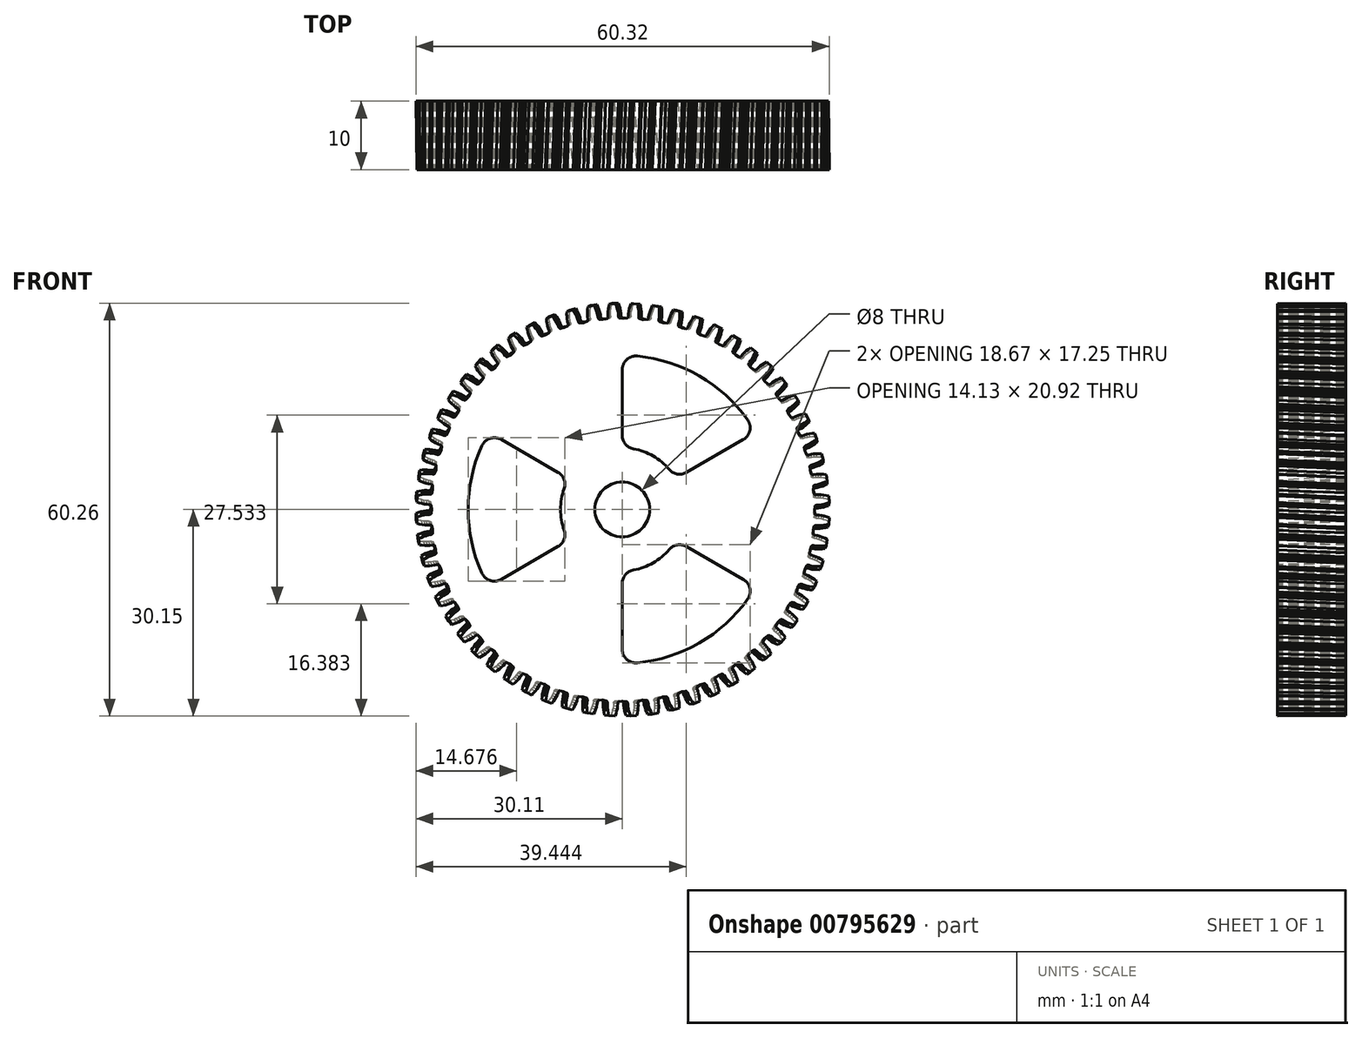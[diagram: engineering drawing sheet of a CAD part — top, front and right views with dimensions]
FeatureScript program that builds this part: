
annotation { "Feature Type Name" : "Feature", "Feature Type Description" : "" }
export const myFeature = defineFeature(function(context is Context, id is Id, definition is map)
    precondition{}
    {
        {
            var Q0;
            Q0=qCreatedBy(makeId("Front.planeOp"),FACE);
            var sketch = newSketch(context, id + "F0", { "sketchPlane" : qUnion([Q0])});
            skLineSegment(sketch, "E0", {"start": v(27.92, -0.53) * mm, "end": v(28, -1.15) * mm});
            skLineSegment(sketch, "E1", {"start": v(28, -1.15) * mm, "end": v(28.09, -1.2) * mm});
            skLineSegment(sketch, "E2", {"start": v(28.09, -1.2) * mm, "end": v(28.27, -1.26) * mm});
            skLineSegment(sketch, "E3", {"start": v(28.27, -1.26) * mm, "end": v(28.63, -1.3) * mm});
            skLineSegment(sketch, "E4", {"start": v(28.63, -1.3) * mm, "end": v(29, -1.35) * mm});
            skLineSegment(sketch, "E5", {"start": v(29, -1.35) * mm, "end": v(29.35, -1.44) * mm});
            skLineSegment(sketch, "E6", {"start": v(29.35, -1.44) * mm, "end": v(29.71, -1.55) * mm});
            skLineSegment(sketch, "E7", {"start": v(29.71, -1.55) * mm, "end": v(30.07, -1.68) * mm});
            skLineSegment(sketch, "E8", {"start": v(30.07, -1.68) * mm, "end": v(30, -2.6) * mm});
            skLineSegment(sketch, "E9", {"start": v(30, -2.6) * mm, "end": v(29.63, -2.69) * mm});
            skLineSegment(sketch, "E10", {"start": v(29.63, -2.69) * mm, "end": v(29.26, -2.74) * mm});
            skLineSegment(sketch, "E11", {"start": v(29.26, -2.74) * mm, "end": v(28.89, -2.78) * mm});
            skLineSegment(sketch, "E12", {"start": v(28.89, -2.78) * mm, "end": v(28.52, -2.79) * mm});
            skLineSegment(sketch, "E13", {"start": v(28.52, -2.79) * mm, "end": v(28.16, -2.77) * mm});
            skLineSegment(sketch, "E14", {"start": v(28.16, -2.77) * mm, "end": v(27.97, -2.8) * mm});
            skLineSegment(sketch, "E15", {"start": v(27.97, -2.8) * mm, "end": v(27.88, -2.84) * mm});
            skLineSegment(sketch, "E16", {"start": v(27.88, -2.84) * mm, "end": v(27.72, -3.44) * mm});
            skLineSegment(sketch, "E17", {"start": v(27.72, -3.44) * mm, "end": v(27.72, -4.07) * mm});
            skLineSegment(sketch, "E18", {"start": v(27.72, -4.07) * mm, "end": v(27.8, -4.13) * mm});
            skLineSegment(sketch, "E19", {"start": v(27.8, -4.13) * mm, "end": v(27.98, -4.2) * mm});
            skLineSegment(sketch, "E20", {"start": v(27.98, -4.2) * mm, "end": v(28.34, -4.28) * mm});
            skLineSegment(sketch, "E21", {"start": v(28.34, -4.28) * mm, "end": v(28.7, -4.37) * mm});
            skLineSegment(sketch, "E22", {"start": v(28.7, -4.37) * mm, "end": v(29.04, -4.5) * mm});
            skLineSegment(sketch, "E23", {"start": v(29.04, -4.5) * mm, "end": v(29.39, -4.65) * mm});
            skLineSegment(sketch, "E24", {"start": v(29.39, -4.65) * mm, "end": v(29.73, -4.81) * mm});
            skLineSegment(sketch, "E25", {"start": v(29.73, -4.81) * mm, "end": v(29.57, -5.73) * mm});
            skLineSegment(sketch, "E26", {"start": v(29.57, -5.73) * mm, "end": v(29.19, -5.77) * mm});
            skLineSegment(sketch, "E27", {"start": v(29.19, -5.77) * mm, "end": v(28.81, -5.79) * mm});
            skLineSegment(sketch, "E28", {"start": v(28.81, -5.79) * mm, "end": v(28.44, -5.79) * mm});
            skLineSegment(sketch, "E29", {"start": v(28.44, -5.79) * mm, "end": v(28.07, -5.75) * mm});
            skLineSegment(sketch, "E30", {"start": v(28.07, -5.75) * mm, "end": v(27.71, -5.7) * mm});
            skLineSegment(sketch, "E31", {"start": v(27.71, -5.7) * mm, "end": v(27.52, -5.7) * mm});
            skLineSegment(sketch, "E32", {"start": v(27.52, -5.7) * mm, "end": v(27.43, -5.74) * mm});
            skLineSegment(sketch, "E33", {"start": v(27.43, -5.74) * mm, "end": v(27.2, -6.32) * mm});
            skLineSegment(sketch, "E34", {"start": v(27.2, -6.32) * mm, "end": v(27.15, -6.94) * mm});
            skLineSegment(sketch, "E35", {"start": v(27.15, -6.94) * mm, "end": v(27.22, -7.01) * mm});
            skLineSegment(sketch, "E36", {"start": v(27.22, -7.01) * mm, "end": v(27.39, -7.1) * mm});
            skLineSegment(sketch, "E37", {"start": v(27.39, -7.1) * mm, "end": v(27.74, -7.21) * mm});
            skLineSegment(sketch, "E38", {"start": v(27.74, -7.21) * mm, "end": v(28.08, -7.35) * mm});
            skLineSegment(sketch, "E39", {"start": v(28.08, -7.35) * mm, "end": v(28.41, -7.5) * mm});
            skLineSegment(sketch, "E40", {"start": v(28.41, -7.5) * mm, "end": v(28.74, -7.7) * mm});
            skLineSegment(sketch, "E41", {"start": v(28.74, -7.7) * mm, "end": v(29.06, -7.9) * mm});
            skLineSegment(sketch, "E42", {"start": v(29.06, -7.9) * mm, "end": v(28.8, -8.79) * mm});
            skLineSegment(sketch, "E43", {"start": v(28.8, -8.79) * mm, "end": v(28.43, -8.79) * mm});
            skLineSegment(sketch, "E44", {"start": v(28.43, -8.79) * mm, "end": v(28.05, -8.77) * mm});
            skLineSegment(sketch, "E45", {"start": v(28.05, -8.77) * mm, "end": v(27.68, -8.73) * mm});
            skLineSegment(sketch, "E46", {"start": v(27.68, -8.73) * mm, "end": v(27.32, -8.66) * mm});
            skLineSegment(sketch, "E47", {"start": v(27.32, -8.66) * mm, "end": v(26.97, -8.56) * mm});
            skLineSegment(sketch, "E48", {"start": v(26.97, -8.56) * mm, "end": v(26.78, -8.55) * mm});
            skLineSegment(sketch, "E49", {"start": v(26.78, -8.55) * mm, "end": v(26.68, -8.57) * mm});
            skLineSegment(sketch, "E50", {"start": v(26.68, -8.57) * mm, "end": v(26.4, -9.13) * mm});
            skLineSegment(sketch, "E51", {"start": v(26.4, -9.13) * mm, "end": v(26.27, -9.74) * mm});
            skLineSegment(sketch, "E52", {"start": v(26.27, -9.74) * mm, "end": v(26.34, -9.82) * mm});
            skLineSegment(sketch, "E53", {"start": v(26.34, -9.82) * mm, "end": v(26.5, -9.93) * mm});
            skLineSegment(sketch, "E54", {"start": v(26.5, -9.93) * mm, "end": v(26.83, -10.07) * mm});
            skLineSegment(sketch, "E55", {"start": v(26.83, -10.07) * mm, "end": v(27.16, -10.24) * mm});
            skLineSegment(sketch, "E56", {"start": v(27.16, -10.24) * mm, "end": v(27.47, -10.44) * mm});
            skLineSegment(sketch, "E57", {"start": v(27.47, -10.44) * mm, "end": v(27.78, -10.65) * mm});
            skLineSegment(sketch, "E58", {"start": v(27.78, -10.65) * mm, "end": v(28.08, -10.89) * mm});
            skLineSegment(sketch, "E59", {"start": v(28.08, -10.89) * mm, "end": v(27.73, -11.75) * mm});
            skLineSegment(sketch, "E60", {"start": v(27.73, -11.75) * mm, "end": v(27.35, -11.71) * mm});
            skLineSegment(sketch, "E61", {"start": v(27.35, -11.71) * mm, "end": v(26.98, -11.65) * mm});
            skLineSegment(sketch, "E62", {"start": v(26.98, -11.65) * mm, "end": v(26.62, -11.57) * mm});
            skLineSegment(sketch, "E63", {"start": v(26.62, -11.57) * mm, "end": v(26.27, -11.46) * mm});
            skLineSegment(sketch, "E64", {"start": v(26.27, -11.46) * mm, "end": v(25.92, -11.33) * mm});
            skLineSegment(sketch, "E65", {"start": v(25.92, -11.33) * mm, "end": v(25.74, -11.3) * mm});
            skLineSegment(sketch, "E66", {"start": v(25.74, -11.3) * mm, "end": v(25.63, -11.31) * mm});
            skLineSegment(sketch, "E67", {"start": v(25.63, -11.31) * mm, "end": v(25.3, -11.84) * mm});
            skLineSegment(sketch, "E68", {"start": v(25.3, -11.84) * mm, "end": v(25.1, -12.43) * mm});
            skLineSegment(sketch, "E69", {"start": v(25.1, -12.43) * mm, "end": v(25.17, -12.52) * mm});
            skLineSegment(sketch, "E70", {"start": v(25.17, -12.52) * mm, "end": v(25.31, -12.64) * mm});
            skLineSegment(sketch, "E71", {"start": v(25.31, -12.64) * mm, "end": v(25.63, -12.82) * mm});
            skLineSegment(sketch, "E72", {"start": v(25.63, -12.82) * mm, "end": v(25.94, -13.02) * mm});
            skLineSegment(sketch, "E73", {"start": v(25.94, -13.02) * mm, "end": v(26.23, -13.25) * mm});
            skLineSegment(sketch, "E74", {"start": v(26.23, -13.25) * mm, "end": v(26.51, -13.5) * mm});
            skLineSegment(sketch, "E75", {"start": v(26.51, -13.5) * mm, "end": v(26.79, -13.76) * mm});
            skLineSegment(sketch, "E76", {"start": v(26.79, -13.76) * mm, "end": v(26.35, -14.59) * mm});
            skLineSegment(sketch, "E77", {"start": v(26.35, -14.59) * mm, "end": v(25.98, -14.5) * mm});
            skLineSegment(sketch, "E78", {"start": v(25.98, -14.5) * mm, "end": v(25.61, -14.4) * mm});
            skLineSegment(sketch, "E79", {"start": v(25.61, -14.4) * mm, "end": v(25.26, -14.3) * mm});
            skLineSegment(sketch, "E80", {"start": v(25.26, -14.3) * mm, "end": v(24.92, -14.15) * mm});
            skLineSegment(sketch, "E81", {"start": v(24.92, -14.15) * mm, "end": v(24.6, -13.98) * mm});
            skLineSegment(sketch, "E82", {"start": v(24.6, -13.98) * mm, "end": v(24.41, -13.93) * mm});
            skLineSegment(sketch, "E83", {"start": v(24.41, -13.93) * mm, "end": v(24.31, -13.93) * mm});
            skLineSegment(sketch, "E84", {"start": v(24.31, -13.93) * mm, "end": v(23.92, -14.42) * mm});
            skLineSegment(sketch, "E85", {"start": v(23.92, -14.42) * mm, "end": v(23.67, -15) * mm});
            skLineSegment(sketch, "E86", {"start": v(23.67, -15) * mm, "end": v(23.72, -15.08) * mm});
            skLineSegment(sketch, "E87", {"start": v(23.72, -15.08) * mm, "end": v(23.85, -15.22) * mm});
            skLineSegment(sketch, "E88", {"start": v(23.85, -15.22) * mm, "end": v(24.15, -15.43) * mm});
            skLineSegment(sketch, "E89", {"start": v(24.15, -15.43) * mm, "end": v(24.43, -15.66) * mm});
            skLineSegment(sketch, "E90", {"start": v(24.43, -15.66) * mm, "end": v(24.7, -15.92) * mm});
            skLineSegment(sketch, "E91", {"start": v(24.7, -15.92) * mm, "end": v(24.96, -16.2) * mm});
            skLineSegment(sketch, "E92", {"start": v(24.96, -16.2) * mm, "end": v(25.2, -16.49) * mm});
            skLineSegment(sketch, "E93", {"start": v(25.2, -16.49) * mm, "end": v(24.68, -17.26) * mm});
            skLineSegment(sketch, "E94", {"start": v(24.68, -17.26) * mm, "end": v(24.32, -17.14) * mm});
            skLineSegment(sketch, "E95", {"start": v(24.32, -17.14) * mm, "end": v(23.97, -17) * mm});
            skLineSegment(sketch, "E96", {"start": v(23.97, -17) * mm, "end": v(23.63, -16.85) * mm});
            skLineSegment(sketch, "E97", {"start": v(23.63, -16.85) * mm, "end": v(23.3, -16.67) * mm});
            skLineSegment(sketch, "E98", {"start": v(23.3, -16.67) * mm, "end": v(23, -16.48) * mm});
            skLineSegment(sketch, "E99", {"start": v(23, -16.48) * mm, "end": v(22.82, -16.41) * mm});
            skLineSegment(sketch, "E100", {"start": v(22.82, -16.41) * mm, "end": v(22.72, -16.4) * mm});
            skLineSegment(sketch, "E101", {"start": v(22.72, -16.4) * mm, "end": v(22.28, -16.84) * mm});
            skLineSegment(sketch, "E102", {"start": v(22.28, -16.84) * mm, "end": v(21.98, -17.38) * mm});
            skLineSegment(sketch, "E103", {"start": v(21.98, -17.38) * mm, "end": v(22.02, -17.48) * mm});
            skLineSegment(sketch, "E104", {"start": v(22.02, -17.48) * mm, "end": v(22.13, -17.63) * mm});
            skLineSegment(sketch, "E105", {"start": v(22.13, -17.63) * mm, "end": v(22.4, -17.87) * mm});
            skLineSegment(sketch, "E106", {"start": v(22.4, -17.87) * mm, "end": v(22.66, -18.13) * mm});
            skLineSegment(sketch, "E107", {"start": v(22.66, -18.13) * mm, "end": v(22.9, -18.42) * mm});
            skLineSegment(sketch, "E108", {"start": v(22.9, -18.42) * mm, "end": v(23.13, -18.72) * mm});
            skLineSegment(sketch, "E109", {"start": v(23.13, -18.72) * mm, "end": v(23.34, -19.03) * mm});
            skLineSegment(sketch, "E110", {"start": v(23.34, -19.03) * mm, "end": v(22.74, -19.75) * mm});
            skLineSegment(sketch, "E111", {"start": v(22.74, -19.75) * mm, "end": v(22.4, -19.59) * mm});
            skLineSegment(sketch, "E112", {"start": v(22.4, -19.59) * mm, "end": v(22.06, -19.42) * mm});
            skLineSegment(sketch, "E113", {"start": v(22.06, -19.42) * mm, "end": v(21.74, -19.23) * mm});
            skLineSegment(sketch, "E114", {"start": v(21.74, -19.23) * mm, "end": v(21.44, -19.02) * mm});
            skLineSegment(sketch, "E115", {"start": v(21.44, -19.02) * mm, "end": v(21.15, -18.8) * mm});
            skLineSegment(sketch, "E116", {"start": v(21.15, -18.8) * mm, "end": v(20.98, -18.7) * mm});
            skLineSegment(sketch, "E117", {"start": v(20.98, -18.7) * mm, "end": v(20.88, -18.68) * mm});
            skLineSegment(sketch, "E118", {"start": v(20.88, -18.68) * mm, "end": v(20.4, -19.08) * mm});
            skLineSegment(sketch, "E119", {"start": v(20.4, -19.08) * mm, "end": v(20.04, -19.59) * mm});
            skLineSegment(sketch, "E120", {"start": v(20.04, -19.59) * mm, "end": v(20.07, -19.68) * mm});
            skLineSegment(sketch, "E121", {"start": v(20.07, -19.68) * mm, "end": v(20.16, -19.85) * mm});
            skLineSegment(sketch, "E122", {"start": v(20.16, -19.85) * mm, "end": v(20.41, -20.12) * mm});
            skLineSegment(sketch, "E123", {"start": v(20.41, -20.12) * mm, "end": v(20.64, -20.4) * mm});
            skLineSegment(sketch, "E124", {"start": v(20.64, -20.4) * mm, "end": v(20.85, -20.7) * mm});
            skLineSegment(sketch, "E125", {"start": v(20.85, -20.7) * mm, "end": v(21.04, -21.03) * mm});
            skLineSegment(sketch, "E126", {"start": v(21.04, -21.03) * mm, "end": v(21.22, -21.37) * mm});
            skLineSegment(sketch, "E127", {"start": v(21.22, -21.37) * mm, "end": v(20.55, -22.01) * mm});
            skLineSegment(sketch, "E128", {"start": v(20.55, -22.01) * mm, "end": v(20.22, -21.82) * mm});
            skLineSegment(sketch, "E129", {"start": v(20.22, -21.82) * mm, "end": v(19.9, -21.62) * mm});
            skLineSegment(sketch, "E130", {"start": v(19.9, -21.62) * mm, "end": v(19.6, -21.4) * mm});
            skLineSegment(sketch, "E131", {"start": v(19.6, -21.4) * mm, "end": v(19.33, -21.16) * mm});
            skLineSegment(sketch, "E132", {"start": v(19.33, -21.16) * mm, "end": v(19.07, -20.9) * mm});
            skLineSegment(sketch, "E133", {"start": v(19.07, -20.9) * mm, "end": v(18.91, -20.8) * mm});
            skLineSegment(sketch, "E134", {"start": v(18.91, -20.8) * mm, "end": v(18.82, -20.76) * mm});
            skLineSegment(sketch, "E135", {"start": v(18.82, -20.76) * mm, "end": v(18.3, -21.1) * mm});
            skLineSegment(sketch, "E136", {"start": v(18.3, -21.1) * mm, "end": v(17.88, -21.57) * mm});
            skLineSegment(sketch, "E137", {"start": v(17.88, -21.57) * mm, "end": v(17.9, -21.67) * mm});
            skLineSegment(sketch, "E138", {"start": v(17.9, -21.67) * mm, "end": v(17.98, -21.85) * mm});
            skLineSegment(sketch, "E139", {"start": v(17.98, -21.85) * mm, "end": v(18.2, -22.14) * mm});
            skLineSegment(sketch, "E140", {"start": v(18.2, -22.14) * mm, "end": v(18.4, -22.45) * mm});
            skLineSegment(sketch, "E141", {"start": v(18.4, -22.45) * mm, "end": v(18.57, -22.77) * mm});
            skLineSegment(sketch, "E142", {"start": v(18.57, -22.77) * mm, "end": v(18.73, -23.12) * mm});
            skLineSegment(sketch, "E143", {"start": v(18.73, -23.12) * mm, "end": v(18.87, -23.47) * mm});
            skLineSegment(sketch, "E144", {"start": v(18.87, -23.47) * mm, "end": v(18.14, -24.04) * mm});
            skLineSegment(sketch, "E145", {"start": v(18.14, -24.04) * mm, "end": v(17.83, -23.82) * mm});
            skLineSegment(sketch, "E146", {"start": v(17.83, -23.82) * mm, "end": v(17.54, -23.58) * mm});
            skLineSegment(sketch, "E147", {"start": v(17.54, -23.58) * mm, "end": v(17.26, -23.33) * mm});
            skLineSegment(sketch, "E148", {"start": v(17.26, -23.33) * mm, "end": v(17.01, -23.06) * mm});
            skLineSegment(sketch, "E149", {"start": v(17.01, -23.06) * mm, "end": v(16.78, -22.78) * mm});
            skLineSegment(sketch, "E150", {"start": v(16.78, -22.78) * mm, "end": v(16.64, -22.66) * mm});
            skLineSegment(sketch, "E151", {"start": v(16.64, -22.66) * mm, "end": v(16.54, -22.61) * mm});
            skLineSegment(sketch, "E152", {"start": v(16.54, -22.61) * mm, "end": v(15.99, -22.9) * mm});
            skLineSegment(sketch, "E153", {"start": v(15.99, -22.9) * mm, "end": v(15.53, -23.32) * mm});
            skLineSegment(sketch, "E154", {"start": v(15.53, -23.32) * mm, "end": v(15.54, -23.43) * mm});
            skLineSegment(sketch, "E155", {"start": v(15.54, -23.43) * mm, "end": v(15.6, -23.6) * mm});
            skLineSegment(sketch, "E156", {"start": v(15.6, -23.6) * mm, "end": v(15.78, -23.92) * mm});
            skLineSegment(sketch, "E157", {"start": v(15.78, -23.92) * mm, "end": v(15.95, -24.25) * mm});
            skLineSegment(sketch, "E158", {"start": v(15.95, -24.25) * mm, "end": v(16.1, -24.6) * mm});
            skLineSegment(sketch, "E159", {"start": v(16.1, -24.6) * mm, "end": v(16.21, -24.95) * mm});
            skLineSegment(sketch, "E160", {"start": v(16.21, -24.95) * mm, "end": v(16.32, -25.31) * mm});
            skLineSegment(sketch, "E161", {"start": v(16.32, -25.31) * mm, "end": v(15.53, -25.8) * mm});
            skLineSegment(sketch, "E162", {"start": v(15.53, -25.8) * mm, "end": v(15.24, -25.55) * mm});
            skLineSegment(sketch, "E163", {"start": v(15.24, -25.55) * mm, "end": v(14.98, -25.28) * mm});
            skLineSegment(sketch, "E164", {"start": v(14.98, -25.28) * mm, "end": v(14.73, -25) * mm});
            skLineSegment(sketch, "E165", {"start": v(14.73, -25) * mm, "end": v(14.51, -24.71) * mm});
            skLineSegment(sketch, "E166", {"start": v(14.51, -24.71) * mm, "end": v(14.31, -24.4) * mm});
            skLineSegment(sketch, "E167", {"start": v(14.31, -24.4) * mm, "end": v(14.18, -24.27) * mm});
            skLineSegment(sketch, "E168", {"start": v(14.18, -24.27) * mm, "end": v(14.09, -24.22) * mm});
            skLineSegment(sketch, "E169", {"start": v(14.09, -24.22) * mm, "end": v(13.5, -24.45) * mm});
            skLineSegment(sketch, "E170", {"start": v(13.5, -24.45) * mm, "end": v(13, -24.82) * mm});
            skLineSegment(sketch, "E171", {"start": v(13, -24.82) * mm, "end": v(13, -24.92) * mm});
            skLineSegment(sketch, "E172", {"start": v(13, -24.92) * mm, "end": v(13.05, -25.1) * mm});
            skLineSegment(sketch, "E173", {"start": v(13.05, -25.1) * mm, "end": v(13.2, -25.44) * mm});
            skLineSegment(sketch, "E174", {"start": v(13.2, -25.44) * mm, "end": v(13.33, -25.78) * mm});
            skLineSegment(sketch, "E175", {"start": v(13.33, -25.78) * mm, "end": v(13.43, -26.14) * mm});
            skLineSegment(sketch, "E176", {"start": v(13.43, -26.14) * mm, "end": v(13.52, -26.5) * mm});
            skLineSegment(sketch, "E177", {"start": v(13.52, -26.5) * mm, "end": v(13.58, -26.88) * mm});
            skLineSegment(sketch, "E178", {"start": v(13.58, -26.88) * mm, "end": v(12.74, -27.29) * mm});
            skLineSegment(sketch, "E179", {"start": v(12.74, -27.29) * mm, "end": v(12.5, -27) * mm});
            skLineSegment(sketch, "E180", {"start": v(12.5, -27) * mm, "end": v(12.25, -26.71) * mm});
            skLineSegment(sketch, "E181", {"start": v(12.25, -26.71) * mm, "end": v(12.04, -26.4) * mm});
            skLineSegment(sketch, "E182", {"start": v(12.04, -26.4) * mm, "end": v(11.85, -26.1) * mm});
            skLineSegment(sketch, "E183", {"start": v(11.85, -26.1) * mm, "end": v(11.68, -25.77) * mm});
            skLineSegment(sketch, "E184", {"start": v(11.68, -25.77) * mm, "end": v(11.56, -25.62) * mm});
            skLineSegment(sketch, "E185", {"start": v(11.56, -25.62) * mm, "end": v(11.48, -25.56) * mm});
            skLineSegment(sketch, "E186", {"start": v(11.48, -25.56) * mm, "end": v(10.88, -25.72) * mm});
            skLineSegment(sketch, "E187", {"start": v(10.88, -25.72) * mm, "end": v(10.34, -26.04) * mm});
            skLineSegment(sketch, "E188", {"start": v(10.34, -26.04) * mm, "end": v(10.33, -26.14) * mm});
            skLineSegment(sketch, "E189", {"start": v(10.33, -26.14) * mm, "end": v(10.35, -26.33) * mm});
            skLineSegment(sketch, "E190", {"start": v(10.35, -26.33) * mm, "end": v(10.47, -26.68) * mm});
            skLineSegment(sketch, "E191", {"start": v(10.47, -26.68) * mm, "end": v(10.56, -27.03) * mm});
            skLineSegment(sketch, "E192", {"start": v(10.56, -27.03) * mm, "end": v(10.63, -27.4) * mm});
            skLineSegment(sketch, "E193", {"start": v(10.63, -27.4) * mm, "end": v(10.67, -27.77) * mm});
            skLineSegment(sketch, "E194", {"start": v(10.67, -27.77) * mm, "end": v(10.7, -28.15) * mm});
            skLineSegment(sketch, "E195", {"start": v(10.7, -28.15) * mm, "end": v(9.82, -28.47) * mm});
            skLineSegment(sketch, "E196", {"start": v(9.82, -28.47) * mm, "end": v(9.6, -28.16) * mm});
            skLineSegment(sketch, "E197", {"start": v(9.6, -28.16) * mm, "end": v(9.4, -27.85) * mm});
            skLineSegment(sketch, "E198", {"start": v(9.4, -27.85) * mm, "end": v(9.2, -27.52) * mm});
            skLineSegment(sketch, "E199", {"start": v(9.2, -27.52) * mm, "end": v(9.06, -27.19) * mm});
            skLineSegment(sketch, "E200", {"start": v(9.06, -27.19) * mm, "end": v(8.92, -26.85) * mm});
            skLineSegment(sketch, "E201", {"start": v(8.92, -26.85) * mm, "end": v(8.82, -26.7) * mm});
            skLineSegment(sketch, "E202", {"start": v(8.82, -26.7) * mm, "end": v(8.74, -26.62) * mm});
            skLineSegment(sketch, "E203", {"start": v(8.74, -26.62) * mm, "end": v(8.13, -26.72) * mm});
            skLineSegment(sketch, "E204", {"start": v(8.13, -26.72) * mm, "end": v(7.56, -26.98) * mm});
            skLineSegment(sketch, "E205", {"start": v(7.56, -26.98) * mm, "end": v(7.54, -27.08) * mm});
            skLineSegment(sketch, "E206", {"start": v(7.54, -27.08) * mm, "end": v(7.54, -27.27) * mm});
            skLineSegment(sketch, "E207", {"start": v(7.54, -27.27) * mm, "end": v(7.62, -27.63) * mm});
            skLineSegment(sketch, "E208", {"start": v(7.62, -27.63) * mm, "end": v(7.68, -27.99) * mm});
            skLineSegment(sketch, "E209", {"start": v(7.68, -27.99) * mm, "end": v(7.7, -28.36) * mm});
            skLineSegment(sketch, "E210", {"start": v(7.7, -28.36) * mm, "end": v(7.7, -28.74) * mm});
            skLineSegment(sketch, "E211", {"start": v(7.7, -28.74) * mm, "end": v(7.7, -29.12) * mm});
            skLineSegment(sketch, "E212", {"start": v(7.7, -29.12) * mm, "end": v(6.8, -29.34) * mm});
            skLineSegment(sketch, "E213", {"start": v(6.8, -29.34) * mm, "end": v(6.6, -29.01) * mm});
            skLineSegment(sketch, "E214", {"start": v(6.6, -29.01) * mm, "end": v(6.43, -28.68) * mm});
            skLineSegment(sketch, "E215", {"start": v(6.43, -28.68) * mm, "end": v(6.28, -28.33) * mm});
            skLineSegment(sketch, "E216", {"start": v(6.28, -28.33) * mm, "end": v(6.16, -27.99) * mm});
            skLineSegment(sketch, "E217", {"start": v(6.16, -27.99) * mm, "end": v(6.07, -27.63) * mm});
            skLineSegment(sketch, "E218", {"start": v(6.07, -27.63) * mm, "end": v(5.98, -27.47) * mm});
            skLineSegment(sketch, "E219", {"start": v(5.98, -27.47) * mm, "end": v(5.91, -27.39) * mm});
            skLineSegment(sketch, "E220", {"start": v(5.91, -27.39) * mm, "end": v(5.3, -27.42) * mm});
            skLineSegment(sketch, "E221", {"start": v(5.3, -27.42) * mm, "end": v(4.7, -27.62) * mm});
            skLineSegment(sketch, "E222", {"start": v(4.7, -27.62) * mm, "end": v(4.67, -27.72) * mm});
            skLineSegment(sketch, "E223", {"start": v(4.67, -27.72) * mm, "end": v(4.65, -27.9) * mm});
            skLineSegment(sketch, "E224", {"start": v(4.65, -27.9) * mm, "end": v(4.7, -28.27) * mm});
            skLineSegment(sketch, "E225", {"start": v(4.7, -28.27) * mm, "end": v(4.7, -28.64) * mm});
            skLineSegment(sketch, "E226", {"start": v(4.7, -28.64) * mm, "end": v(4.7, -29) * mm});
            skLineSegment(sketch, "E227", {"start": v(4.7, -29) * mm, "end": v(4.66, -29.38) * mm});
            skLineSegment(sketch, "E228", {"start": v(4.66, -29.38) * mm, "end": v(4.61, -29.76) * mm});
            skLineSegment(sketch, "E229", {"start": v(4.61, -29.76) * mm, "end": v(3.69, -29.9) * mm});
            skLineSegment(sketch, "E230", {"start": v(3.69, -29.9) * mm, "end": v(3.53, -29.54) * mm});
            skLineSegment(sketch, "E231", {"start": v(3.53, -29.54) * mm, "end": v(3.4, -29.2) * mm});
            skLineSegment(sketch, "E232", {"start": v(3.4, -29.2) * mm, "end": v(3.29, -28.84) * mm});
            skLineSegment(sketch, "E233", {"start": v(3.29, -28.84) * mm, "end": v(3.2, -28.48) * mm});
            skLineSegment(sketch, "E234", {"start": v(3.2, -28.48) * mm, "end": v(3.15, -28.12) * mm});
            skLineSegment(sketch, "E235", {"start": v(3.15, -28.12) * mm, "end": v(3.08, -27.94) * mm});
            skLineSegment(sketch, "E236", {"start": v(3.08, -27.94) * mm, "end": v(3.02, -27.86) * mm});
            skLineSegment(sketch, "E237", {"start": v(3.02, -27.86) * mm, "end": v(2.4, -27.83) * mm});
            skLineSegment(sketch, "E238", {"start": v(2.4, -27.83) * mm, "end": v(1.79, -27.96) * mm});
            skLineSegment(sketch, "E239", {"start": v(1.79, -27.96) * mm, "end": v(1.74, -28.06) * mm});
            skLineSegment(sketch, "E240", {"start": v(1.74, -28.06) * mm, "end": v(1.7, -28.24) * mm});
            skLineSegment(sketch, "E241", {"start": v(1.7, -28.24) * mm, "end": v(1.7, -28.6) * mm});
            skLineSegment(sketch, "E242", {"start": v(1.7, -28.6) * mm, "end": v(1.7, -28.97) * mm});
            skLineSegment(sketch, "E243", {"start": v(1.7, -28.97) * mm, "end": v(1.64, -29.34) * mm});
            skLineSegment(sketch, "E244", {"start": v(1.64, -29.34) * mm, "end": v(1.57, -29.71) * mm});
            skLineSegment(sketch, "E245", {"start": v(1.57, -29.71) * mm, "end": v(1.47, -30.08) * mm});
            skLineSegment(sketch, "E246", {"start": v(1.47, -30.08) * mm, "end": v(0.54, -30.11) * mm});
            skLineSegment(sketch, "E247", {"start": v(0.54, -30.11) * mm, "end": v(0.43, -29.75) * mm});
            skLineSegment(sketch, "E248", {"start": v(0.43, -29.75) * mm, "end": v(0.33, -29.39) * mm});
            skLineSegment(sketch, "E249", {"start": v(0.33, -29.39) * mm, "end": v(0.25, -29.02) * mm});
            skLineSegment(sketch, "E250", {"start": v(0.25, -29.02) * mm, "end": v(0.21, -28.66) * mm});
            skLineSegment(sketch, "E251", {"start": v(0.21, -28.66) * mm, "end": v(0.19, -28.3) * mm});
            skLineSegment(sketch, "E252", {"start": v(0.19, -28.3) * mm, "end": v(0.14, -28.11) * mm});
            skLineSegment(sketch, "E253", {"start": v(0.14, -28.11) * mm, "end": v(0.1, -28.02) * mm});
            skLineSegment(sketch, "E254", {"start": v(0.1, -28.02) * mm, "end": v(-0.53, -27.92) * mm});
            skLineSegment(sketch, "E255", {"start": v(-0.53, -27.92) * mm, "end": v(-1.15, -28) * mm});
            skLineSegment(sketch, "E256", {"start": v(-1.15, -28) * mm, "end": v(-1.2, -28.09) * mm});
            skLineSegment(sketch, "E257", {"start": v(-1.2, -28.09) * mm, "end": v(-1.26, -28.27) * mm});
            skLineSegment(sketch, "E258", {"start": v(-1.26, -28.27) * mm, "end": v(-1.3, -28.63) * mm});
            skLineSegment(sketch, "E259", {"start": v(-1.3, -28.63) * mm, "end": v(-1.35, -29) * mm});
            skLineSegment(sketch, "E260", {"start": v(-1.35, -29) * mm, "end": v(-1.44, -29.35) * mm});
            skLineSegment(sketch, "E261", {"start": v(-1.44, -29.35) * mm, "end": v(-1.55, -29.71) * mm});
            skLineSegment(sketch, "E262", {"start": v(-1.55, -29.71) * mm, "end": v(-1.68, -30.07) * mm});
            skLineSegment(sketch, "E263", {"start": v(-1.68, -30.07) * mm, "end": v(-2.6, -30) * mm});
            skLineSegment(sketch, "E264", {"start": v(-2.6, -30) * mm, "end": v(-2.69, -29.63) * mm});
            skLineSegment(sketch, "E265", {"start": v(-2.69, -29.63) * mm, "end": v(-2.74, -29.26) * mm});
            skLineSegment(sketch, "E266", {"start": v(-2.74, -29.26) * mm, "end": v(-2.78, -28.89) * mm});
            skLineSegment(sketch, "E267", {"start": v(-2.78, -28.89) * mm, "end": v(-2.79, -28.52) * mm});
            skLineSegment(sketch, "E268", {"start": v(-2.79, -28.52) * mm, "end": v(-2.77, -28.16) * mm});
            skLineSegment(sketch, "E269", {"start": v(-2.77, -28.16) * mm, "end": v(-2.8, -27.97) * mm});
            skLineSegment(sketch, "E270", {"start": v(-2.8, -27.97) * mm, "end": v(-2.84, -27.88) * mm});
            skLineSegment(sketch, "E271", {"start": v(-2.84, -27.88) * mm, "end": v(-3.44, -27.72) * mm});
            skLineSegment(sketch, "E272", {"start": v(-3.44, -27.72) * mm, "end": v(-4.07, -27.72) * mm});
            skLineSegment(sketch, "E273", {"start": v(-4.07, -27.72) * mm, "end": v(-4.13, -27.8) * mm});
            skLineSegment(sketch, "E274", {"start": v(-4.13, -27.8) * mm, "end": v(-4.2, -27.98) * mm});
            skLineSegment(sketch, "E275", {"start": v(-4.2, -27.98) * mm, "end": v(-4.28, -28.34) * mm});
            skLineSegment(sketch, "E276", {"start": v(-4.28, -28.34) * mm, "end": v(-4.37, -28.7) * mm});
            skLineSegment(sketch, "E277", {"start": v(-4.37, -28.7) * mm, "end": v(-4.5, -29.04) * mm});
            skLineSegment(sketch, "E278", {"start": v(-4.5, -29.04) * mm, "end": v(-4.65, -29.39) * mm});
            skLineSegment(sketch, "E279", {"start": v(-4.65, -29.39) * mm, "end": v(-4.81, -29.73) * mm});
            skLineSegment(sketch, "E280", {"start": v(-4.81, -29.73) * mm, "end": v(-5.73, -29.57) * mm});
            skLineSegment(sketch, "E281", {"start": v(-5.73, -29.57) * mm, "end": v(-5.77, -29.19) * mm});
            skLineSegment(sketch, "E282", {"start": v(-5.77, -29.19) * mm, "end": v(-5.79, -28.81) * mm});
            skLineSegment(sketch, "E283", {"start": v(-5.79, -28.81) * mm, "end": v(-5.79, -28.44) * mm});
            skLineSegment(sketch, "E284", {"start": v(-5.79, -28.44) * mm, "end": v(-5.75, -28.07) * mm});
            skLineSegment(sketch, "E285", {"start": v(-5.75, -28.07) * mm, "end": v(-5.7, -27.71) * mm});
            skLineSegment(sketch, "E286", {"start": v(-5.7, -27.71) * mm, "end": v(-5.7, -27.52) * mm});
            skLineSegment(sketch, "E287", {"start": v(-5.7, -27.52) * mm, "end": v(-5.74, -27.43) * mm});
            skLineSegment(sketch, "E288", {"start": v(-5.74, -27.43) * mm, "end": v(-6.32, -27.2) * mm});
            skLineSegment(sketch, "E289", {"start": v(-6.32, -27.2) * mm, "end": v(-6.94, -27.15) * mm});
            skLineSegment(sketch, "E290", {"start": v(-6.94, -27.15) * mm, "end": v(-7.01, -27.22) * mm});
            skLineSegment(sketch, "E291", {"start": v(-7.01, -27.22) * mm, "end": v(-7.1, -27.39) * mm});
            skLineSegment(sketch, "E292", {"start": v(-7.1, -27.39) * mm, "end": v(-7.21, -27.74) * mm});
            skLineSegment(sketch, "E293", {"start": v(-7.21, -27.74) * mm, "end": v(-7.35, -28.08) * mm});
            skLineSegment(sketch, "E294", {"start": v(-7.35, -28.08) * mm, "end": v(-7.5, -28.41) * mm});
            skLineSegment(sketch, "E295", {"start": v(-7.5, -28.41) * mm, "end": v(-7.7, -28.74) * mm});
            skLineSegment(sketch, "E296", {"start": v(-7.7, -28.74) * mm, "end": v(-7.9, -29.06) * mm});
            skLineSegment(sketch, "E297", {"start": v(-7.9, -29.06) * mm, "end": v(-8.79, -28.8) * mm});
            skLineSegment(sketch, "E298", {"start": v(-8.79, -28.8) * mm, "end": v(-8.79, -28.43) * mm});
            skLineSegment(sketch, "E299", {"start": v(-8.79, -28.43) * mm, "end": v(-8.77, -28.05) * mm});
            skLineSegment(sketch, "E300", {"start": v(-8.77, -28.05) * mm, "end": v(-8.73, -27.68) * mm});
            skLineSegment(sketch, "E301", {"start": v(-8.73, -27.68) * mm, "end": v(-8.66, -27.32) * mm});
            skLineSegment(sketch, "E302", {"start": v(-8.66, -27.32) * mm, "end": v(-8.56, -26.97) * mm});
            skLineSegment(sketch, "E303", {"start": v(-8.56, -26.97) * mm, "end": v(-8.55, -26.78) * mm});
            skLineSegment(sketch, "E304", {"start": v(-8.55, -26.78) * mm, "end": v(-8.57, -26.68) * mm});
            skLineSegment(sketch, "E305", {"start": v(-8.57, -26.68) * mm, "end": v(-9.13, -26.4) * mm});
            skLineSegment(sketch, "E306", {"start": v(-9.13, -26.4) * mm, "end": v(-9.74, -26.27) * mm});
            skLineSegment(sketch, "E307", {"start": v(-9.74, -26.27) * mm, "end": v(-9.82, -26.34) * mm});
            skLineSegment(sketch, "E308", {"start": v(-9.82, -26.34) * mm, "end": v(-9.93, -26.5) * mm});
            skLineSegment(sketch, "E309", {"start": v(-9.93, -26.5) * mm, "end": v(-10.07, -26.83) * mm});
            skLineSegment(sketch, "E310", {"start": v(-10.07, -26.83) * mm, "end": v(-10.24, -27.16) * mm});
            skLineSegment(sketch, "E311", {"start": v(-10.24, -27.16) * mm, "end": v(-10.44, -27.47) * mm});
            skLineSegment(sketch, "E312", {"start": v(-10.44, -27.47) * mm, "end": v(-10.65, -27.78) * mm});
            skLineSegment(sketch, "E313", {"start": v(-10.65, -27.78) * mm, "end": v(-10.89, -28.08) * mm});
            skLineSegment(sketch, "E314", {"start": v(-10.89, -28.08) * mm, "end": v(-11.75, -27.73) * mm});
            skLineSegment(sketch, "E315", {"start": v(-11.75, -27.73) * mm, "end": v(-11.71, -27.35) * mm});
            skLineSegment(sketch, "E316", {"start": v(-11.71, -27.35) * mm, "end": v(-11.65, -26.98) * mm});
            skLineSegment(sketch, "E317", {"start": v(-11.65, -26.98) * mm, "end": v(-11.57, -26.62) * mm});
            skLineSegment(sketch, "E318", {"start": v(-11.57, -26.62) * mm, "end": v(-11.46, -26.27) * mm});
            skLineSegment(sketch, "E319", {"start": v(-11.46, -26.27) * mm, "end": v(-11.33, -25.92) * mm});
            skLineSegment(sketch, "E320", {"start": v(-11.33, -25.92) * mm, "end": v(-11.3, -25.74) * mm});
            skLineSegment(sketch, "E321", {"start": v(-11.3, -25.74) * mm, "end": v(-11.31, -25.63) * mm});
            skLineSegment(sketch, "E322", {"start": v(-11.31, -25.63) * mm, "end": v(-11.84, -25.3) * mm});
            skLineSegment(sketch, "E323", {"start": v(-11.84, -25.3) * mm, "end": v(-12.43, -25.1) * mm});
            skLineSegment(sketch, "E324", {"start": v(-12.43, -25.1) * mm, "end": v(-12.52, -25.17) * mm});
            skLineSegment(sketch, "E325", {"start": v(-12.52, -25.17) * mm, "end": v(-12.64, -25.31) * mm});
            skLineSegment(sketch, "E326", {"start": v(-12.64, -25.31) * mm, "end": v(-12.82, -25.63) * mm});
            skLineSegment(sketch, "E327", {"start": v(-12.82, -25.63) * mm, "end": v(-13.02, -25.94) * mm});
            skLineSegment(sketch, "E328", {"start": v(-13.02, -25.94) * mm, "end": v(-13.25, -26.23) * mm});
            skLineSegment(sketch, "E329", {"start": v(-13.25, -26.23) * mm, "end": v(-13.5, -26.51) * mm});
            skLineSegment(sketch, "E330", {"start": v(-13.5, -26.51) * mm, "end": v(-13.76, -26.79) * mm});
            skLineSegment(sketch, "E331", {"start": v(-13.76, -26.79) * mm, "end": v(-14.59, -26.35) * mm});
            skLineSegment(sketch, "E332", {"start": v(-14.59, -26.35) * mm, "end": v(-14.5, -25.98) * mm});
            skLineSegment(sketch, "E333", {"start": v(-14.5, -25.98) * mm, "end": v(-14.4, -25.61) * mm});
            skLineSegment(sketch, "E334", {"start": v(-14.4, -25.61) * mm, "end": v(-14.3, -25.26) * mm});
            skLineSegment(sketch, "E335", {"start": v(-14.3, -25.26) * mm, "end": v(-14.15, -24.92) * mm});
            skLineSegment(sketch, "E336", {"start": v(-14.15, -24.92) * mm, "end": v(-13.98, -24.6) * mm});
            skLineSegment(sketch, "E337", {"start": v(-13.98, -24.6) * mm, "end": v(-13.93, -24.41) * mm});
            skLineSegment(sketch, "E338", {"start": v(-13.93, -24.41) * mm, "end": v(-13.93, -24.31) * mm});
            skLineSegment(sketch, "E339", {"start": v(-13.93, -24.31) * mm, "end": v(-14.42, -23.92) * mm});
            skLineSegment(sketch, "E340", {"start": v(-14.42, -23.92) * mm, "end": v(-15, -23.67) * mm});
            skLineSegment(sketch, "E341", {"start": v(-15, -23.67) * mm, "end": v(-15.08, -23.72) * mm});
            skLineSegment(sketch, "E342", {"start": v(-15.08, -23.72) * mm, "end": v(-15.22, -23.85) * mm});
            skLineSegment(sketch, "E343", {"start": v(-15.22, -23.85) * mm, "end": v(-15.43, -24.15) * mm});
            skLineSegment(sketch, "E344", {"start": v(-15.43, -24.15) * mm, "end": v(-15.66, -24.43) * mm});
            skLineSegment(sketch, "E345", {"start": v(-15.66, -24.43) * mm, "end": v(-15.92, -24.7) * mm});
            skLineSegment(sketch, "E346", {"start": v(-15.92, -24.7) * mm, "end": v(-16.2, -24.96) * mm});
            skLineSegment(sketch, "E347", {"start": v(-16.2, -24.96) * mm, "end": v(-16.49, -25.2) * mm});
            skLineSegment(sketch, "E348", {"start": v(-16.49, -25.2) * mm, "end": v(-17.26, -24.68) * mm});
            skLineSegment(sketch, "E349", {"start": v(-17.26, -24.68) * mm, "end": v(-17.14, -24.32) * mm});
            skLineSegment(sketch, "E350", {"start": v(-17.14, -24.32) * mm, "end": v(-17, -23.97) * mm});
            skLineSegment(sketch, "E351", {"start": v(-17, -23.97) * mm, "end": v(-16.85, -23.63) * mm});
            skLineSegment(sketch, "E352", {"start": v(-16.85, -23.63) * mm, "end": v(-16.67, -23.3) * mm});
            skLineSegment(sketch, "E353", {"start": v(-16.67, -23.3) * mm, "end": v(-16.48, -23) * mm});
            skLineSegment(sketch, "E354", {"start": v(-16.48, -23) * mm, "end": v(-16.41, -22.82) * mm});
            skLineSegment(sketch, "E355", {"start": v(-16.41, -22.82) * mm, "end": v(-16.4, -22.72) * mm});
            skLineSegment(sketch, "E356", {"start": v(-16.4, -22.72) * mm, "end": v(-16.84, -22.28) * mm});
            skLineSegment(sketch, "E357", {"start": v(-16.84, -22.28) * mm, "end": v(-17.38, -21.98) * mm});
            skLineSegment(sketch, "E358", {"start": v(-17.38, -21.98) * mm, "end": v(-17.48, -22.02) * mm});
            skLineSegment(sketch, "E359", {"start": v(-17.48, -22.02) * mm, "end": v(-17.63, -22.13) * mm});
            skLineSegment(sketch, "E360", {"start": v(-17.63, -22.13) * mm, "end": v(-17.87, -22.4) * mm});
            skLineSegment(sketch, "E361", {"start": v(-17.87, -22.4) * mm, "end": v(-18.13, -22.66) * mm});
            skLineSegment(sketch, "E362", {"start": v(-18.13, -22.66) * mm, "end": v(-18.42, -22.9) * mm});
            skLineSegment(sketch, "E363", {"start": v(-18.42, -22.9) * mm, "end": v(-18.72, -23.13) * mm});
            skLineSegment(sketch, "E364", {"start": v(-18.72, -23.13) * mm, "end": v(-19.03, -23.34) * mm});
            skLineSegment(sketch, "E365", {"start": v(-19.03, -23.34) * mm, "end": v(-19.75, -22.74) * mm});
            skLineSegment(sketch, "E366", {"start": v(-19.75, -22.74) * mm, "end": v(-19.59, -22.4) * mm});
            skLineSegment(sketch, "E367", {"start": v(-19.59, -22.4) * mm, "end": v(-19.42, -22.06) * mm});
            skLineSegment(sketch, "E368", {"start": v(-19.42, -22.06) * mm, "end": v(-19.23, -21.74) * mm});
            skLineSegment(sketch, "E369", {"start": v(-19.23, -21.74) * mm, "end": v(-19.02, -21.44) * mm});
            skLineSegment(sketch, "E370", {"start": v(-19.02, -21.44) * mm, "end": v(-18.8, -21.15) * mm});
            skLineSegment(sketch, "E371", {"start": v(-18.8, -21.15) * mm, "end": v(-18.7, -20.98) * mm});
            skLineSegment(sketch, "E372", {"start": v(-18.7, -20.98) * mm, "end": v(-18.68, -20.88) * mm});
            skLineSegment(sketch, "E373", {"start": v(-18.68, -20.88) * mm, "end": v(-19.08, -20.4) * mm});
            skLineSegment(sketch, "E374", {"start": v(-19.08, -20.4) * mm, "end": v(-19.59, -20.04) * mm});
            skLineSegment(sketch, "E375", {"start": v(-19.59, -20.04) * mm, "end": v(-19.68, -20.07) * mm});
            skLineSegment(sketch, "E376", {"start": v(-19.68, -20.07) * mm, "end": v(-19.85, -20.16) * mm});
            skLineSegment(sketch, "E377", {"start": v(-19.85, -20.16) * mm, "end": v(-20.12, -20.41) * mm});
            skLineSegment(sketch, "E378", {"start": v(-20.12, -20.41) * mm, "end": v(-20.4, -20.64) * mm});
            skLineSegment(sketch, "E379", {"start": v(-20.4, -20.64) * mm, "end": v(-20.7, -20.85) * mm});
            skLineSegment(sketch, "E380", {"start": v(-20.7, -20.85) * mm, "end": v(-21.03, -21.04) * mm});
            skLineSegment(sketch, "E381", {"start": v(-21.03, -21.04) * mm, "end": v(-21.37, -21.22) * mm});
            skLineSegment(sketch, "E382", {"start": v(-21.37, -21.22) * mm, "end": v(-22.01, -20.55) * mm});
            skLineSegment(sketch, "E383", {"start": v(-22.01, -20.55) * mm, "end": v(-21.82, -20.22) * mm});
            skLineSegment(sketch, "E384", {"start": v(-21.82, -20.22) * mm, "end": v(-21.62, -19.9) * mm});
            skLineSegment(sketch, "E385", {"start": v(-21.62, -19.9) * mm, "end": v(-21.4, -19.6) * mm});
            skLineSegment(sketch, "E386", {"start": v(-21.4, -19.6) * mm, "end": v(-21.16, -19.33) * mm});
            skLineSegment(sketch, "E387", {"start": v(-21.16, -19.33) * mm, "end": v(-20.9, -19.07) * mm});
            skLineSegment(sketch, "E388", {"start": v(-20.9, -19.07) * mm, "end": v(-20.8, -18.91) * mm});
            skLineSegment(sketch, "E389", {"start": v(-20.8, -18.91) * mm, "end": v(-20.76, -18.82) * mm});
            skLineSegment(sketch, "E390", {"start": v(-20.76, -18.82) * mm, "end": v(-21.1, -18.3) * mm});
            skLineSegment(sketch, "E391", {"start": v(-21.1, -18.3) * mm, "end": v(-21.57, -17.88) * mm});
            skLineSegment(sketch, "E392", {"start": v(-21.57, -17.88) * mm, "end": v(-21.67, -17.9) * mm});
            skLineSegment(sketch, "E393", {"start": v(-21.67, -17.9) * mm, "end": v(-21.85, -17.98) * mm});
            skLineSegment(sketch, "E394", {"start": v(-21.85, -17.98) * mm, "end": v(-22.14, -18.2) * mm});
            skLineSegment(sketch, "E395", {"start": v(-22.14, -18.2) * mm, "end": v(-22.45, -18.4) * mm});
            skLineSegment(sketch, "E396", {"start": v(-22.45, -18.4) * mm, "end": v(-22.77, -18.57) * mm});
            skLineSegment(sketch, "E397", {"start": v(-22.77, -18.57) * mm, "end": v(-23.12, -18.73) * mm});
            skLineSegment(sketch, "E398", {"start": v(-23.12, -18.73) * mm, "end": v(-23.47, -18.87) * mm});
            skLineSegment(sketch, "E399", {"start": v(-23.47, -18.87) * mm, "end": v(-24.04, -18.14) * mm});
            skLineSegment(sketch, "E400", {"start": v(-24.04, -18.14) * mm, "end": v(-23.82, -17.83) * mm});
            skLineSegment(sketch, "E401", {"start": v(-23.82, -17.83) * mm, "end": v(-23.58, -17.54) * mm});
            skLineSegment(sketch, "E402", {"start": v(-23.58, -17.54) * mm, "end": v(-23.33, -17.26) * mm});
            skLineSegment(sketch, "E403", {"start": v(-23.33, -17.26) * mm, "end": v(-23.06, -17.01) * mm});
            skLineSegment(sketch, "E404", {"start": v(-23.06, -17.01) * mm, "end": v(-22.78, -16.78) * mm});
            skLineSegment(sketch, "E405", {"start": v(-22.78, -16.78) * mm, "end": v(-22.66, -16.64) * mm});
            skLineSegment(sketch, "E406", {"start": v(-22.66, -16.64) * mm, "end": v(-22.61, -16.54) * mm});
            skLineSegment(sketch, "E407", {"start": v(-22.61, -16.54) * mm, "end": v(-22.9, -15.99) * mm});
            skLineSegment(sketch, "E408", {"start": v(-22.9, -15.99) * mm, "end": v(-23.32, -15.53) * mm});
            skLineSegment(sketch, "E409", {"start": v(-23.32, -15.53) * mm, "end": v(-23.43, -15.54) * mm});
            skLineSegment(sketch, "E410", {"start": v(-23.43, -15.54) * mm, "end": v(-23.6, -15.6) * mm});
            skLineSegment(sketch, "E411", {"start": v(-23.6, -15.6) * mm, "end": v(-23.92, -15.78) * mm});
            skLineSegment(sketch, "E412", {"start": v(-23.92, -15.78) * mm, "end": v(-24.25, -15.95) * mm});
            skLineSegment(sketch, "E413", {"start": v(-24.25, -15.95) * mm, "end": v(-24.6, -16.1) * mm});
            skLineSegment(sketch, "E414", {"start": v(-24.6, -16.1) * mm, "end": v(-24.95, -16.21) * mm});
            skLineSegment(sketch, "E415", {"start": v(-24.95, -16.21) * mm, "end": v(-25.31, -16.32) * mm});
            skLineSegment(sketch, "E416", {"start": v(-25.31, -16.32) * mm, "end": v(-25.8, -15.53) * mm});
            skLineSegment(sketch, "E417", {"start": v(-25.8, -15.53) * mm, "end": v(-25.55, -15.24) * mm});
            skLineSegment(sketch, "E418", {"start": v(-25.55, -15.24) * mm, "end": v(-25.28, -14.98) * mm});
            skLineSegment(sketch, "E419", {"start": v(-25.28, -14.98) * mm, "end": v(-25, -14.73) * mm});
            skLineSegment(sketch, "E420", {"start": v(-25, -14.73) * mm, "end": v(-24.71, -14.51) * mm});
            skLineSegment(sketch, "E421", {"start": v(-24.71, -14.51) * mm, "end": v(-24.4, -14.31) * mm});
            skLineSegment(sketch, "E422", {"start": v(-24.4, -14.31) * mm, "end": v(-24.27, -14.18) * mm});
            skLineSegment(sketch, "E423", {"start": v(-24.27, -14.18) * mm, "end": v(-24.22, -14.09) * mm});
            skLineSegment(sketch, "E424", {"start": v(-24.22, -14.09) * mm, "end": v(-24.45, -13.5) * mm});
            skLineSegment(sketch, "E425", {"start": v(-24.45, -13.5) * mm, "end": v(-24.82, -13) * mm});
            skLineSegment(sketch, "E426", {"start": v(-24.82, -13) * mm, "end": v(-24.92, -13) * mm});
            skLineSegment(sketch, "E427", {"start": v(-24.92, -13) * mm, "end": v(-25.1, -13.04) * mm});
            skLineSegment(sketch, "E428", {"start": v(-25.1, -13.04) * mm, "end": v(-25.44, -13.2) * mm});
            skLineSegment(sketch, "E429", {"start": v(-25.44, -13.2) * mm, "end": v(-25.78, -13.33) * mm});
            skLineSegment(sketch, "E430", {"start": v(-25.78, -13.33) * mm, "end": v(-26.14, -13.43) * mm});
            skLineSegment(sketch, "E431", {"start": v(-26.14, -13.43) * mm, "end": v(-26.5, -13.52) * mm});
            skLineSegment(sketch, "E432", {"start": v(-26.5, -13.52) * mm, "end": v(-26.88, -13.58) * mm});
            skLineSegment(sketch, "E433", {"start": v(-26.88, -13.58) * mm, "end": v(-27.29, -12.74) * mm});
            skLineSegment(sketch, "E434", {"start": v(-27.29, -12.74) * mm, "end": v(-27, -12.5) * mm});
            skLineSegment(sketch, "E435", {"start": v(-27, -12.5) * mm, "end": v(-26.71, -12.25) * mm});
            skLineSegment(sketch, "E436", {"start": v(-26.71, -12.25) * mm, "end": v(-26.4, -12.04) * mm});
            skLineSegment(sketch, "E437", {"start": v(-26.4, -12.04) * mm, "end": v(-26.1, -11.85) * mm});
            skLineSegment(sketch, "E438", {"start": v(-26.1, -11.85) * mm, "end": v(-25.77, -11.68) * mm});
            skLineSegment(sketch, "E439", {"start": v(-25.77, -11.68) * mm, "end": v(-25.62, -11.56) * mm});
            skLineSegment(sketch, "E440", {"start": v(-25.62, -11.56) * mm, "end": v(-25.56, -11.48) * mm});
            skLineSegment(sketch, "E441", {"start": v(-25.56, -11.48) * mm, "end": v(-25.72, -10.88) * mm});
            skLineSegment(sketch, "E442", {"start": v(-25.72, -10.88) * mm, "end": v(-26.04, -10.34) * mm});
            skLineSegment(sketch, "E443", {"start": v(-26.04, -10.34) * mm, "end": v(-26.14, -10.33) * mm});
            skLineSegment(sketch, "E444", {"start": v(-26.14, -10.33) * mm, "end": v(-26.33, -10.35) * mm});
            skLineSegment(sketch, "E445", {"start": v(-26.33, -10.35) * mm, "end": v(-26.68, -10.47) * mm});
            skLineSegment(sketch, "E446", {"start": v(-26.68, -10.47) * mm, "end": v(-27.03, -10.56) * mm});
            skLineSegment(sketch, "E447", {"start": v(-27.03, -10.56) * mm, "end": v(-27.4, -10.63) * mm});
            skLineSegment(sketch, "E448", {"start": v(-27.4, -10.63) * mm, "end": v(-27.77, -10.67) * mm});
            skLineSegment(sketch, "E449", {"start": v(-27.77, -10.67) * mm, "end": v(-28.15, -10.7) * mm});
            skLineSegment(sketch, "E450", {"start": v(-28.15, -10.7) * mm, "end": v(-28.47, -9.82) * mm});
            skLineSegment(sketch, "E451", {"start": v(-28.47, -9.82) * mm, "end": v(-28.16, -9.6) * mm});
            skLineSegment(sketch, "E452", {"start": v(-28.16, -9.6) * mm, "end": v(-27.85, -9.4) * mm});
            skLineSegment(sketch, "E453", {"start": v(-27.85, -9.4) * mm, "end": v(-27.52, -9.2) * mm});
            skLineSegment(sketch, "E454", {"start": v(-27.52, -9.2) * mm, "end": v(-27.19, -9.06) * mm});
            skLineSegment(sketch, "E455", {"start": v(-27.19, -9.06) * mm, "end": v(-26.85, -8.92) * mm});
            skLineSegment(sketch, "E456", {"start": v(-26.85, -8.92) * mm, "end": v(-26.7, -8.82) * mm});
            skLineSegment(sketch, "E457", {"start": v(-26.7, -8.82) * mm, "end": v(-26.62, -8.74) * mm});
            skLineSegment(sketch, "E458", {"start": v(-26.62, -8.74) * mm, "end": v(-26.72, -8.13) * mm});
            skLineSegment(sketch, "E459", {"start": v(-26.72, -8.13) * mm, "end": v(-26.98, -7.56) * mm});
            skLineSegment(sketch, "E460", {"start": v(-26.98, -7.56) * mm, "end": v(-27.08, -7.54) * mm});
            skLineSegment(sketch, "E461", {"start": v(-27.08, -7.54) * mm, "end": v(-27.27, -7.54) * mm});
            skLineSegment(sketch, "E462", {"start": v(-27.27, -7.54) * mm, "end": v(-27.63, -7.62) * mm});
            skLineSegment(sketch, "E463", {"start": v(-27.63, -7.62) * mm, "end": v(-27.99, -7.68) * mm});
            skLineSegment(sketch, "E464", {"start": v(-27.99, -7.68) * mm, "end": v(-28.36, -7.7) * mm});
            skLineSegment(sketch, "E465", {"start": v(-28.36, -7.7) * mm, "end": v(-28.74, -7.7) * mm});
            skLineSegment(sketch, "E466", {"start": v(-28.74, -7.7) * mm, "end": v(-29.12, -7.7) * mm});
            skLineSegment(sketch, "E467", {"start": v(-29.12, -7.7) * mm, "end": v(-29.34, -6.8) * mm});
            skLineSegment(sketch, "E468", {"start": v(-29.34, -6.8) * mm, "end": v(-29.01, -6.6) * mm});
            skLineSegment(sketch, "E469", {"start": v(-29.01, -6.6) * mm, "end": v(-28.68, -6.43) * mm});
            skLineSegment(sketch, "E470", {"start": v(-28.68, -6.43) * mm, "end": v(-28.33, -6.28) * mm});
            skLineSegment(sketch, "E471", {"start": v(-28.33, -6.28) * mm, "end": v(-27.99, -6.16) * mm});
            skLineSegment(sketch, "E472", {"start": v(-27.99, -6.16) * mm, "end": v(-27.63, -6.07) * mm});
            skLineSegment(sketch, "E473", {"start": v(-27.63, -6.07) * mm, "end": v(-27.47, -5.98) * mm});
            skLineSegment(sketch, "E474", {"start": v(-27.47, -5.98) * mm, "end": v(-27.39, -5.91) * mm});
            skLineSegment(sketch, "E475", {"start": v(-27.39, -5.91) * mm, "end": v(-27.42, -5.3) * mm});
            skLineSegment(sketch, "E476", {"start": v(-27.42, -5.3) * mm, "end": v(-27.62, -4.7) * mm});
            skLineSegment(sketch, "E477", {"start": v(-27.62, -4.7) * mm, "end": v(-27.72, -4.67) * mm});
            skLineSegment(sketch, "E478", {"start": v(-27.72, -4.67) * mm, "end": v(-27.9, -4.65) * mm});
            skLineSegment(sketch, "E479", {"start": v(-27.9, -4.65) * mm, "end": v(-28.27, -4.7) * mm});
            skLineSegment(sketch, "E480", {"start": v(-28.27, -4.7) * mm, "end": v(-28.64, -4.7) * mm});
            skLineSegment(sketch, "E481", {"start": v(-28.64, -4.7) * mm, "end": v(-29, -4.7) * mm});
            skLineSegment(sketch, "E482", {"start": v(-29, -4.7) * mm, "end": v(-29.38, -4.66) * mm});
            skLineSegment(sketch, "E483", {"start": v(-29.38, -4.66) * mm, "end": v(-29.76, -4.61) * mm});
            skLineSegment(sketch, "E484", {"start": v(-29.76, -4.61) * mm, "end": v(-29.9, -3.69) * mm});
            skLineSegment(sketch, "E485", {"start": v(-29.9, -3.69) * mm, "end": v(-29.54, -3.53) * mm});
            skLineSegment(sketch, "E486", {"start": v(-29.54, -3.53) * mm, "end": v(-29.2, -3.4) * mm});
            skLineSegment(sketch, "E487", {"start": v(-29.2, -3.4) * mm, "end": v(-28.84, -3.29) * mm});
            skLineSegment(sketch, "E488", {"start": v(-28.84, -3.29) * mm, "end": v(-28.48, -3.2) * mm});
            skLineSegment(sketch, "E489", {"start": v(-28.48, -3.2) * mm, "end": v(-28.12, -3.15) * mm});
            skLineSegment(sketch, "E490", {"start": v(-28.12, -3.15) * mm, "end": v(-27.94, -3.08) * mm});
            skLineSegment(sketch, "E491", {"start": v(-27.94, -3.08) * mm, "end": v(-27.86, -3.02) * mm});
            skLineSegment(sketch, "E492", {"start": v(-27.86, -3.02) * mm, "end": v(-27.83, -2.4) * mm});
            skLineSegment(sketch, "E493", {"start": v(-27.83, -2.4) * mm, "end": v(-27.96, -1.79) * mm});
            skLineSegment(sketch, "E494", {"start": v(-27.96, -1.79) * mm, "end": v(-28.06, -1.74) * mm});
            skLineSegment(sketch, "E495", {"start": v(-28.06, -1.74) * mm, "end": v(-28.24, -1.7) * mm});
            skLineSegment(sketch, "E496", {"start": v(-28.24, -1.7) * mm, "end": v(-28.6, -1.7) * mm});
            skLineSegment(sketch, "E497", {"start": v(-28.6, -1.7) * mm, "end": v(-28.97, -1.7) * mm});
            skLineSegment(sketch, "E498", {"start": v(-28.97, -1.7) * mm, "end": v(-29.34, -1.64) * mm});
            skLineSegment(sketch, "E499", {"start": v(-29.34, -1.64) * mm, "end": v(-29.71, -1.57) * mm});
            skLineSegment(sketch, "E500", {"start": v(-29.71, -1.57) * mm, "end": v(-30.08, -1.47) * mm});
            skLineSegment(sketch, "E501", {"start": v(-30.08, -1.47) * mm, "end": v(-30.11, -0.54) * mm});
            skLineSegment(sketch, "E502", {"start": v(-30.11, -0.54) * mm, "end": v(-29.75, -0.43) * mm});
            skLineSegment(sketch, "E503", {"start": v(-29.75, -0.43) * mm, "end": v(-29.39, -0.33) * mm});
            skLineSegment(sketch, "E504", {"start": v(-29.39, -0.33) * mm, "end": v(-29.02, -0.25) * mm});
            skLineSegment(sketch, "E505", {"start": v(-29.02, -0.25) * mm, "end": v(-28.66, -0.21) * mm});
            skLineSegment(sketch, "E506", {"start": v(-28.66, -0.21) * mm, "end": v(-28.3, -0.19) * mm});
            skLineSegment(sketch, "E507", {"start": v(-28.3, -0.19) * mm, "end": v(-28.11, -0.14) * mm});
            skLineSegment(sketch, "E508", {"start": v(-28.11, -0.14) * mm, "end": v(-28.02, -0.1) * mm});
            skLineSegment(sketch, "E509", {"start": v(-28.02, -0.1) * mm, "end": v(-27.92, 0.53) * mm});
            skLineSegment(sketch, "E510", {"start": v(-27.92, 0.53) * mm, "end": v(-28, 1.15) * mm});
            skLineSegment(sketch, "E511", {"start": v(-28, 1.15) * mm, "end": v(-28.09, 1.2) * mm});
            skLineSegment(sketch, "E512", {"start": v(-28.09, 1.2) * mm, "end": v(-28.27, 1.26) * mm});
            skLineSegment(sketch, "E513", {"start": v(-28.27, 1.26) * mm, "end": v(-28.63, 1.3) * mm});
            skLineSegment(sketch, "E514", {"start": v(-28.63, 1.3) * mm, "end": v(-29, 1.35) * mm});
            skLineSegment(sketch, "E515", {"start": v(-29, 1.35) * mm, "end": v(-29.35, 1.44) * mm});
            skLineSegment(sketch, "E516", {"start": v(-29.35, 1.44) * mm, "end": v(-29.71, 1.55) * mm});
            skLineSegment(sketch, "E517", {"start": v(-29.71, 1.55) * mm, "end": v(-30.07, 1.68) * mm});
            skLineSegment(sketch, "E518", {"start": v(-30.07, 1.68) * mm, "end": v(-30, 2.6) * mm});
            skLineSegment(sketch, "E519", {"start": v(-30, 2.6) * mm, "end": v(-29.63, 2.69) * mm});
            skLineSegment(sketch, "E520", {"start": v(-29.63, 2.69) * mm, "end": v(-29.26, 2.74) * mm});
            skLineSegment(sketch, "E521", {"start": v(-29.26, 2.74) * mm, "end": v(-28.89, 2.78) * mm});
            skLineSegment(sketch, "E522", {"start": v(-28.89, 2.78) * mm, "end": v(-28.52, 2.79) * mm});
            skLineSegment(sketch, "E523", {"start": v(-28.52, 2.79) * mm, "end": v(-28.16, 2.77) * mm});
            skLineSegment(sketch, "E524", {"start": v(-28.16, 2.77) * mm, "end": v(-27.97, 2.8) * mm});
            skLineSegment(sketch, "E525", {"start": v(-27.97, 2.8) * mm, "end": v(-27.88, 2.84) * mm});
            skLineSegment(sketch, "E526", {"start": v(-27.88, 2.84) * mm, "end": v(-27.72, 3.44) * mm});
            skLineSegment(sketch, "E527", {"start": v(-27.72, 3.44) * mm, "end": v(-27.72, 4.07) * mm});
            skLineSegment(sketch, "E528", {"start": v(-27.72, 4.07) * mm, "end": v(-27.8, 4.13) * mm});
            skLineSegment(sketch, "E529", {"start": v(-27.8, 4.13) * mm, "end": v(-27.98, 4.2) * mm});
            skLineSegment(sketch, "E530", {"start": v(-27.98, 4.2) * mm, "end": v(-28.34, 4.28) * mm});
            skLineSegment(sketch, "E531", {"start": v(-28.34, 4.28) * mm, "end": v(-28.7, 4.37) * mm});
            skLineSegment(sketch, "E532", {"start": v(-28.7, 4.37) * mm, "end": v(-29.04, 4.5) * mm});
            skLineSegment(sketch, "E533", {"start": v(-29.04, 4.5) * mm, "end": v(-29.39, 4.65) * mm});
            skLineSegment(sketch, "E534", {"start": v(-29.39, 4.65) * mm, "end": v(-29.73, 4.81) * mm});
            skLineSegment(sketch, "E535", {"start": v(-29.73, 4.81) * mm, "end": v(-29.57, 5.73) * mm});
            skLineSegment(sketch, "E536", {"start": v(-29.57, 5.73) * mm, "end": v(-29.19, 5.77) * mm});
            skLineSegment(sketch, "E537", {"start": v(-29.19, 5.77) * mm, "end": v(-28.81, 5.79) * mm});
            skLineSegment(sketch, "E538", {"start": v(-28.81, 5.79) * mm, "end": v(-28.44, 5.79) * mm});
            skLineSegment(sketch, "E539", {"start": v(-28.44, 5.79) * mm, "end": v(-28.07, 5.75) * mm});
            skLineSegment(sketch, "E540", {"start": v(-28.07, 5.75) * mm, "end": v(-27.71, 5.7) * mm});
            skLineSegment(sketch, "E541", {"start": v(-27.71, 5.7) * mm, "end": v(-27.52, 5.7) * mm});
            skLineSegment(sketch, "E542", {"start": v(-27.52, 5.7) * mm, "end": v(-27.43, 5.74) * mm});
            skLineSegment(sketch, "E543", {"start": v(-27.43, 5.74) * mm, "end": v(-27.2, 6.32) * mm});
            skLineSegment(sketch, "E544", {"start": v(-27.2, 6.32) * mm, "end": v(-27.15, 6.94) * mm});
            skLineSegment(sketch, "E545", {"start": v(-27.15, 6.94) * mm, "end": v(-27.22, 7.01) * mm});
            skLineSegment(sketch, "E546", {"start": v(-27.22, 7.01) * mm, "end": v(-27.39, 7.1) * mm});
            skLineSegment(sketch, "E547", {"start": v(-27.39, 7.1) * mm, "end": v(-27.74, 7.21) * mm});
            skLineSegment(sketch, "E548", {"start": v(-27.74, 7.21) * mm, "end": v(-28.08, 7.35) * mm});
            skLineSegment(sketch, "E549", {"start": v(-28.08, 7.35) * mm, "end": v(-28.41, 7.5) * mm});
            skLineSegment(sketch, "E550", {"start": v(-28.41, 7.5) * mm, "end": v(-28.74, 7.7) * mm});
            skLineSegment(sketch, "E551", {"start": v(-28.74, 7.7) * mm, "end": v(-29.06, 7.9) * mm});
            skLineSegment(sketch, "E552", {"start": v(-29.06, 7.9) * mm, "end": v(-28.8, 8.79) * mm});
            skLineSegment(sketch, "E553", {"start": v(-28.8, 8.79) * mm, "end": v(-28.43, 8.79) * mm});
            skLineSegment(sketch, "E554", {"start": v(-28.43, 8.79) * mm, "end": v(-28.05, 8.77) * mm});
            skLineSegment(sketch, "E555", {"start": v(-28.05, 8.77) * mm, "end": v(-27.68, 8.73) * mm});
            skLineSegment(sketch, "E556", {"start": v(-27.68, 8.73) * mm, "end": v(-27.32, 8.66) * mm});
            skLineSegment(sketch, "E557", {"start": v(-27.32, 8.66) * mm, "end": v(-26.97, 8.56) * mm});
            skLineSegment(sketch, "E558", {"start": v(-26.97, 8.56) * mm, "end": v(-26.78, 8.55) * mm});
            skLineSegment(sketch, "E559", {"start": v(-26.78, 8.55) * mm, "end": v(-26.68, 8.57) * mm});
            skLineSegment(sketch, "E560", {"start": v(-26.68, 8.57) * mm, "end": v(-26.4, 9.13) * mm});
            skLineSegment(sketch, "E561", {"start": v(-26.4, 9.13) * mm, "end": v(-26.27, 9.74) * mm});
            skLineSegment(sketch, "E562", {"start": v(-26.27, 9.74) * mm, "end": v(-26.34, 9.82) * mm});
            skLineSegment(sketch, "E563", {"start": v(-26.34, 9.82) * mm, "end": v(-26.5, 9.93) * mm});
            skLineSegment(sketch, "E564", {"start": v(-26.5, 9.93) * mm, "end": v(-26.83, 10.07) * mm});
            skLineSegment(sketch, "E565", {"start": v(-26.83, 10.07) * mm, "end": v(-27.16, 10.24) * mm});
            skLineSegment(sketch, "E566", {"start": v(-27.16, 10.24) * mm, "end": v(-27.47, 10.44) * mm});
            skLineSegment(sketch, "E567", {"start": v(-27.47, 10.44) * mm, "end": v(-27.78, 10.65) * mm});
            skLineSegment(sketch, "E568", {"start": v(-27.78, 10.65) * mm, "end": v(-28.08, 10.89) * mm});
            skLineSegment(sketch, "E569", {"start": v(-28.08, 10.89) * mm, "end": v(-27.73, 11.75) * mm});
            skLineSegment(sketch, "E570", {"start": v(-27.73, 11.75) * mm, "end": v(-27.35, 11.71) * mm});
            skLineSegment(sketch, "E571", {"start": v(-27.35, 11.71) * mm, "end": v(-26.98, 11.65) * mm});
            skLineSegment(sketch, "E572", {"start": v(-26.98, 11.65) * mm, "end": v(-26.62, 11.57) * mm});
            skLineSegment(sketch, "E573", {"start": v(-26.62, 11.57) * mm, "end": v(-26.27, 11.46) * mm});
            skLineSegment(sketch, "E574", {"start": v(-26.27, 11.46) * mm, "end": v(-25.92, 11.33) * mm});
            skLineSegment(sketch, "E575", {"start": v(-25.92, 11.33) * mm, "end": v(-25.74, 11.3) * mm});
            skLineSegment(sketch, "E576", {"start": v(-25.74, 11.3) * mm, "end": v(-25.63, 11.31) * mm});
            skLineSegment(sketch, "E577", {"start": v(-25.63, 11.31) * mm, "end": v(-25.3, 11.84) * mm});
            skLineSegment(sketch, "E578", {"start": v(-25.3, 11.84) * mm, "end": v(-25.1, 12.43) * mm});
            skLineSegment(sketch, "E579", {"start": v(-25.1, 12.43) * mm, "end": v(-25.17, 12.52) * mm});
            skLineSegment(sketch, "E580", {"start": v(-25.17, 12.52) * mm, "end": v(-25.31, 12.64) * mm});
            skLineSegment(sketch, "E581", {"start": v(-25.31, 12.64) * mm, "end": v(-25.63, 12.82) * mm});
            skLineSegment(sketch, "E582", {"start": v(-25.63, 12.82) * mm, "end": v(-25.94, 13.02) * mm});
            skLineSegment(sketch, "E583", {"start": v(-25.94, 13.02) * mm, "end": v(-26.23, 13.25) * mm});
            skLineSegment(sketch, "E584", {"start": v(-26.23, 13.25) * mm, "end": v(-26.51, 13.5) * mm});
            skLineSegment(sketch, "E585", {"start": v(-26.51, 13.5) * mm, "end": v(-26.79, 13.76) * mm});
            skLineSegment(sketch, "E586", {"start": v(-26.79, 13.76) * mm, "end": v(-26.35, 14.59) * mm});
            skLineSegment(sketch, "E587", {"start": v(-26.35, 14.59) * mm, "end": v(-25.98, 14.5) * mm});
            skLineSegment(sketch, "E588", {"start": v(-25.98, 14.5) * mm, "end": v(-25.61, 14.4) * mm});
            skLineSegment(sketch, "E589", {"start": v(-25.61, 14.4) * mm, "end": v(-25.26, 14.3) * mm});
            skLineSegment(sketch, "E590", {"start": v(-25.26, 14.3) * mm, "end": v(-24.92, 14.15) * mm});
            skLineSegment(sketch, "E591", {"start": v(-24.92, 14.15) * mm, "end": v(-24.6, 13.98) * mm});
            skLineSegment(sketch, "E592", {"start": v(-24.6, 13.98) * mm, "end": v(-24.41, 13.93) * mm});
            skLineSegment(sketch, "E593", {"start": v(-24.41, 13.93) * mm, "end": v(-24.31, 13.93) * mm});
            skLineSegment(sketch, "E594", {"start": v(-24.31, 13.93) * mm, "end": v(-23.92, 14.42) * mm});
            skLineSegment(sketch, "E595", {"start": v(-23.92, 14.42) * mm, "end": v(-23.67, 15) * mm});
            skLineSegment(sketch, "E596", {"start": v(-23.67, 15) * mm, "end": v(-23.72, 15.08) * mm});
            skLineSegment(sketch, "E597", {"start": v(-23.72, 15.08) * mm, "end": v(-23.85, 15.22) * mm});
            skLineSegment(sketch, "E598", {"start": v(-23.85, 15.22) * mm, "end": v(-24.15, 15.43) * mm});
            skLineSegment(sketch, "E599", {"start": v(-24.15, 15.43) * mm, "end": v(-24.43, 15.66) * mm});
            skLineSegment(sketch, "E600", {"start": v(-24.43, 15.66) * mm, "end": v(-24.7, 15.92) * mm});
            skLineSegment(sketch, "E601", {"start": v(-24.7, 15.92) * mm, "end": v(-24.96, 16.2) * mm});
            skLineSegment(sketch, "E602", {"start": v(-24.96, 16.2) * mm, "end": v(-25.2, 16.49) * mm});
            skLineSegment(sketch, "E603", {"start": v(-25.2, 16.49) * mm, "end": v(-24.68, 17.26) * mm});
            skLineSegment(sketch, "E604", {"start": v(-24.68, 17.26) * mm, "end": v(-24.32, 17.14) * mm});
            skLineSegment(sketch, "E605", {"start": v(-24.32, 17.14) * mm, "end": v(-23.97, 17) * mm});
            skLineSegment(sketch, "E606", {"start": v(-23.97, 17) * mm, "end": v(-23.63, 16.85) * mm});
            skLineSegment(sketch, "E607", {"start": v(-23.63, 16.85) * mm, "end": v(-23.3, 16.67) * mm});
            skLineSegment(sketch, "E608", {"start": v(-23.3, 16.67) * mm, "end": v(-23, 16.48) * mm});
            skLineSegment(sketch, "E609", {"start": v(-23, 16.48) * mm, "end": v(-22.82, 16.41) * mm});
            skLineSegment(sketch, "E610", {"start": v(-22.82, 16.41) * mm, "end": v(-22.72, 16.4) * mm});
            skLineSegment(sketch, "E611", {"start": v(-22.72, 16.4) * mm, "end": v(-22.28, 16.84) * mm});
            skLineSegment(sketch, "E612", {"start": v(-22.28, 16.84) * mm, "end": v(-21.98, 17.38) * mm});
            skLineSegment(sketch, "E613", {"start": v(-21.98, 17.38) * mm, "end": v(-22.02, 17.48) * mm});
            skLineSegment(sketch, "E614", {"start": v(-22.02, 17.48) * mm, "end": v(-22.13, 17.63) * mm});
            skLineSegment(sketch, "E615", {"start": v(-22.13, 17.63) * mm, "end": v(-22.4, 17.87) * mm});
            skLineSegment(sketch, "E616", {"start": v(-22.4, 17.87) * mm, "end": v(-22.66, 18.13) * mm});
            skLineSegment(sketch, "E617", {"start": v(-22.66, 18.13) * mm, "end": v(-22.9, 18.42) * mm});
            skLineSegment(sketch, "E618", {"start": v(-22.9, 18.42) * mm, "end": v(-23.13, 18.72) * mm});
            skLineSegment(sketch, "E619", {"start": v(-23.13, 18.72) * mm, "end": v(-23.34, 19.03) * mm});
            skLineSegment(sketch, "E620", {"start": v(-23.34, 19.03) * mm, "end": v(-22.74, 19.75) * mm});
            skLineSegment(sketch, "E621", {"start": v(-22.74, 19.75) * mm, "end": v(-22.4, 19.59) * mm});
            skLineSegment(sketch, "E622", {"start": v(-22.4, 19.59) * mm, "end": v(-22.06, 19.42) * mm});
            skLineSegment(sketch, "E623", {"start": v(-22.06, 19.42) * mm, "end": v(-21.74, 19.23) * mm});
            skLineSegment(sketch, "E624", {"start": v(-21.74, 19.23) * mm, "end": v(-21.44, 19.02) * mm});
            skLineSegment(sketch, "E625", {"start": v(-21.44, 19.02) * mm, "end": v(-21.15, 18.8) * mm});
            skLineSegment(sketch, "E626", {"start": v(-21.15, 18.8) * mm, "end": v(-20.98, 18.7) * mm});
            skLineSegment(sketch, "E627", {"start": v(-20.98, 18.7) * mm, "end": v(-20.88, 18.68) * mm});
            skLineSegment(sketch, "E628", {"start": v(-20.88, 18.68) * mm, "end": v(-20.4, 19.08) * mm});
            skLineSegment(sketch, "E629", {"start": v(-20.4, 19.08) * mm, "end": v(-20.04, 19.59) * mm});
            skLineSegment(sketch, "E630", {"start": v(-20.04, 19.59) * mm, "end": v(-20.07, 19.68) * mm});
            skLineSegment(sketch, "E631", {"start": v(-20.07, 19.68) * mm, "end": v(-20.16, 19.85) * mm});
            skLineSegment(sketch, "E632", {"start": v(-20.16, 19.85) * mm, "end": v(-20.41, 20.12) * mm});
            skLineSegment(sketch, "E633", {"start": v(-20.41, 20.12) * mm, "end": v(-20.64, 20.4) * mm});
            skLineSegment(sketch, "E634", {"start": v(-20.64, 20.4) * mm, "end": v(-20.85, 20.7) * mm});
            skLineSegment(sketch, "E635", {"start": v(-20.85, 20.7) * mm, "end": v(-21.04, 21.03) * mm});
            skLineSegment(sketch, "E636", {"start": v(-21.04, 21.03) * mm, "end": v(-21.22, 21.37) * mm});
            skLineSegment(sketch, "E637", {"start": v(-21.22, 21.37) * mm, "end": v(-20.55, 22.01) * mm});
            skLineSegment(sketch, "E638", {"start": v(-20.55, 22.01) * mm, "end": v(-20.22, 21.82) * mm});
            skLineSegment(sketch, "E639", {"start": v(-20.22, 21.82) * mm, "end": v(-19.9, 21.62) * mm});
            skLineSegment(sketch, "E640", {"start": v(-19.9, 21.62) * mm, "end": v(-19.6, 21.4) * mm});
            skLineSegment(sketch, "E641", {"start": v(-19.6, 21.4) * mm, "end": v(-19.33, 21.16) * mm});
            skLineSegment(sketch, "E642", {"start": v(-19.33, 21.16) * mm, "end": v(-19.07, 20.9) * mm});
            skLineSegment(sketch, "E643", {"start": v(-19.07, 20.9) * mm, "end": v(-18.91, 20.8) * mm});
            skLineSegment(sketch, "E644", {"start": v(-18.91, 20.8) * mm, "end": v(-18.82, 20.76) * mm});
            skLineSegment(sketch, "E645", {"start": v(-18.82, 20.76) * mm, "end": v(-18.3, 21.1) * mm});
            skLineSegment(sketch, "E646", {"start": v(-18.3, 21.1) * mm, "end": v(-17.88, 21.57) * mm});
            skLineSegment(sketch, "E647", {"start": v(-17.88, 21.57) * mm, "end": v(-17.9, 21.67) * mm});
            skLineSegment(sketch, "E648", {"start": v(-17.9, 21.67) * mm, "end": v(-17.98, 21.85) * mm});
            skLineSegment(sketch, "E649", {"start": v(-17.98, 21.85) * mm, "end": v(-18.2, 22.14) * mm});
            skLineSegment(sketch, "E650", {"start": v(-18.2, 22.14) * mm, "end": v(-18.4, 22.45) * mm});
            skLineSegment(sketch, "E651", {"start": v(-18.4, 22.45) * mm, "end": v(-18.57, 22.77) * mm});
            skLineSegment(sketch, "E652", {"start": v(-18.57, 22.77) * mm, "end": v(-18.73, 23.12) * mm});
            skLineSegment(sketch, "E653", {"start": v(-18.73, 23.12) * mm, "end": v(-18.87, 23.47) * mm});
            skLineSegment(sketch, "E654", {"start": v(-18.87, 23.47) * mm, "end": v(-18.14, 24.04) * mm});
            skLineSegment(sketch, "E655", {"start": v(-18.14, 24.04) * mm, "end": v(-17.83, 23.82) * mm});
            skLineSegment(sketch, "E656", {"start": v(-17.83, 23.82) * mm, "end": v(-17.54, 23.58) * mm});
            skLineSegment(sketch, "E657", {"start": v(-17.54, 23.58) * mm, "end": v(-17.26, 23.33) * mm});
            skLineSegment(sketch, "E658", {"start": v(-17.26, 23.33) * mm, "end": v(-17.01, 23.06) * mm});
            skLineSegment(sketch, "E659", {"start": v(-17.01, 23.06) * mm, "end": v(-16.78, 22.78) * mm});
            skLineSegment(sketch, "E660", {"start": v(-16.78, 22.78) * mm, "end": v(-16.64, 22.66) * mm});
            skLineSegment(sketch, "E661", {"start": v(-16.64, 22.66) * mm, "end": v(-16.54, 22.61) * mm});
            skLineSegment(sketch, "E662", {"start": v(-16.54, 22.61) * mm, "end": v(-15.99, 22.9) * mm});
            skLineSegment(sketch, "E663", {"start": v(-15.99, 22.9) * mm, "end": v(-15.53, 23.32) * mm});
            skLineSegment(sketch, "E664", {"start": v(-15.53, 23.32) * mm, "end": v(-15.54, 23.43) * mm});
            skLineSegment(sketch, "E665", {"start": v(-15.54, 23.43) * mm, "end": v(-15.6, 23.6) * mm});
            skLineSegment(sketch, "E666", {"start": v(-15.6, 23.6) * mm, "end": v(-15.78, 23.92) * mm});
            skLineSegment(sketch, "E667", {"start": v(-15.78, 23.92) * mm, "end": v(-15.95, 24.25) * mm});
            skLineSegment(sketch, "E668", {"start": v(-15.95, 24.25) * mm, "end": v(-16.1, 24.6) * mm});
            skLineSegment(sketch, "E669", {"start": v(-16.1, 24.6) * mm, "end": v(-16.21, 24.95) * mm});
            skLineSegment(sketch, "E670", {"start": v(-16.21, 24.95) * mm, "end": v(-16.32, 25.31) * mm});
            skLineSegment(sketch, "E671", {"start": v(-16.32, 25.31) * mm, "end": v(-15.53, 25.8) * mm});
            skLineSegment(sketch, "E672", {"start": v(-15.53, 25.8) * mm, "end": v(-15.24, 25.55) * mm});
            skLineSegment(sketch, "E673", {"start": v(-15.24, 25.55) * mm, "end": v(-14.98, 25.28) * mm});
            skLineSegment(sketch, "E674", {"start": v(-14.98, 25.28) * mm, "end": v(-14.73, 25) * mm});
            skLineSegment(sketch, "E675", {"start": v(-14.73, 25) * mm, "end": v(-14.51, 24.71) * mm});
            skLineSegment(sketch, "E676", {"start": v(-14.51, 24.71) * mm, "end": v(-14.31, 24.4) * mm});
            skLineSegment(sketch, "E677", {"start": v(-14.31, 24.4) * mm, "end": v(-14.18, 24.27) * mm});
            skLineSegment(sketch, "E678", {"start": v(-14.18, 24.27) * mm, "end": v(-14.09, 24.22) * mm});
            skLineSegment(sketch, "E679", {"start": v(-14.09, 24.22) * mm, "end": v(-13.5, 24.45) * mm});
            skLineSegment(sketch, "E680", {"start": v(-13.5, 24.45) * mm, "end": v(-13, 24.82) * mm});
            skLineSegment(sketch, "E681", {"start": v(-13, 24.82) * mm, "end": v(-13, 24.92) * mm});
            skLineSegment(sketch, "E682", {"start": v(-13, 24.92) * mm, "end": v(-13.04, 25.1) * mm});
            skLineSegment(sketch, "E683", {"start": v(-13.04, 25.1) * mm, "end": v(-13.2, 25.44) * mm});
            skLineSegment(sketch, "E684", {"start": v(-13.2, 25.44) * mm, "end": v(-13.33, 25.78) * mm});
            skLineSegment(sketch, "E685", {"start": v(-13.33, 25.78) * mm, "end": v(-13.43, 26.14) * mm});
            skLineSegment(sketch, "E686", {"start": v(-13.43, 26.14) * mm, "end": v(-13.52, 26.5) * mm});
            skLineSegment(sketch, "E687", {"start": v(-13.52, 26.5) * mm, "end": v(-13.58, 26.88) * mm});
            skLineSegment(sketch, "E688", {"start": v(-13.58, 26.88) * mm, "end": v(-12.74, 27.29) * mm});
            skLineSegment(sketch, "E689", {"start": v(-12.74, 27.29) * mm, "end": v(-12.5, 27) * mm});
            skLineSegment(sketch, "E690", {"start": v(-12.5, 27) * mm, "end": v(-12.25, 26.71) * mm});
            skLineSegment(sketch, "E691", {"start": v(-12.25, 26.71) * mm, "end": v(-12.04, 26.4) * mm});
            skLineSegment(sketch, "E692", {"start": v(-12.04, 26.4) * mm, "end": v(-11.85, 26.1) * mm});
            skLineSegment(sketch, "E693", {"start": v(-11.85, 26.1) * mm, "end": v(-11.68, 25.77) * mm});
            skLineSegment(sketch, "E694", {"start": v(-11.68, 25.77) * mm, "end": v(-11.56, 25.62) * mm});
            skLineSegment(sketch, "E695", {"start": v(-11.56, 25.62) * mm, "end": v(-11.48, 25.56) * mm});
            skLineSegment(sketch, "E696", {"start": v(-11.48, 25.56) * mm, "end": v(-10.88, 25.72) * mm});
            skLineSegment(sketch, "E697", {"start": v(-10.88, 25.72) * mm, "end": v(-10.34, 26.04) * mm});
            skLineSegment(sketch, "E698", {"start": v(-10.34, 26.04) * mm, "end": v(-10.33, 26.14) * mm});
            skLineSegment(sketch, "E699", {"start": v(-10.33, 26.14) * mm, "end": v(-10.35, 26.33) * mm});
            skLineSegment(sketch, "E700", {"start": v(-10.35, 26.33) * mm, "end": v(-10.47, 26.68) * mm});
            skLineSegment(sketch, "E701", {"start": v(-10.47, 26.68) * mm, "end": v(-10.56, 27.03) * mm});
            skLineSegment(sketch, "E702", {"start": v(-10.56, 27.03) * mm, "end": v(-10.63, 27.4) * mm});
            skLineSegment(sketch, "E703", {"start": v(-10.63, 27.4) * mm, "end": v(-10.67, 27.77) * mm});
            skLineSegment(sketch, "E704", {"start": v(-10.67, 27.77) * mm, "end": v(-10.7, 28.15) * mm});
            skLineSegment(sketch, "E705", {"start": v(-10.7, 28.15) * mm, "end": v(-9.82, 28.47) * mm});
            skLineSegment(sketch, "E706", {"start": v(-9.82, 28.47) * mm, "end": v(-9.6, 28.16) * mm});
            skLineSegment(sketch, "E707", {"start": v(-9.6, 28.16) * mm, "end": v(-9.4, 27.85) * mm});
            skLineSegment(sketch, "E708", {"start": v(-9.4, 27.85) * mm, "end": v(-9.2, 27.52) * mm});
            skLineSegment(sketch, "E709", {"start": v(-9.2, 27.52) * mm, "end": v(-9.06, 27.19) * mm});
            skLineSegment(sketch, "E710", {"start": v(-9.06, 27.19) * mm, "end": v(-8.92, 26.85) * mm});
            skLineSegment(sketch, "E711", {"start": v(-8.92, 26.85) * mm, "end": v(-8.82, 26.7) * mm});
            skLineSegment(sketch, "E712", {"start": v(-8.82, 26.7) * mm, "end": v(-8.74, 26.62) * mm});
            skLineSegment(sketch, "E713", {"start": v(-8.74, 26.62) * mm, "end": v(-8.13, 26.72) * mm});
            skLineSegment(sketch, "E714", {"start": v(-8.13, 26.72) * mm, "end": v(-7.56, 26.98) * mm});
            skLineSegment(sketch, "E715", {"start": v(-7.56, 26.98) * mm, "end": v(-7.54, 27.08) * mm});
            skLineSegment(sketch, "E716", {"start": v(-7.54, 27.08) * mm, "end": v(-7.54, 27.27) * mm});
            skLineSegment(sketch, "E717", {"start": v(-7.54, 27.27) * mm, "end": v(-7.62, 27.63) * mm});
            skLineSegment(sketch, "E718", {"start": v(-7.62, 27.63) * mm, "end": v(-7.68, 27.99) * mm});
            skLineSegment(sketch, "E719", {"start": v(-7.68, 27.99) * mm, "end": v(-7.7, 28.36) * mm});
            skLineSegment(sketch, "E720", {"start": v(-7.7, 28.36) * mm, "end": v(-7.7, 28.74) * mm});
            skLineSegment(sketch, "E721", {"start": v(-7.7, 28.74) * mm, "end": v(-7.7, 29.12) * mm});
            skLineSegment(sketch, "E722", {"start": v(-7.7, 29.12) * mm, "end": v(-6.8, 29.34) * mm});
            skLineSegment(sketch, "E723", {"start": v(-6.8, 29.34) * mm, "end": v(-6.6, 29.01) * mm});
            skLineSegment(sketch, "E724", {"start": v(-6.6, 29.01) * mm, "end": v(-6.43, 28.68) * mm});
            skLineSegment(sketch, "E725", {"start": v(-6.43, 28.68) * mm, "end": v(-6.28, 28.33) * mm});
            skLineSegment(sketch, "E726", {"start": v(-6.28, 28.33) * mm, "end": v(-6.16, 27.99) * mm});
            skLineSegment(sketch, "E727", {"start": v(-6.16, 27.99) * mm, "end": v(-6.07, 27.63) * mm});
            skLineSegment(sketch, "E728", {"start": v(-6.07, 27.63) * mm, "end": v(-5.98, 27.47) * mm});
            skLineSegment(sketch, "E729", {"start": v(-5.98, 27.47) * mm, "end": v(-5.91, 27.39) * mm});
            skLineSegment(sketch, "E730", {"start": v(-5.91, 27.39) * mm, "end": v(-5.3, 27.42) * mm});
            skLineSegment(sketch, "E731", {"start": v(-5.3, 27.42) * mm, "end": v(-4.7, 27.62) * mm});
            skLineSegment(sketch, "E732", {"start": v(-4.7, 27.62) * mm, "end": v(-4.67, 27.72) * mm});
            skLineSegment(sketch, "E733", {"start": v(-4.67, 27.72) * mm, "end": v(-4.65, 27.9) * mm});
            skLineSegment(sketch, "E734", {"start": v(-4.65, 27.9) * mm, "end": v(-4.7, 28.27) * mm});
            skLineSegment(sketch, "E735", {"start": v(-4.7, 28.27) * mm, "end": v(-4.7, 28.64) * mm});
            skLineSegment(sketch, "E736", {"start": v(-4.7, 28.64) * mm, "end": v(-4.7, 29) * mm});
            skLineSegment(sketch, "E737", {"start": v(-4.7, 29) * mm, "end": v(-4.66, 29.38) * mm});
            skLineSegment(sketch, "E738", {"start": v(-4.66, 29.38) * mm, "end": v(-4.61, 29.76) * mm});
            skLineSegment(sketch, "E739", {"start": v(-4.61, 29.76) * mm, "end": v(-3.69, 29.9) * mm});
            skLineSegment(sketch, "E740", {"start": v(-3.69, 29.9) * mm, "end": v(-3.53, 29.54) * mm});
            skLineSegment(sketch, "E741", {"start": v(-3.53, 29.54) * mm, "end": v(-3.4, 29.2) * mm});
            skLineSegment(sketch, "E742", {"start": v(-3.4, 29.2) * mm, "end": v(-3.29, 28.84) * mm});
            skLineSegment(sketch, "E743", {"start": v(-3.29, 28.84) * mm, "end": v(-3.2, 28.48) * mm});
            skLineSegment(sketch, "E744", {"start": v(-3.2, 28.48) * mm, "end": v(-3.15, 28.12) * mm});
            skLineSegment(sketch, "E745", {"start": v(-3.15, 28.12) * mm, "end": v(-3.08, 27.94) * mm});
            skLineSegment(sketch, "E746", {"start": v(-3.08, 27.94) * mm, "end": v(-3.02, 27.86) * mm});
            skLineSegment(sketch, "E747", {"start": v(-3.02, 27.86) * mm, "end": v(-2.4, 27.83) * mm});
            skLineSegment(sketch, "E748", {"start": v(-2.4, 27.83) * mm, "end": v(-1.79, 27.96) * mm});
            skLineSegment(sketch, "E749", {"start": v(-1.79, 27.96) * mm, "end": v(-1.74, 28.06) * mm});
            skLineSegment(sketch, "E750", {"start": v(-1.74, 28.06) * mm, "end": v(-1.7, 28.24) * mm});
            skLineSegment(sketch, "E751", {"start": v(-1.7, 28.24) * mm, "end": v(-1.7, 28.6) * mm});
            skLineSegment(sketch, "E752", {"start": v(-1.7, 28.6) * mm, "end": v(-1.7, 28.97) * mm});
            skLineSegment(sketch, "E753", {"start": v(-1.7, 28.97) * mm, "end": v(-1.64, 29.34) * mm});
            skLineSegment(sketch, "E754", {"start": v(-1.64, 29.34) * mm, "end": v(-1.57, 29.71) * mm});
            skLineSegment(sketch, "E755", {"start": v(-1.57, 29.71) * mm, "end": v(-1.47, 30.08) * mm});
            skLineSegment(sketch, "E756", {"start": v(-1.47, 30.08) * mm, "end": v(-0.54, 30.11) * mm});
            skLineSegment(sketch, "E757", {"start": v(-0.54, 30.11) * mm, "end": v(-0.43, 29.75) * mm});
            skLineSegment(sketch, "E758", {"start": v(-0.43, 29.75) * mm, "end": v(-0.33, 29.39) * mm});
            skLineSegment(sketch, "E759", {"start": v(-0.33, 29.39) * mm, "end": v(-0.25, 29.02) * mm});
            skLineSegment(sketch, "E760", {"start": v(-0.25, 29.02) * mm, "end": v(-0.21, 28.66) * mm});
            skLineSegment(sketch, "E761", {"start": v(-0.21, 28.66) * mm, "end": v(-0.19, 28.3) * mm});
            skLineSegment(sketch, "E762", {"start": v(-0.19, 28.3) * mm, "end": v(-0.14, 28.11) * mm});
            skLineSegment(sketch, "E763", {"start": v(-0.14, 28.11) * mm, "end": v(-0.1, 28.02) * mm});
            skLineSegment(sketch, "E764", {"start": v(-0.1, 28.02) * mm, "end": v(0.53, 27.92) * mm});
            skLineSegment(sketch, "E765", {"start": v(0.53, 27.92) * mm, "end": v(1.15, 28) * mm});
            skLineSegment(sketch, "E766", {"start": v(1.15, 28) * mm, "end": v(1.2, 28.09) * mm});
            skLineSegment(sketch, "E767", {"start": v(1.2, 28.09) * mm, "end": v(1.26, 28.27) * mm});
            skLineSegment(sketch, "E768", {"start": v(1.26, 28.27) * mm, "end": v(1.3, 28.63) * mm});
            skLineSegment(sketch, "E769", {"start": v(1.3, 28.63) * mm, "end": v(1.35, 29) * mm});
            skLineSegment(sketch, "E770", {"start": v(1.35, 29) * mm, "end": v(1.44, 29.35) * mm});
            skLineSegment(sketch, "E771", {"start": v(1.44, 29.35) * mm, "end": v(1.55, 29.71) * mm});
            skLineSegment(sketch, "E772", {"start": v(1.55, 29.71) * mm, "end": v(1.68, 30.07) * mm});
            skLineSegment(sketch, "E773", {"start": v(1.68, 30.07) * mm, "end": v(2.6, 30) * mm});
            skLineSegment(sketch, "E774", {"start": v(2.6, 30) * mm, "end": v(2.69, 29.63) * mm});
            skLineSegment(sketch, "E775", {"start": v(2.69, 29.63) * mm, "end": v(2.74, 29.26) * mm});
            skLineSegment(sketch, "E776", {"start": v(2.74, 29.26) * mm, "end": v(2.78, 28.89) * mm});
            skLineSegment(sketch, "E777", {"start": v(2.78, 28.89) * mm, "end": v(2.79, 28.52) * mm});
            skLineSegment(sketch, "E778", {"start": v(2.79, 28.52) * mm, "end": v(2.77, 28.16) * mm});
            skLineSegment(sketch, "E779", {"start": v(2.77, 28.16) * mm, "end": v(2.8, 27.97) * mm});
            skLineSegment(sketch, "E780", {"start": v(2.8, 27.97) * mm, "end": v(2.84, 27.88) * mm});
            skLineSegment(sketch, "E781", {"start": v(2.84, 27.88) * mm, "end": v(3.44, 27.72) * mm});
            skLineSegment(sketch, "E782", {"start": v(3.44, 27.72) * mm, "end": v(4.07, 27.72) * mm});
            skLineSegment(sketch, "E783", {"start": v(4.07, 27.72) * mm, "end": v(4.13, 27.8) * mm});
            skLineSegment(sketch, "E784", {"start": v(4.13, 27.8) * mm, "end": v(4.2, 27.98) * mm});
            skLineSegment(sketch, "E785", {"start": v(4.2, 27.98) * mm, "end": v(4.28, 28.34) * mm});
            skLineSegment(sketch, "E786", {"start": v(4.28, 28.34) * mm, "end": v(4.37, 28.7) * mm});
            skLineSegment(sketch, "E787", {"start": v(4.37, 28.7) * mm, "end": v(4.5, 29.04) * mm});
            skLineSegment(sketch, "E788", {"start": v(4.5, 29.04) * mm, "end": v(4.65, 29.39) * mm});
            skLineSegment(sketch, "E789", {"start": v(4.65, 29.39) * mm, "end": v(4.81, 29.73) * mm});
            skLineSegment(sketch, "E790", {"start": v(4.81, 29.73) * mm, "end": v(5.73, 29.57) * mm});
            skLineSegment(sketch, "E791", {"start": v(5.73, 29.57) * mm, "end": v(5.77, 29.19) * mm});
            skLineSegment(sketch, "E792", {"start": v(5.77, 29.19) * mm, "end": v(5.79, 28.81) * mm});
            skLineSegment(sketch, "E793", {"start": v(5.79, 28.81) * mm, "end": v(5.79, 28.44) * mm});
            skLineSegment(sketch, "E794", {"start": v(5.79, 28.44) * mm, "end": v(5.75, 28.07) * mm});
            skLineSegment(sketch, "E795", {"start": v(5.75, 28.07) * mm, "end": v(5.7, 27.71) * mm});
            skLineSegment(sketch, "E796", {"start": v(5.7, 27.71) * mm, "end": v(5.7, 27.52) * mm});
            skLineSegment(sketch, "E797", {"start": v(5.7, 27.52) * mm, "end": v(5.74, 27.43) * mm});
            skLineSegment(sketch, "E798", {"start": v(5.74, 27.43) * mm, "end": v(6.32, 27.2) * mm});
            skLineSegment(sketch, "E799", {"start": v(6.32, 27.2) * mm, "end": v(6.94, 27.15) * mm});
            skLineSegment(sketch, "E800", {"start": v(6.94, 27.15) * mm, "end": v(7.01, 27.22) * mm});
            skLineSegment(sketch, "E801", {"start": v(7.01, 27.22) * mm, "end": v(7.1, 27.39) * mm});
            skLineSegment(sketch, "E802", {"start": v(7.1, 27.39) * mm, "end": v(7.21, 27.74) * mm});
            skLineSegment(sketch, "E803", {"start": v(7.21, 27.74) * mm, "end": v(7.35, 28.08) * mm});
            skLineSegment(sketch, "E804", {"start": v(7.35, 28.08) * mm, "end": v(7.5, 28.41) * mm});
            skLineSegment(sketch, "E805", {"start": v(7.5, 28.41) * mm, "end": v(7.7, 28.74) * mm});
            skLineSegment(sketch, "E806", {"start": v(7.7, 28.74) * mm, "end": v(7.9, 29.06) * mm});
            skLineSegment(sketch, "E807", {"start": v(7.9, 29.06) * mm, "end": v(8.79, 28.8) * mm});
            skLineSegment(sketch, "E808", {"start": v(8.79, 28.8) * mm, "end": v(8.79, 28.43) * mm});
            skLineSegment(sketch, "E809", {"start": v(8.79, 28.43) * mm, "end": v(8.77, 28.05) * mm});
            skLineSegment(sketch, "E810", {"start": v(8.77, 28.05) * mm, "end": v(8.73, 27.68) * mm});
            skLineSegment(sketch, "E811", {"start": v(8.73, 27.68) * mm, "end": v(8.66, 27.32) * mm});
            skLineSegment(sketch, "E812", {"start": v(8.66, 27.32) * mm, "end": v(8.56, 26.97) * mm});
            skLineSegment(sketch, "E813", {"start": v(8.56, 26.97) * mm, "end": v(8.55, 26.78) * mm});
            skLineSegment(sketch, "E814", {"start": v(8.55, 26.78) * mm, "end": v(8.57, 26.68) * mm});
            skLineSegment(sketch, "E815", {"start": v(8.57, 26.68) * mm, "end": v(9.13, 26.4) * mm});
            skLineSegment(sketch, "E816", {"start": v(9.13, 26.4) * mm, "end": v(9.74, 26.27) * mm});
            skLineSegment(sketch, "E817", {"start": v(9.74, 26.27) * mm, "end": v(9.82, 26.34) * mm});
            skLineSegment(sketch, "E818", {"start": v(9.82, 26.34) * mm, "end": v(9.93, 26.5) * mm});
            skLineSegment(sketch, "E819", {"start": v(9.93, 26.5) * mm, "end": v(10.07, 26.83) * mm});
            skLineSegment(sketch, "E820", {"start": v(10.07, 26.83) * mm, "end": v(10.24, 27.16) * mm});
            skLineSegment(sketch, "E821", {"start": v(10.24, 27.16) * mm, "end": v(10.44, 27.47) * mm});
            skLineSegment(sketch, "E822", {"start": v(10.44, 27.47) * mm, "end": v(10.65, 27.78) * mm});
            skLineSegment(sketch, "E823", {"start": v(10.65, 27.78) * mm, "end": v(10.89, 28.08) * mm});
            skLineSegment(sketch, "E824", {"start": v(10.89, 28.08) * mm, "end": v(11.75, 27.73) * mm});
            skLineSegment(sketch, "E825", {"start": v(11.75, 27.73) * mm, "end": v(11.71, 27.35) * mm});
            skLineSegment(sketch, "E826", {"start": v(11.71, 27.35) * mm, "end": v(11.65, 26.98) * mm});
            skLineSegment(sketch, "E827", {"start": v(11.65, 26.98) * mm, "end": v(11.57, 26.62) * mm});
            skLineSegment(sketch, "E828", {"start": v(11.57, 26.62) * mm, "end": v(11.46, 26.27) * mm});
            skLineSegment(sketch, "E829", {"start": v(11.46, 26.27) * mm, "end": v(11.33, 25.92) * mm});
            skLineSegment(sketch, "E830", {"start": v(11.33, 25.92) * mm, "end": v(11.3, 25.74) * mm});
            skLineSegment(sketch, "E831", {"start": v(11.3, 25.74) * mm, "end": v(11.31, 25.63) * mm});
            skLineSegment(sketch, "E832", {"start": v(11.31, 25.63) * mm, "end": v(11.84, 25.3) * mm});
            skLineSegment(sketch, "E833", {"start": v(11.84, 25.3) * mm, "end": v(12.43, 25.1) * mm});
            skLineSegment(sketch, "E834", {"start": v(12.43, 25.1) * mm, "end": v(12.52, 25.17) * mm});
            skLineSegment(sketch, "E835", {"start": v(12.52, 25.17) * mm, "end": v(12.64, 25.31) * mm});
            skLineSegment(sketch, "E836", {"start": v(12.64, 25.31) * mm, "end": v(12.82, 25.63) * mm});
            skLineSegment(sketch, "E837", {"start": v(12.82, 25.63) * mm, "end": v(13.02, 25.94) * mm});
            skLineSegment(sketch, "E838", {"start": v(13.02, 25.94) * mm, "end": v(13.25, 26.23) * mm});
            skLineSegment(sketch, "E839", {"start": v(13.25, 26.23) * mm, "end": v(13.5, 26.51) * mm});
            skLineSegment(sketch, "E840", {"start": v(13.5, 26.51) * mm, "end": v(13.76, 26.79) * mm});
            skLineSegment(sketch, "E841", {"start": v(13.76, 26.79) * mm, "end": v(14.59, 26.35) * mm});
            skLineSegment(sketch, "E842", {"start": v(14.59, 26.35) * mm, "end": v(14.5, 25.98) * mm});
            skLineSegment(sketch, "E843", {"start": v(14.5, 25.98) * mm, "end": v(14.4, 25.61) * mm});
            skLineSegment(sketch, "E844", {"start": v(14.4, 25.61) * mm, "end": v(14.3, 25.26) * mm});
            skLineSegment(sketch, "E845", {"start": v(14.3, 25.26) * mm, "end": v(14.15, 24.92) * mm});
            skLineSegment(sketch, "E846", {"start": v(14.15, 24.92) * mm, "end": v(13.98, 24.6) * mm});
            skLineSegment(sketch, "E847", {"start": v(13.98, 24.6) * mm, "end": v(13.93, 24.41) * mm});
            skLineSegment(sketch, "E848", {"start": v(13.93, 24.41) * mm, "end": v(13.93, 24.31) * mm});
            skLineSegment(sketch, "E849", {"start": v(13.93, 24.31) * mm, "end": v(14.42, 23.92) * mm});
            skLineSegment(sketch, "E850", {"start": v(14.42, 23.92) * mm, "end": v(15, 23.67) * mm});
            skLineSegment(sketch, "E851", {"start": v(15, 23.67) * mm, "end": v(15.08, 23.72) * mm});
            skLineSegment(sketch, "E852", {"start": v(15.08, 23.72) * mm, "end": v(15.22, 23.85) * mm});
            skLineSegment(sketch, "E853", {"start": v(15.22, 23.85) * mm, "end": v(15.43, 24.15) * mm});
            skLineSegment(sketch, "E854", {"start": v(15.43, 24.15) * mm, "end": v(15.66, 24.43) * mm});
            skLineSegment(sketch, "E855", {"start": v(15.66, 24.43) * mm, "end": v(15.92, 24.7) * mm});
            skLineSegment(sketch, "E856", {"start": v(15.92, 24.7) * mm, "end": v(16.2, 24.96) * mm});
            skLineSegment(sketch, "E857", {"start": v(16.2, 24.96) * mm, "end": v(16.49, 25.2) * mm});
            skLineSegment(sketch, "E858", {"start": v(16.49, 25.2) * mm, "end": v(17.26, 24.68) * mm});
            skLineSegment(sketch, "E859", {"start": v(17.26, 24.68) * mm, "end": v(17.14, 24.32) * mm});
            skLineSegment(sketch, "E860", {"start": v(17.14, 24.32) * mm, "end": v(17, 23.97) * mm});
            skLineSegment(sketch, "E861", {"start": v(17, 23.97) * mm, "end": v(16.85, 23.63) * mm});
            skLineSegment(sketch, "E862", {"start": v(16.85, 23.63) * mm, "end": v(16.67, 23.3) * mm});
            skLineSegment(sketch, "E863", {"start": v(16.67, 23.3) * mm, "end": v(16.48, 23) * mm});
            skLineSegment(sketch, "E864", {"start": v(16.48, 23) * mm, "end": v(16.41, 22.82) * mm});
            skLineSegment(sketch, "E865", {"start": v(16.41, 22.82) * mm, "end": v(16.4, 22.72) * mm});
            skLineSegment(sketch, "E866", {"start": v(16.4, 22.72) * mm, "end": v(16.84, 22.28) * mm});
            skLineSegment(sketch, "E867", {"start": v(16.84, 22.28) * mm, "end": v(17.38, 21.98) * mm});
            skLineSegment(sketch, "E868", {"start": v(17.38, 21.98) * mm, "end": v(17.48, 22.02) * mm});
            skLineSegment(sketch, "E869", {"start": v(17.48, 22.02) * mm, "end": v(17.63, 22.13) * mm});
            skLineSegment(sketch, "E870", {"start": v(17.63, 22.13) * mm, "end": v(17.87, 22.4) * mm});
            skLineSegment(sketch, "E871", {"start": v(17.87, 22.4) * mm, "end": v(18.13, 22.66) * mm});
            skLineSegment(sketch, "E872", {"start": v(18.13, 22.66) * mm, "end": v(18.42, 22.9) * mm});
            skLineSegment(sketch, "E873", {"start": v(18.42, 22.9) * mm, "end": v(18.72, 23.13) * mm});
            skLineSegment(sketch, "E874", {"start": v(18.72, 23.13) * mm, "end": v(19.03, 23.34) * mm});
            skLineSegment(sketch, "E875", {"start": v(19.03, 23.34) * mm, "end": v(19.75, 22.74) * mm});
            skLineSegment(sketch, "E876", {"start": v(19.75, 22.74) * mm, "end": v(19.59, 22.4) * mm});
            skLineSegment(sketch, "E877", {"start": v(19.59, 22.4) * mm, "end": v(19.42, 22.06) * mm});
            skLineSegment(sketch, "E878", {"start": v(19.42, 22.06) * mm, "end": v(19.23, 21.74) * mm});
            skLineSegment(sketch, "E879", {"start": v(19.23, 21.74) * mm, "end": v(19.02, 21.44) * mm});
            skLineSegment(sketch, "E880", {"start": v(19.02, 21.44) * mm, "end": v(18.8, 21.15) * mm});
            skLineSegment(sketch, "E881", {"start": v(18.8, 21.15) * mm, "end": v(18.7, 20.98) * mm});
            skLineSegment(sketch, "E882", {"start": v(18.7, 20.98) * mm, "end": v(18.68, 20.88) * mm});
            skLineSegment(sketch, "E883", {"start": v(18.68, 20.88) * mm, "end": v(19.08, 20.4) * mm});
            skLineSegment(sketch, "E884", {"start": v(19.08, 20.4) * mm, "end": v(19.59, 20.04) * mm});
            skLineSegment(sketch, "E885", {"start": v(19.59, 20.04) * mm, "end": v(19.68, 20.07) * mm});
            skLineSegment(sketch, "E886", {"start": v(19.68, 20.07) * mm, "end": v(19.85, 20.16) * mm});
            skLineSegment(sketch, "E887", {"start": v(19.85, 20.16) * mm, "end": v(20.12, 20.41) * mm});
            skLineSegment(sketch, "E888", {"start": v(20.12, 20.41) * mm, "end": v(20.4, 20.64) * mm});
            skLineSegment(sketch, "E889", {"start": v(20.4, 20.64) * mm, "end": v(20.7, 20.85) * mm});
            skLineSegment(sketch, "E890", {"start": v(20.7, 20.85) * mm, "end": v(21.03, 21.04) * mm});
            skLineSegment(sketch, "E891", {"start": v(21.03, 21.04) * mm, "end": v(21.37, 21.22) * mm});
            skLineSegment(sketch, "E892", {"start": v(21.37, 21.22) * mm, "end": v(22.01, 20.55) * mm});
            skLineSegment(sketch, "E893", {"start": v(22.01, 20.55) * mm, "end": v(21.82, 20.22) * mm});
            skLineSegment(sketch, "E894", {"start": v(21.82, 20.22) * mm, "end": v(21.62, 19.9) * mm});
            skLineSegment(sketch, "E895", {"start": v(21.62, 19.9) * mm, "end": v(21.4, 19.6) * mm});
            skLineSegment(sketch, "E896", {"start": v(21.4, 19.6) * mm, "end": v(21.16, 19.33) * mm});
            skLineSegment(sketch, "E897", {"start": v(21.16, 19.33) * mm, "end": v(20.9, 19.07) * mm});
            skLineSegment(sketch, "E898", {"start": v(20.9, 19.07) * mm, "end": v(20.8, 18.91) * mm});
            skLineSegment(sketch, "E899", {"start": v(20.8, 18.91) * mm, "end": v(20.76, 18.82) * mm});
            skLineSegment(sketch, "E900", {"start": v(20.76, 18.82) * mm, "end": v(21.1, 18.3) * mm});
            skLineSegment(sketch, "E901", {"start": v(21.1, 18.3) * mm, "end": v(21.57, 17.88) * mm});
            skLineSegment(sketch, "E902", {"start": v(21.57, 17.88) * mm, "end": v(21.67, 17.9) * mm});
            skLineSegment(sketch, "E903", {"start": v(21.67, 17.9) * mm, "end": v(21.85, 17.98) * mm});
            skLineSegment(sketch, "E904", {"start": v(21.85, 17.98) * mm, "end": v(22.14, 18.2) * mm});
            skLineSegment(sketch, "E905", {"start": v(22.14, 18.2) * mm, "end": v(22.45, 18.4) * mm});
            skLineSegment(sketch, "E906", {"start": v(22.45, 18.4) * mm, "end": v(22.77, 18.57) * mm});
            skLineSegment(sketch, "E907", {"start": v(22.77, 18.57) * mm, "end": v(23.12, 18.73) * mm});
            skLineSegment(sketch, "E908", {"start": v(23.12, 18.73) * mm, "end": v(23.47, 18.87) * mm});
            skLineSegment(sketch, "E909", {"start": v(23.47, 18.87) * mm, "end": v(24.04, 18.14) * mm});
            skLineSegment(sketch, "E910", {"start": v(24.04, 18.14) * mm, "end": v(23.82, 17.83) * mm});
            skLineSegment(sketch, "E911", {"start": v(23.82, 17.83) * mm, "end": v(23.58, 17.54) * mm});
            skLineSegment(sketch, "E912", {"start": v(23.58, 17.54) * mm, "end": v(23.33, 17.26) * mm});
            skLineSegment(sketch, "E913", {"start": v(23.33, 17.26) * mm, "end": v(23.06, 17.01) * mm});
            skLineSegment(sketch, "E914", {"start": v(23.06, 17.01) * mm, "end": v(22.78, 16.78) * mm});
            skLineSegment(sketch, "E915", {"start": v(22.78, 16.78) * mm, "end": v(22.66, 16.64) * mm});
            skLineSegment(sketch, "E916", {"start": v(22.66, 16.64) * mm, "end": v(22.61, 16.54) * mm});
            skLineSegment(sketch, "E917", {"start": v(22.61, 16.54) * mm, "end": v(22.9, 15.99) * mm});
            skLineSegment(sketch, "E918", {"start": v(22.9, 15.99) * mm, "end": v(23.32, 15.53) * mm});
            skLineSegment(sketch, "E919", {"start": v(23.32, 15.53) * mm, "end": v(23.43, 15.54) * mm});
            skLineSegment(sketch, "E920", {"start": v(23.43, 15.54) * mm, "end": v(23.6, 15.6) * mm});
            skLineSegment(sketch, "E921", {"start": v(23.6, 15.6) * mm, "end": v(23.92, 15.78) * mm});
            skLineSegment(sketch, "E922", {"start": v(23.92, 15.78) * mm, "end": v(24.25, 15.95) * mm});
            skLineSegment(sketch, "E923", {"start": v(24.25, 15.95) * mm, "end": v(24.6, 16.1) * mm});
            skLineSegment(sketch, "E924", {"start": v(24.6, 16.1) * mm, "end": v(24.95, 16.21) * mm});
            skLineSegment(sketch, "E925", {"start": v(24.95, 16.21) * mm, "end": v(25.31, 16.32) * mm});
            skLineSegment(sketch, "E926", {"start": v(25.31, 16.32) * mm, "end": v(25.8, 15.53) * mm});
            skLineSegment(sketch, "E927", {"start": v(25.8, 15.53) * mm, "end": v(25.55, 15.24) * mm});
            skLineSegment(sketch, "E928", {"start": v(25.55, 15.24) * mm, "end": v(25.28, 14.98) * mm});
            skLineSegment(sketch, "E929", {"start": v(25.28, 14.98) * mm, "end": v(25, 14.73) * mm});
            skLineSegment(sketch, "E930", {"start": v(25, 14.73) * mm, "end": v(24.71, 14.51) * mm});
            skLineSegment(sketch, "E931", {"start": v(24.71, 14.51) * mm, "end": v(24.4, 14.31) * mm});
            skLineSegment(sketch, "E932", {"start": v(24.4, 14.31) * mm, "end": v(24.27, 14.18) * mm});
            skLineSegment(sketch, "E933", {"start": v(24.27, 14.18) * mm, "end": v(24.22, 14.09) * mm});
            skLineSegment(sketch, "E934", {"start": v(24.22, 14.09) * mm, "end": v(24.45, 13.5) * mm});
            skLineSegment(sketch, "E935", {"start": v(24.45, 13.5) * mm, "end": v(24.82, 13) * mm});
            skLineSegment(sketch, "E936", {"start": v(24.82, 13) * mm, "end": v(24.92, 13) * mm});
            skLineSegment(sketch, "E937", {"start": v(24.92, 13) * mm, "end": v(25.1, 13.05) * mm});
            skLineSegment(sketch, "E938", {"start": v(25.1, 13.05) * mm, "end": v(25.44, 13.2) * mm});
            skLineSegment(sketch, "E939", {"start": v(25.44, 13.2) * mm, "end": v(25.78, 13.33) * mm});
            skLineSegment(sketch, "E940", {"start": v(25.78, 13.33) * mm, "end": v(26.14, 13.43) * mm});
            skLineSegment(sketch, "E941", {"start": v(26.14, 13.43) * mm, "end": v(26.5, 13.52) * mm});
            skLineSegment(sketch, "E942", {"start": v(26.5, 13.52) * mm, "end": v(26.88, 13.58) * mm});
            skLineSegment(sketch, "E943", {"start": v(26.88, 13.58) * mm, "end": v(27.29, 12.74) * mm});
            skLineSegment(sketch, "E944", {"start": v(27.29, 12.74) * mm, "end": v(27, 12.5) * mm});
            skLineSegment(sketch, "E945", {"start": v(27, 12.5) * mm, "end": v(26.71, 12.25) * mm});
            skLineSegment(sketch, "E946", {"start": v(26.71, 12.25) * mm, "end": v(26.4, 12.04) * mm});
            skLineSegment(sketch, "E947", {"start": v(26.4, 12.04) * mm, "end": v(26.1, 11.85) * mm});
            skLineSegment(sketch, "E948", {"start": v(26.1, 11.85) * mm, "end": v(25.77, 11.68) * mm});
            skLineSegment(sketch, "E949", {"start": v(25.77, 11.68) * mm, "end": v(25.62, 11.56) * mm});
            skLineSegment(sketch, "E950", {"start": v(25.62, 11.56) * mm, "end": v(25.56, 11.48) * mm});
            skLineSegment(sketch, "E951", {"start": v(25.56, 11.48) * mm, "end": v(25.72, 10.88) * mm});
            skLineSegment(sketch, "E952", {"start": v(25.72, 10.88) * mm, "end": v(26.04, 10.34) * mm});
            skLineSegment(sketch, "E953", {"start": v(26.04, 10.34) * mm, "end": v(26.14, 10.33) * mm});
            skLineSegment(sketch, "E954", {"start": v(26.14, 10.33) * mm, "end": v(26.33, 10.35) * mm});
            skLineSegment(sketch, "E955", {"start": v(26.33, 10.35) * mm, "end": v(26.68, 10.47) * mm});
            skLineSegment(sketch, "E956", {"start": v(26.68, 10.47) * mm, "end": v(27.03, 10.56) * mm});
            skLineSegment(sketch, "E957", {"start": v(27.03, 10.56) * mm, "end": v(27.4, 10.63) * mm});
            skLineSegment(sketch, "E958", {"start": v(27.4, 10.63) * mm, "end": v(27.77, 10.67) * mm});
            skLineSegment(sketch, "E959", {"start": v(27.77, 10.67) * mm, "end": v(28.15, 10.7) * mm});
            skLineSegment(sketch, "E960", {"start": v(28.15, 10.7) * mm, "end": v(28.47, 9.82) * mm});
            skLineSegment(sketch, "E961", {"start": v(28.47, 9.82) * mm, "end": v(28.16, 9.6) * mm});
            skLineSegment(sketch, "E962", {"start": v(28.16, 9.6) * mm, "end": v(27.85, 9.4) * mm});
            skLineSegment(sketch, "E963", {"start": v(27.85, 9.4) * mm, "end": v(27.52, 9.2) * mm});
            skLineSegment(sketch, "E964", {"start": v(27.52, 9.2) * mm, "end": v(27.19, 9.06) * mm});
            skLineSegment(sketch, "E965", {"start": v(27.19, 9.06) * mm, "end": v(26.85, 8.92) * mm});
            skLineSegment(sketch, "E966", {"start": v(26.85, 8.92) * mm, "end": v(26.7, 8.82) * mm});
            skLineSegment(sketch, "E967", {"start": v(26.7, 8.82) * mm, "end": v(26.62, 8.74) * mm});
            skLineSegment(sketch, "E968", {"start": v(26.62, 8.74) * mm, "end": v(26.72, 8.13) * mm});
            skLineSegment(sketch, "E969", {"start": v(26.72, 8.13) * mm, "end": v(26.98, 7.56) * mm});
            skLineSegment(sketch, "E970", {"start": v(26.98, 7.56) * mm, "end": v(27.08, 7.54) * mm});
            skLineSegment(sketch, "E971", {"start": v(27.08, 7.54) * mm, "end": v(27.27, 7.54) * mm});
            skLineSegment(sketch, "E972", {"start": v(27.27, 7.54) * mm, "end": v(27.63, 7.62) * mm});
            skLineSegment(sketch, "E973", {"start": v(27.63, 7.62) * mm, "end": v(27.99, 7.68) * mm});
            skLineSegment(sketch, "E974", {"start": v(27.99, 7.68) * mm, "end": v(28.36, 7.7) * mm});
            skLineSegment(sketch, "E975", {"start": v(28.36, 7.7) * mm, "end": v(28.74, 7.7) * mm});
            skLineSegment(sketch, "E976", {"start": v(28.74, 7.7) * mm, "end": v(29.12, 7.7) * mm});
            skLineSegment(sketch, "E977", {"start": v(29.12, 7.7) * mm, "end": v(29.34, 6.8) * mm});
            skLineSegment(sketch, "E978", {"start": v(29.34, 6.8) * mm, "end": v(29.01, 6.6) * mm});
            skLineSegment(sketch, "E979", {"start": v(29.01, 6.6) * mm, "end": v(28.68, 6.43) * mm});
            skLineSegment(sketch, "E980", {"start": v(28.68, 6.43) * mm, "end": v(28.33, 6.28) * mm});
            skLineSegment(sketch, "E981", {"start": v(28.33, 6.28) * mm, "end": v(27.99, 6.16) * mm});
            skLineSegment(sketch, "E982", {"start": v(27.99, 6.16) * mm, "end": v(27.63, 6.07) * mm});
            skLineSegment(sketch, "E983", {"start": v(27.63, 6.07) * mm, "end": v(27.47, 5.98) * mm});
            skLineSegment(sketch, "E984", {"start": v(27.47, 5.98) * mm, "end": v(27.39, 5.91) * mm});
            skLineSegment(sketch, "E985", {"start": v(27.39, 5.91) * mm, "end": v(27.42, 5.3) * mm});
            skLineSegment(sketch, "E986", {"start": v(27.42, 5.3) * mm, "end": v(27.62, 4.7) * mm});
            skLineSegment(sketch, "E987", {"start": v(27.62, 4.7) * mm, "end": v(27.72, 4.67) * mm});
            skLineSegment(sketch, "E988", {"start": v(27.72, 4.67) * mm, "end": v(27.9, 4.65) * mm});
            skLineSegment(sketch, "E989", {"start": v(27.9, 4.65) * mm, "end": v(28.27, 4.7) * mm});
            skLineSegment(sketch, "E990", {"start": v(28.27, 4.7) * mm, "end": v(28.64, 4.7) * mm});
            skLineSegment(sketch, "E991", {"start": v(28.64, 4.7) * mm, "end": v(29, 4.7) * mm});
            skLineSegment(sketch, "E992", {"start": v(29, 4.7) * mm, "end": v(29.38, 4.66) * mm});
            skLineSegment(sketch, "E993", {"start": v(29.38, 4.66) * mm, "end": v(29.76, 4.61) * mm});
            skLineSegment(sketch, "E994", {"start": v(29.76, 4.61) * mm, "end": v(29.9, 3.69) * mm});
            skLineSegment(sketch, "E995", {"start": v(29.9, 3.69) * mm, "end": v(29.54, 3.53) * mm});
            skLineSegment(sketch, "E996", {"start": v(29.54, 3.53) * mm, "end": v(29.2, 3.4) * mm});
            skLineSegment(sketch, "E997", {"start": v(29.2, 3.4) * mm, "end": v(28.84, 3.29) * mm});
            skLineSegment(sketch, "E998", {"start": v(28.84, 3.29) * mm, "end": v(28.48, 3.2) * mm});
            skLineSegment(sketch, "E999", {"start": v(28.48, 3.2) * mm, "end": v(28.12, 3.15) * mm});
            skLineSegment(sketch, "E1000", {"start": v(28.12, 3.15) * mm, "end": v(27.94, 3.08) * mm});
            skLineSegment(sketch, "E1001", {"start": v(27.94, 3.08) * mm, "end": v(27.86, 3.02) * mm});
            skLineSegment(sketch, "E1002", {"start": v(27.86, 3.02) * mm, "end": v(27.83, 2.4) * mm});
            skLineSegment(sketch, "E1003", {"start": v(27.83, 2.4) * mm, "end": v(27.96, 1.79) * mm});
            skLineSegment(sketch, "E1004", {"start": v(27.96, 1.79) * mm, "end": v(28.06, 1.74) * mm});
            skLineSegment(sketch, "E1005", {"start": v(28.06, 1.74) * mm, "end": v(28.24, 1.7) * mm});
            skLineSegment(sketch, "E1006", {"start": v(28.24, 1.7) * mm, "end": v(28.6, 1.7) * mm});
            skLineSegment(sketch, "E1007", {"start": v(28.6, 1.7) * mm, "end": v(28.97, 1.7) * mm});
            skLineSegment(sketch, "E1008", {"start": v(28.97, 1.7) * mm, "end": v(29.34, 1.64) * mm});
            skLineSegment(sketch, "E1009", {"start": v(29.34, 1.64) * mm, "end": v(29.71, 1.57) * mm});
            skLineSegment(sketch, "E1010", {"start": v(29.71, 1.57) * mm, "end": v(30.08, 1.47) * mm});
            skLineSegment(sketch, "E1011", {"start": v(30.08, 1.47) * mm, "end": v(30.11, 0.54) * mm});
            skLineSegment(sketch, "E1012", {"start": v(30.11, 0.54) * mm, "end": v(29.75, 0.43) * mm});
            skLineSegment(sketch, "E1013", {"start": v(29.75, 0.43) * mm, "end": v(29.39, 0.33) * mm});
            skLineSegment(sketch, "E1014", {"start": v(29.39, 0.33) * mm, "end": v(29.02, 0.25) * mm});
            skLineSegment(sketch, "E1015", {"start": v(29.02, 0.25) * mm, "end": v(28.66, 0.21) * mm});
            skLineSegment(sketch, "E1016", {"start": v(28.66, 0.21) * mm, "end": v(28.3, 0.19) * mm});
            skLineSegment(sketch, "E1017", {"start": v(28.3, 0.19) * mm, "end": v(28.11, 0.14) * mm});
            skLineSegment(sketch, "E1018", {"start": v(28.11, 0.14) * mm, "end": v(28.02, 0.1) * mm});
            skLineSegment(sketch, "E1019", {"start": v(28.02, 0.1) * mm, "end": v(27.92, -0.53) * mm});
            skSolve(sketch);
        }
        {
            var Q0;
            Q0=qCreatedBy(makeId("Front.planeOp"),FACE);
            cPlane(context, id + "F1", {"entities" : qUnion([Q0]), "cplaneType" : CPlaneType.OFFSET, "offset" : 10 * mm, "width" : 150 * mm, "height" : 150 * mm});
        }
        {
            var Q0;
            Q0=qCreatedBy(id+"F1.planeOp",FACE);
            var sketch = newSketch(context, id + "F2", { "sketchPlane" : qUnion([Q0])});
            skLineSegment(sketch, "E1020", {"start": v(27.88, -3) * mm, "end": v(27.9, -3.63) * mm});
            skLineSegment(sketch, "E1021", {"start": v(27.9, -3.63) * mm, "end": v(27.99, -3.7) * mm});
            skLineSegment(sketch, "E1022", {"start": v(27.99, -3.7) * mm, "end": v(28.16, -3.77) * mm});
            skLineSegment(sketch, "E1023", {"start": v(28.16, -3.77) * mm, "end": v(28.52, -3.83) * mm});
            skLineSegment(sketch, "E1024", {"start": v(28.52, -3.83) * mm, "end": v(28.88, -3.92) * mm});
            skLineSegment(sketch, "E1025", {"start": v(28.88, -3.92) * mm, "end": v(29.23, -4.04) * mm});
            skLineSegment(sketch, "E1026", {"start": v(29.23, -4.04) * mm, "end": v(29.58, -4.18) * mm});
            skLineSegment(sketch, "E1027", {"start": v(29.58, -4.18) * mm, "end": v(29.92, -4.34) * mm});
            skLineSegment(sketch, "E1028", {"start": v(29.92, -4.34) * mm, "end": v(29.78, -5.26) * mm});
            skLineSegment(sketch, "E1029", {"start": v(29.78, -5.26) * mm, "end": v(29.4, -5.3) * mm});
            skLineSegment(sketch, "E1030", {"start": v(29.4, -5.3) * mm, "end": v(29.02, -5.34) * mm});
            skLineSegment(sketch, "E1031", {"start": v(29.02, -5.34) * mm, "end": v(28.65, -5.34) * mm});
            skLineSegment(sketch, "E1032", {"start": v(28.65, -5.34) * mm, "end": v(28.28, -5.31) * mm});
            skLineSegment(sketch, "E1033", {"start": v(28.28, -5.31) * mm, "end": v(27.92, -5.26) * mm});
            skLineSegment(sketch, "E1034", {"start": v(27.92, -5.26) * mm, "end": v(27.73, -5.28) * mm});
            skLineSegment(sketch, "E1035", {"start": v(27.73, -5.28) * mm, "end": v(27.63, -5.3) * mm});
            skLineSegment(sketch, "E1036", {"start": v(27.63, -5.3) * mm, "end": v(27.42, -5.9) * mm});
            skLineSegment(sketch, "E1037", {"start": v(27.42, -5.9) * mm, "end": v(27.38, -6.52) * mm});
            skLineSegment(sketch, "E1038", {"start": v(27.38, -6.52) * mm, "end": v(27.45, -6.59) * mm});
            skLineSegment(sketch, "E1039", {"start": v(27.45, -6.59) * mm, "end": v(27.62, -6.68) * mm});
            skLineSegment(sketch, "E1040", {"start": v(27.62, -6.68) * mm, "end": v(27.97, -6.78) * mm});
            skLineSegment(sketch, "E1041", {"start": v(27.97, -6.78) * mm, "end": v(28.31, -6.9) * mm});
            skLineSegment(sketch, "E1042", {"start": v(28.31, -6.9) * mm, "end": v(28.65, -7.06) * mm});
            skLineSegment(sketch, "E1043", {"start": v(28.65, -7.06) * mm, "end": v(28.98, -7.24) * mm});
            skLineSegment(sketch, "E1044", {"start": v(28.98, -7.24) * mm, "end": v(29.31, -7.44) * mm});
            skLineSegment(sketch, "E1045", {"start": v(29.31, -7.44) * mm, "end": v(29.07, -8.34) * mm});
            skLineSegment(sketch, "E1046", {"start": v(29.07, -8.34) * mm, "end": v(28.69, -8.34) * mm});
            skLineSegment(sketch, "E1047", {"start": v(28.69, -8.34) * mm, "end": v(28.31, -8.33) * mm});
            skLineSegment(sketch, "E1048", {"start": v(28.31, -8.33) * mm, "end": v(27.94, -8.3) * mm});
            skLineSegment(sketch, "E1049", {"start": v(27.94, -8.3) * mm, "end": v(27.58, -8.23) * mm});
            skLineSegment(sketch, "E1050", {"start": v(27.58, -8.23) * mm, "end": v(27.22, -8.14) * mm});
            skLineSegment(sketch, "E1051", {"start": v(27.22, -8.14) * mm, "end": v(27.04, -8.14) * mm});
            skLineSegment(sketch, "E1052", {"start": v(27.04, -8.14) * mm, "end": v(26.93, -8.16) * mm});
            skLineSegment(sketch, "E1053", {"start": v(26.93, -8.16) * mm, "end": v(26.66, -8.72) * mm});
            skLineSegment(sketch, "E1054", {"start": v(26.66, -8.72) * mm, "end": v(26.55, -9.33) * mm});
            skLineSegment(sketch, "E1055", {"start": v(26.55, -9.33) * mm, "end": v(26.62, -9.4) * mm});
            skLineSegment(sketch, "E1056", {"start": v(26.62, -9.4) * mm, "end": v(26.78, -9.52) * mm});
            skLineSegment(sketch, "E1057", {"start": v(26.78, -9.52) * mm, "end": v(27.11, -9.66) * mm});
            skLineSegment(sketch, "E1058", {"start": v(27.11, -9.66) * mm, "end": v(27.44, -9.82) * mm});
            skLineSegment(sketch, "E1059", {"start": v(27.44, -9.82) * mm, "end": v(27.76, -10) * mm});
            skLineSegment(sketch, "E1060", {"start": v(27.76, -10) * mm, "end": v(28.07, -10.22) * mm});
            skLineSegment(sketch, "E1061", {"start": v(28.07, -10.22) * mm, "end": v(28.38, -10.45) * mm});
            skLineSegment(sketch, "E1062", {"start": v(28.38, -10.45) * mm, "end": v(28.04, -11.32) * mm});
            skLineSegment(sketch, "E1063", {"start": v(28.04, -11.32) * mm, "end": v(27.66, -11.28) * mm});
            skLineSegment(sketch, "E1064", {"start": v(27.66, -11.28) * mm, "end": v(27.3, -11.23) * mm});
            skLineSegment(sketch, "E1065", {"start": v(27.3, -11.23) * mm, "end": v(26.93, -11.16) * mm});
            skLineSegment(sketch, "E1066", {"start": v(26.93, -11.16) * mm, "end": v(26.57, -11.05) * mm});
            skLineSegment(sketch, "E1067", {"start": v(26.57, -11.05) * mm, "end": v(26.23, -10.93) * mm});
            skLineSegment(sketch, "E1068", {"start": v(26.23, -10.93) * mm, "end": v(26.04, -10.9) * mm});
            skLineSegment(sketch, "E1069", {"start": v(26.04, -10.9) * mm, "end": v(25.94, -10.92) * mm});
            skLineSegment(sketch, "E1070", {"start": v(25.94, -10.92) * mm, "end": v(25.61, -11.45) * mm});
            skLineSegment(sketch, "E1071", {"start": v(25.61, -11.45) * mm, "end": v(25.44, -12.05) * mm});
            skLineSegment(sketch, "E1072", {"start": v(25.44, -12.05) * mm, "end": v(25.5, -12.13) * mm});
            skLineSegment(sketch, "E1073", {"start": v(25.5, -12.13) * mm, "end": v(25.64, -12.25) * mm});
            skLineSegment(sketch, "E1074", {"start": v(25.64, -12.25) * mm, "end": v(25.96, -12.43) * mm});
            skLineSegment(sketch, "E1075", {"start": v(25.96, -12.43) * mm, "end": v(26.27, -12.62) * mm});
            skLineSegment(sketch, "E1076", {"start": v(26.27, -12.62) * mm, "end": v(26.57, -12.84) * mm});
            skLineSegment(sketch, "E1077", {"start": v(26.57, -12.84) * mm, "end": v(26.86, -13.09) * mm});
            skLineSegment(sketch, "E1078", {"start": v(26.86, -13.09) * mm, "end": v(27.14, -13.35) * mm});
            skLineSegment(sketch, "E1079", {"start": v(27.14, -13.35) * mm, "end": v(26.71, -14.17) * mm});
            skLineSegment(sketch, "E1080", {"start": v(26.71, -14.17) * mm, "end": v(26.34, -14.1) * mm});
            skLineSegment(sketch, "E1081", {"start": v(26.34, -14.1) * mm, "end": v(25.97, -14) * mm});
            skLineSegment(sketch, "E1082", {"start": v(25.97, -14) * mm, "end": v(25.62, -13.9) * mm});
            skLineSegment(sketch, "E1083", {"start": v(25.62, -13.9) * mm, "end": v(25.28, -13.76) * mm});
            skLineSegment(sketch, "E1084", {"start": v(25.28, -13.76) * mm, "end": v(24.95, -13.6) * mm});
            skLineSegment(sketch, "E1085", {"start": v(24.95, -13.6) * mm, "end": v(24.77, -13.56) * mm});
            skLineSegment(sketch, "E1086", {"start": v(24.77, -13.56) * mm, "end": v(24.66, -13.56) * mm});
            skLineSegment(sketch, "E1087", {"start": v(24.66, -13.56) * mm, "end": v(24.28, -14.05) * mm});
            skLineSegment(sketch, "E1088", {"start": v(24.28, -14.05) * mm, "end": v(24.04, -14.63) * mm});
            skLineSegment(sketch, "E1089", {"start": v(24.04, -14.63) * mm, "end": v(24.1, -14.72) * mm});
            skLineSegment(sketch, "E1090", {"start": v(24.1, -14.72) * mm, "end": v(24.23, -14.85) * mm});
            skLineSegment(sketch, "E1091", {"start": v(24.23, -14.85) * mm, "end": v(24.53, -15.06) * mm});
            skLineSegment(sketch, "E1092", {"start": v(24.53, -15.06) * mm, "end": v(24.82, -15.28) * mm});
            skLineSegment(sketch, "E1093", {"start": v(24.82, -15.28) * mm, "end": v(25.09, -15.54) * mm});
            skLineSegment(sketch, "E1094", {"start": v(25.09, -15.54) * mm, "end": v(25.35, -15.8) * mm});
            skLineSegment(sketch, "E1095", {"start": v(25.35, -15.8) * mm, "end": v(25.6, -16.1) * mm});
            skLineSegment(sketch, "E1096", {"start": v(25.6, -16.1) * mm, "end": v(25.1, -16.88) * mm});
            skLineSegment(sketch, "E1097", {"start": v(25.1, -16.88) * mm, "end": v(24.73, -16.77) * mm});
            skLineSegment(sketch, "E1098", {"start": v(24.73, -16.77) * mm, "end": v(24.37, -16.64) * mm});
            skLineSegment(sketch, "E1099", {"start": v(24.37, -16.64) * mm, "end": v(24.03, -16.49) * mm});
            skLineSegment(sketch, "E1100", {"start": v(24.03, -16.49) * mm, "end": v(23.7, -16.32) * mm});
            skLineSegment(sketch, "E1101", {"start": v(23.7, -16.32) * mm, "end": v(23.4, -16.12) * mm});
            skLineSegment(sketch, "E1102", {"start": v(23.4, -16.12) * mm, "end": v(23.22, -16.06) * mm});
            skLineSegment(sketch, "E1103", {"start": v(23.22, -16.06) * mm, "end": v(23.12, -16.05) * mm});
            skLineSegment(sketch, "E1104", {"start": v(23.12, -16.05) * mm, "end": v(22.68, -16.5) * mm});
            skLineSegment(sketch, "E1105", {"start": v(22.68, -16.5) * mm, "end": v(22.39, -17.05) * mm});
            skLineSegment(sketch, "E1106", {"start": v(22.39, -17.05) * mm, "end": v(22.43, -17.14) * mm});
            skLineSegment(sketch, "E1107", {"start": v(22.43, -17.14) * mm, "end": v(22.55, -17.3) * mm});
            skLineSegment(sketch, "E1108", {"start": v(22.55, -17.3) * mm, "end": v(22.82, -17.53) * mm});
            skLineSegment(sketch, "E1109", {"start": v(22.82, -17.53) * mm, "end": v(23.09, -17.78) * mm});
            skLineSegment(sketch, "E1110", {"start": v(23.09, -17.78) * mm, "end": v(23.33, -18.06) * mm});
            skLineSegment(sketch, "E1111", {"start": v(23.33, -18.06) * mm, "end": v(23.56, -18.36) * mm});
            skLineSegment(sketch, "E1112", {"start": v(23.56, -18.36) * mm, "end": v(23.78, -18.67) * mm});
            skLineSegment(sketch, "E1113", {"start": v(23.78, -18.67) * mm, "end": v(23.2, -19.4) * mm});
            skLineSegment(sketch, "E1114", {"start": v(23.2, -19.4) * mm, "end": v(22.85, -19.25) * mm});
            skLineSegment(sketch, "E1115", {"start": v(22.85, -19.25) * mm, "end": v(22.5, -19.08) * mm});
            skLineSegment(sketch, "E1116", {"start": v(22.5, -19.08) * mm, "end": v(22.18, -18.9) * mm});
            skLineSegment(sketch, "E1117", {"start": v(22.18, -18.9) * mm, "end": v(21.88, -18.7) * mm});
            skLineSegment(sketch, "E1118", {"start": v(21.88, -18.7) * mm, "end": v(21.6, -18.47) * mm});
            skLineSegment(sketch, "E1119", {"start": v(21.6, -18.47) * mm, "end": v(21.42, -18.39) * mm});
            skLineSegment(sketch, "E1120", {"start": v(21.42, -18.39) * mm, "end": v(21.32, -18.36) * mm});
            skLineSegment(sketch, "E1121", {"start": v(21.32, -18.36) * mm, "end": v(20.84, -18.77) * mm});
            skLineSegment(sketch, "E1122", {"start": v(20.84, -18.77) * mm, "end": v(20.49, -19.28) * mm});
            skLineSegment(sketch, "E1123", {"start": v(20.49, -19.28) * mm, "end": v(20.52, -19.38) * mm});
            skLineSegment(sketch, "E1124", {"start": v(20.52, -19.38) * mm, "end": v(20.62, -19.54) * mm});
            skLineSegment(sketch, "E1125", {"start": v(20.62, -19.54) * mm, "end": v(20.87, -19.8) * mm});
            skLineSegment(sketch, "E1126", {"start": v(20.87, -19.8) * mm, "end": v(21.1, -20.09) * mm});
            skLineSegment(sketch, "E1127", {"start": v(21.1, -20.09) * mm, "end": v(21.32, -20.4) * mm});
            skLineSegment(sketch, "E1128", {"start": v(21.32, -20.4) * mm, "end": v(21.52, -20.71) * mm});
            skLineSegment(sketch, "E1129", {"start": v(21.52, -20.71) * mm, "end": v(21.7, -21.05) * mm});
            skLineSegment(sketch, "E1130", {"start": v(21.7, -21.05) * mm, "end": v(21.05, -21.7) * mm});
            skLineSegment(sketch, "E1131", {"start": v(21.05, -21.7) * mm, "end": v(20.71, -21.52) * mm});
            skLineSegment(sketch, "E1132", {"start": v(20.71, -21.52) * mm, "end": v(20.4, -21.32) * mm});
            skLineSegment(sketch, "E1133", {"start": v(20.4, -21.32) * mm, "end": v(20.1, -21.1) * mm});
            skLineSegment(sketch, "E1134", {"start": v(20.1, -21.1) * mm, "end": v(19.81, -20.87) * mm});
            skLineSegment(sketch, "E1135", {"start": v(19.81, -20.87) * mm, "end": v(19.55, -20.61) * mm});
            skLineSegment(sketch, "E1136", {"start": v(19.55, -20.61) * mm, "end": v(19.39, -20.51) * mm});
            skLineSegment(sketch, "E1137", {"start": v(19.39, -20.51) * mm, "end": v(19.29, -20.48) * mm});
            skLineSegment(sketch, "E1138", {"start": v(19.29, -20.48) * mm, "end": v(18.77, -20.83) * mm});
            skLineSegment(sketch, "E1139", {"start": v(18.77, -20.83) * mm, "end": v(18.37, -21.3) * mm});
            skLineSegment(sketch, "E1140", {"start": v(18.37, -21.3) * mm, "end": v(18.4, -21.4) * mm});
            skLineSegment(sketch, "E1141", {"start": v(18.4, -21.4) * mm, "end": v(18.47, -21.58) * mm});
            skLineSegment(sketch, "E1142", {"start": v(18.47, -21.58) * mm, "end": v(18.7, -21.87) * mm});
            skLineSegment(sketch, "E1143", {"start": v(18.7, -21.87) * mm, "end": v(18.9, -22.17) * mm});
            skLineSegment(sketch, "E1144", {"start": v(18.9, -22.17) * mm, "end": v(19.08, -22.5) * mm});
            skLineSegment(sketch, "E1145", {"start": v(19.08, -22.5) * mm, "end": v(19.24, -22.84) * mm});
            skLineSegment(sketch, "E1146", {"start": v(19.24, -22.84) * mm, "end": v(19.4, -23.19) * mm});
            skLineSegment(sketch, "E1147", {"start": v(19.4, -23.19) * mm, "end": v(18.67, -23.77) * mm});
            skLineSegment(sketch, "E1148", {"start": v(18.67, -23.77) * mm, "end": v(18.36, -23.55) * mm});
            skLineSegment(sketch, "E1149", {"start": v(18.36, -23.55) * mm, "end": v(18.06, -23.32) * mm});
            skLineSegment(sketch, "E1150", {"start": v(18.06, -23.32) * mm, "end": v(17.78, -23.08) * mm});
            skLineSegment(sketch, "E1151", {"start": v(17.78, -23.08) * mm, "end": v(17.53, -22.81) * mm});
            skLineSegment(sketch, "E1152", {"start": v(17.53, -22.81) * mm, "end": v(17.3, -22.53) * mm});
            skLineSegment(sketch, "E1153", {"start": v(17.3, -22.53) * mm, "end": v(17.14, -22.42) * mm});
            skLineSegment(sketch, "E1154", {"start": v(17.14, -22.42) * mm, "end": v(17.05, -22.37) * mm});
            skLineSegment(sketch, "E1155", {"start": v(17.05, -22.37) * mm, "end": v(16.5, -22.67) * mm});
            skLineSegment(sketch, "E1156", {"start": v(16.5, -22.67) * mm, "end": v(16.05, -23.1) * mm});
            skLineSegment(sketch, "E1157", {"start": v(16.05, -23.1) * mm, "end": v(16.06, -23.2) * mm});
            skLineSegment(sketch, "E1158", {"start": v(16.06, -23.2) * mm, "end": v(16.12, -23.38) * mm});
            skLineSegment(sketch, "E1159", {"start": v(16.12, -23.38) * mm, "end": v(16.31, -23.7) * mm});
            skLineSegment(sketch, "E1160", {"start": v(16.31, -23.7) * mm, "end": v(16.48, -24.02) * mm});
            skLineSegment(sketch, "E1161", {"start": v(16.48, -24.02) * mm, "end": v(16.63, -24.36) * mm});
            skLineSegment(sketch, "E1162", {"start": v(16.63, -24.36) * mm, "end": v(16.76, -24.71) * mm});
            skLineSegment(sketch, "E1163", {"start": v(16.76, -24.71) * mm, "end": v(16.87, -25.08) * mm});
            skLineSegment(sketch, "E1164", {"start": v(16.87, -25.08) * mm, "end": v(16.09, -25.58) * mm});
            skLineSegment(sketch, "E1165", {"start": v(16.09, -25.58) * mm, "end": v(15.8, -25.33) * mm});
            skLineSegment(sketch, "E1166", {"start": v(15.8, -25.33) * mm, "end": v(15.53, -25.07) * mm});
            skLineSegment(sketch, "E1167", {"start": v(15.53, -25.07) * mm, "end": v(15.28, -24.8) * mm});
            skLineSegment(sketch, "E1168", {"start": v(15.28, -24.8) * mm, "end": v(15.05, -24.5) * mm});
            skLineSegment(sketch, "E1169", {"start": v(15.05, -24.5) * mm, "end": v(14.85, -24.2) * mm});
            skLineSegment(sketch, "E1170", {"start": v(14.85, -24.2) * mm, "end": v(14.71, -24.07) * mm});
            skLineSegment(sketch, "E1171", {"start": v(14.71, -24.07) * mm, "end": v(14.62, -24.02) * mm});
            skLineSegment(sketch, "E1172", {"start": v(14.62, -24.02) * mm, "end": v(14.04, -24.26) * mm});
            skLineSegment(sketch, "E1173", {"start": v(14.04, -24.26) * mm, "end": v(13.55, -24.64) * mm});
            skLineSegment(sketch, "E1174", {"start": v(13.55, -24.64) * mm, "end": v(13.55, -24.74) * mm});
            skLineSegment(sketch, "E1175", {"start": v(13.55, -24.74) * mm, "end": v(13.6, -24.93) * mm});
            skLineSegment(sketch, "E1176", {"start": v(13.6, -24.93) * mm, "end": v(13.75, -25.26) * mm});
            skLineSegment(sketch, "E1177", {"start": v(13.75, -25.26) * mm, "end": v(13.9, -25.6) * mm});
            skLineSegment(sketch, "E1178", {"start": v(13.9, -25.6) * mm, "end": v(14, -25.95) * mm});
            skLineSegment(sketch, "E1179", {"start": v(14, -25.95) * mm, "end": v(14.09, -26.32) * mm});
            skLineSegment(sketch, "E1180", {"start": v(14.09, -26.32) * mm, "end": v(14.16, -26.7) * mm});
            skLineSegment(sketch, "E1181", {"start": v(14.16, -26.7) * mm, "end": v(13.33, -27.11) * mm});
            skLineSegment(sketch, "E1182", {"start": v(13.33, -27.11) * mm, "end": v(13.07, -26.83) * mm});
            skLineSegment(sketch, "E1183", {"start": v(13.07, -26.83) * mm, "end": v(12.83, -26.54) * mm});
            skLineSegment(sketch, "E1184", {"start": v(12.83, -26.54) * mm, "end": v(12.6, -26.25) * mm});
            skLineSegment(sketch, "E1185", {"start": v(12.6, -26.25) * mm, "end": v(12.41, -25.93) * mm});
            skLineSegment(sketch, "E1186", {"start": v(12.41, -25.93) * mm, "end": v(12.24, -25.61) * mm});
            skLineSegment(sketch, "E1187", {"start": v(12.24, -25.61) * mm, "end": v(12.12, -25.47) * mm});
            skLineSegment(sketch, "E1188", {"start": v(12.12, -25.47) * mm, "end": v(12.04, -25.4) * mm});
            skLineSegment(sketch, "E1189", {"start": v(12.04, -25.4) * mm, "end": v(11.44, -25.58) * mm});
            skLineSegment(sketch, "E1190", {"start": v(11.44, -25.58) * mm, "end": v(10.9, -25.9) * mm});
            skLineSegment(sketch, "E1191", {"start": v(10.9, -25.9) * mm, "end": v(10.9, -26.01) * mm});
            skLineSegment(sketch, "E1192", {"start": v(10.9, -26.01) * mm, "end": v(10.92, -26.2) * mm});
            skLineSegment(sketch, "E1193", {"start": v(10.92, -26.2) * mm, "end": v(11.04, -26.54) * mm});
            skLineSegment(sketch, "E1194", {"start": v(11.04, -26.54) * mm, "end": v(11.14, -26.9) * mm});
            skLineSegment(sketch, "E1195", {"start": v(11.14, -26.9) * mm, "end": v(11.22, -27.26) * mm});
            skLineSegment(sketch, "E1196", {"start": v(11.22, -27.26) * mm, "end": v(11.27, -27.63) * mm});
            skLineSegment(sketch, "E1197", {"start": v(11.27, -27.63) * mm, "end": v(11.3, -28.01) * mm});
            skLineSegment(sketch, "E1198", {"start": v(11.3, -28.01) * mm, "end": v(10.43, -28.35) * mm});
            skLineSegment(sketch, "E1199", {"start": v(10.43, -28.35) * mm, "end": v(10.2, -28.04) * mm});
            skLineSegment(sketch, "E1200", {"start": v(10.2, -28.04) * mm, "end": v(10, -27.73) * mm});
            skLineSegment(sketch, "E1201", {"start": v(10, -27.73) * mm, "end": v(9.8, -27.4) * mm});
            skLineSegment(sketch, "E1202", {"start": v(9.8, -27.4) * mm, "end": v(9.64, -27.08) * mm});
            skLineSegment(sketch, "E1203", {"start": v(9.64, -27.08) * mm, "end": v(9.5, -26.74) * mm});
            skLineSegment(sketch, "E1204", {"start": v(9.5, -26.74) * mm, "end": v(9.4, -26.58) * mm});
            skLineSegment(sketch, "E1205", {"start": v(9.4, -26.58) * mm, "end": v(9.32, -26.51) * mm});
            skLineSegment(sketch, "E1206", {"start": v(9.32, -26.51) * mm, "end": v(8.7, -26.62) * mm});
            skLineSegment(sketch, "E1207", {"start": v(8.7, -26.62) * mm, "end": v(8.14, -26.9) * mm});
            skLineSegment(sketch, "E1208", {"start": v(8.14, -26.9) * mm, "end": v(8.12, -27) * mm});
            skLineSegment(sketch, "E1209", {"start": v(8.12, -27) * mm, "end": v(8.13, -27.19) * mm});
            skLineSegment(sketch, "E1210", {"start": v(8.13, -27.19) * mm, "end": v(8.21, -27.54) * mm});
            skLineSegment(sketch, "E1211", {"start": v(8.21, -27.54) * mm, "end": v(8.28, -27.9) * mm});
            skLineSegment(sketch, "E1212", {"start": v(8.28, -27.9) * mm, "end": v(8.31, -28.27) * mm});
            skLineSegment(sketch, "E1213", {"start": v(8.31, -28.27) * mm, "end": v(8.32, -28.65) * mm});
            skLineSegment(sketch, "E1214", {"start": v(8.32, -28.65) * mm, "end": v(8.32, -29.03) * mm});
            skLineSegment(sketch, "E1215", {"start": v(8.32, -29.03) * mm, "end": v(7.42, -29.27) * mm});
            skLineSegment(sketch, "E1216", {"start": v(7.42, -29.27) * mm, "end": v(7.22, -28.94) * mm});
            skLineSegment(sketch, "E1217", {"start": v(7.22, -28.94) * mm, "end": v(7.04, -28.6) * mm});
            skLineSegment(sketch, "E1218", {"start": v(7.04, -28.6) * mm, "end": v(6.89, -28.27) * mm});
            skLineSegment(sketch, "E1219", {"start": v(6.89, -28.27) * mm, "end": v(6.76, -27.93) * mm});
            skLineSegment(sketch, "E1220", {"start": v(6.76, -27.93) * mm, "end": v(6.66, -27.58) * mm});
            skLineSegment(sketch, "E1221", {"start": v(6.66, -27.58) * mm, "end": v(6.57, -27.4) * mm});
            skLineSegment(sketch, "E1222", {"start": v(6.57, -27.4) * mm, "end": v(6.5, -27.33) * mm});
            skLineSegment(sketch, "E1223", {"start": v(6.5, -27.33) * mm, "end": v(5.88, -27.38) * mm});
            skLineSegment(sketch, "E1224", {"start": v(5.88, -27.38) * mm, "end": v(5.3, -27.59) * mm});
            skLineSegment(sketch, "E1225", {"start": v(5.3, -27.59) * mm, "end": v(5.26, -27.69) * mm});
            skLineSegment(sketch, "E1226", {"start": v(5.26, -27.69) * mm, "end": v(5.25, -27.87) * mm});
            skLineSegment(sketch, "E1227", {"start": v(5.25, -27.87) * mm, "end": v(5.3, -28.24) * mm});
            skLineSegment(sketch, "E1228", {"start": v(5.3, -28.24) * mm, "end": v(5.32, -28.6) * mm});
            skLineSegment(sketch, "E1229", {"start": v(5.32, -28.6) * mm, "end": v(5.32, -28.97) * mm});
            skLineSegment(sketch, "E1230", {"start": v(5.32, -28.97) * mm, "end": v(5.29, -29.35) * mm});
            skLineSegment(sketch, "E1231", {"start": v(5.29, -29.35) * mm, "end": v(5.24, -29.73) * mm});
            skLineSegment(sketch, "E1232", {"start": v(5.24, -29.73) * mm, "end": v(4.32, -29.87) * mm});
            skLineSegment(sketch, "E1233", {"start": v(4.32, -29.87) * mm, "end": v(4.16, -29.53) * mm});
            skLineSegment(sketch, "E1234", {"start": v(4.16, -29.53) * mm, "end": v(4.02, -29.18) * mm});
            skLineSegment(sketch, "E1235", {"start": v(4.02, -29.18) * mm, "end": v(3.9, -28.83) * mm});
            skLineSegment(sketch, "E1236", {"start": v(3.9, -28.83) * mm, "end": v(3.81, -28.47) * mm});
            skLineSegment(sketch, "E1237", {"start": v(3.81, -28.47) * mm, "end": v(3.75, -28.1) * mm});
            skLineSegment(sketch, "E1238", {"start": v(3.75, -28.1) * mm, "end": v(3.68, -27.94) * mm});
            skLineSegment(sketch, "E1239", {"start": v(3.68, -27.94) * mm, "end": v(3.62, -27.85) * mm});
            skLineSegment(sketch, "E1240", {"start": v(3.62, -27.85) * mm, "end": v(3, -27.83) * mm});
            skLineSegment(sketch, "E1241", {"start": v(3, -27.83) * mm, "end": v(2.39, -27.98) * mm});
            skLineSegment(sketch, "E1242", {"start": v(2.39, -27.98) * mm, "end": v(2.35, -28.07) * mm});
            skLineSegment(sketch, "E1243", {"start": v(2.35, -28.07) * mm, "end": v(2.31, -28.26) * mm});
            skLineSegment(sketch, "E1244", {"start": v(2.31, -28.26) * mm, "end": v(2.32, -28.62) * mm});
            skLineSegment(sketch, "E1245", {"start": v(2.32, -28.62) * mm, "end": v(2.3, -29) * mm});
            skLineSegment(sketch, "E1246", {"start": v(2.3, -29) * mm, "end": v(2.26, -29.36) * mm});
            skLineSegment(sketch, "E1247", {"start": v(2.26, -29.36) * mm, "end": v(2.2, -29.73) * mm});
            skLineSegment(sketch, "E1248", {"start": v(2.2, -29.73) * mm, "end": v(2.11, -30.1) * mm});
            skLineSegment(sketch, "E1249", {"start": v(2.11, -30.1) * mm, "end": v(1.18, -30.15) * mm});
            skLineSegment(sketch, "E1250", {"start": v(1.18, -30.15) * mm, "end": v(1.06, -29.79) * mm});
            skLineSegment(sketch, "E1251", {"start": v(1.06, -29.79) * mm, "end": v(0.96, -29.43) * mm});
            skLineSegment(sketch, "E1252", {"start": v(0.96, -29.43) * mm, "end": v(0.87, -29.06) * mm});
            skLineSegment(sketch, "E1253", {"start": v(0.87, -29.06) * mm, "end": v(0.82, -28.7) * mm});
            skLineSegment(sketch, "E1254", {"start": v(0.82, -28.7) * mm, "end": v(0.8, -28.34) * mm});
            skLineSegment(sketch, "E1255", {"start": v(0.8, -28.34) * mm, "end": v(0.74, -28.15) * mm});
            skLineSegment(sketch, "E1256", {"start": v(0.74, -28.15) * mm, "end": v(0.7, -28.06) * mm});
            skLineSegment(sketch, "E1257", {"start": v(0.7, -28.06) * mm, "end": v(0.07, -27.98) * mm});
            skLineSegment(sketch, "E1258", {"start": v(0.07, -27.98) * mm, "end": v(-0.55, -28.06) * mm});
            skLineSegment(sketch, "E1259", {"start": v(-0.55, -28.06) * mm, "end": v(-0.6, -28.15) * mm});
            skLineSegment(sketch, "E1260", {"start": v(-0.6, -28.15) * mm, "end": v(-0.65, -28.33) * mm});
            skLineSegment(sketch, "E1261", {"start": v(-0.65, -28.33) * mm, "end": v(-0.68, -28.7) * mm});
            skLineSegment(sketch, "E1262", {"start": v(-0.68, -28.7) * mm, "end": v(-0.73, -29.06) * mm});
            skLineSegment(sketch, "E1263", {"start": v(-0.73, -29.06) * mm, "end": v(-0.81, -29.42) * mm});
            skLineSegment(sketch, "E1264", {"start": v(-0.81, -29.42) * mm, "end": v(-0.92, -29.79) * mm});
            skLineSegment(sketch, "E1265", {"start": v(-0.92, -29.79) * mm, "end": v(-1.04, -30.15) * mm});
            skLineSegment(sketch, "E1266", {"start": v(-1.04, -30.15) * mm, "end": v(-1.97, -30.1) * mm});
            skLineSegment(sketch, "E1267", {"start": v(-1.97, -30.1) * mm, "end": v(-2.05, -29.72) * mm});
            skLineSegment(sketch, "E1268", {"start": v(-2.05, -29.72) * mm, "end": v(-2.12, -29.35) * mm});
            skLineSegment(sketch, "E1269", {"start": v(-2.12, -29.35) * mm, "end": v(-2.16, -28.98) * mm});
            skLineSegment(sketch, "E1270", {"start": v(-2.16, -28.98) * mm, "end": v(-2.17, -28.62) * mm});
            skLineSegment(sketch, "E1271", {"start": v(-2.17, -28.62) * mm, "end": v(-2.16, -28.25) * mm});
            skLineSegment(sketch, "E1272", {"start": v(-2.16, -28.25) * mm, "end": v(-2.2, -28.07) * mm});
            skLineSegment(sketch, "E1273", {"start": v(-2.2, -28.07) * mm, "end": v(-2.24, -27.97) * mm});
            skLineSegment(sketch, "E1274", {"start": v(-2.24, -27.97) * mm, "end": v(-2.84, -27.82) * mm});
            skLineSegment(sketch, "E1275", {"start": v(-2.84, -27.82) * mm, "end": v(-3.47, -27.84) * mm});
            skLineSegment(sketch, "E1276", {"start": v(-3.47, -27.84) * mm, "end": v(-3.53, -27.92) * mm});
            skLineSegment(sketch, "E1277", {"start": v(-3.53, -27.92) * mm, "end": v(-3.6, -28.1) * mm});
            skLineSegment(sketch, "E1278", {"start": v(-3.6, -28.1) * mm, "end": v(-3.67, -28.46) * mm});
            skLineSegment(sketch, "E1279", {"start": v(-3.67, -28.46) * mm, "end": v(-3.76, -28.82) * mm});
            skLineSegment(sketch, "E1280", {"start": v(-3.76, -28.82) * mm, "end": v(-3.88, -29.17) * mm});
            skLineSegment(sketch, "E1281", {"start": v(-3.88, -29.17) * mm, "end": v(-4.02, -29.52) * mm});
            skLineSegment(sketch, "E1282", {"start": v(-4.02, -29.52) * mm, "end": v(-4.18, -29.86) * mm});
            skLineSegment(sketch, "E1283", {"start": v(-4.18, -29.86) * mm, "end": v(-5.1, -29.71) * mm});
            skLineSegment(sketch, "E1284", {"start": v(-5.1, -29.71) * mm, "end": v(-5.14, -29.34) * mm});
            skLineSegment(sketch, "E1285", {"start": v(-5.14, -29.34) * mm, "end": v(-5.17, -28.96) * mm});
            skLineSegment(sketch, "E1286", {"start": v(-5.17, -28.96) * mm, "end": v(-5.18, -28.59) * mm});
            skLineSegment(sketch, "E1287", {"start": v(-5.18, -28.59) * mm, "end": v(-5.15, -28.22) * mm});
            skLineSegment(sketch, "E1288", {"start": v(-5.15, -28.22) * mm, "end": v(-5.1, -27.86) * mm});
            skLineSegment(sketch, "E1289", {"start": v(-5.1, -27.86) * mm, "end": v(-5.11, -27.67) * mm});
            skLineSegment(sketch, "E1290", {"start": v(-5.11, -27.67) * mm, "end": v(-5.14, -27.57) * mm});
            skLineSegment(sketch, "E1291", {"start": v(-5.14, -27.57) * mm, "end": v(-5.73, -27.36) * mm});
            skLineSegment(sketch, "E1292", {"start": v(-5.73, -27.36) * mm, "end": v(-6.35, -27.31) * mm});
            skLineSegment(sketch, "E1293", {"start": v(-6.35, -27.31) * mm, "end": v(-6.42, -27.4) * mm});
            skLineSegment(sketch, "E1294", {"start": v(-6.42, -27.4) * mm, "end": v(-6.51, -27.56) * mm});
            skLineSegment(sketch, "E1295", {"start": v(-6.51, -27.56) * mm, "end": v(-6.62, -27.9) * mm});
            skLineSegment(sketch, "E1296", {"start": v(-6.62, -27.9) * mm, "end": v(-6.74, -28.25) * mm});
            skLineSegment(sketch, "E1297", {"start": v(-6.74, -28.25) * mm, "end": v(-6.9, -28.6) * mm});
            skLineSegment(sketch, "E1298", {"start": v(-6.9, -28.6) * mm, "end": v(-7.08, -28.92) * mm});
            skLineSegment(sketch, "E1299", {"start": v(-7.08, -28.92) * mm, "end": v(-7.27, -29.25) * mm});
            skLineSegment(sketch, "E1300", {"start": v(-7.27, -29.25) * mm, "end": v(-8.17, -29) * mm});
            skLineSegment(sketch, "E1301", {"start": v(-8.17, -29) * mm, "end": v(-8.18, -28.63) * mm});
            skLineSegment(sketch, "E1302", {"start": v(-8.18, -28.63) * mm, "end": v(-8.16, -28.25) * mm});
            skLineSegment(sketch, "E1303", {"start": v(-8.16, -28.25) * mm, "end": v(-8.13, -27.88) * mm});
            skLineSegment(sketch, "E1304", {"start": v(-8.13, -27.88) * mm, "end": v(-8.06, -27.52) * mm});
            skLineSegment(sketch, "E1305", {"start": v(-8.06, -27.52) * mm, "end": v(-7.98, -27.16) * mm});
            skLineSegment(sketch, "E1306", {"start": v(-7.98, -27.16) * mm, "end": v(-7.97, -26.97) * mm});
            skLineSegment(sketch, "E1307", {"start": v(-7.97, -26.97) * mm, "end": v(-8, -26.87) * mm});
            skLineSegment(sketch, "E1308", {"start": v(-8, -26.87) * mm, "end": v(-8.55, -26.6) * mm});
            skLineSegment(sketch, "E1309", {"start": v(-8.55, -26.6) * mm, "end": v(-9.17, -26.49) * mm});
            skLineSegment(sketch, "E1310", {"start": v(-9.17, -26.49) * mm, "end": v(-9.24, -26.56) * mm});
            skLineSegment(sketch, "E1311", {"start": v(-9.24, -26.56) * mm, "end": v(-9.35, -26.71) * mm});
            skLineSegment(sketch, "E1312", {"start": v(-9.35, -26.71) * mm, "end": v(-9.5, -27.05) * mm});
            skLineSegment(sketch, "E1313", {"start": v(-9.5, -27.05) * mm, "end": v(-9.65, -27.38) * mm});
            skLineSegment(sketch, "E1314", {"start": v(-9.65, -27.38) * mm, "end": v(-9.84, -27.7) * mm});
            skLineSegment(sketch, "E1315", {"start": v(-9.84, -27.7) * mm, "end": v(-10.05, -28.01) * mm});
            skLineSegment(sketch, "E1316", {"start": v(-10.05, -28.01) * mm, "end": v(-10.28, -28.32) * mm});
            skLineSegment(sketch, "E1317", {"start": v(-10.28, -28.32) * mm, "end": v(-11.15, -27.98) * mm});
            skLineSegment(sketch, "E1318", {"start": v(-11.15, -27.98) * mm, "end": v(-11.12, -27.6) * mm});
            skLineSegment(sketch, "E1319", {"start": v(-11.12, -27.6) * mm, "end": v(-11.07, -27.23) * mm});
            skLineSegment(sketch, "E1320", {"start": v(-11.07, -27.23) * mm, "end": v(-11, -26.86) * mm});
            skLineSegment(sketch, "E1321", {"start": v(-11, -26.86) * mm, "end": v(-10.9, -26.51) * mm});
            skLineSegment(sketch, "E1322", {"start": v(-10.9, -26.51) * mm, "end": v(-10.77, -26.17) * mm});
            skLineSegment(sketch, "E1323", {"start": v(-10.77, -26.17) * mm, "end": v(-10.74, -25.98) * mm});
            skLineSegment(sketch, "E1324", {"start": v(-10.74, -25.98) * mm, "end": v(-10.75, -25.88) * mm});
            skLineSegment(sketch, "E1325", {"start": v(-10.75, -25.88) * mm, "end": v(-11.28, -25.55) * mm});
            skLineSegment(sketch, "E1326", {"start": v(-11.28, -25.55) * mm, "end": v(-11.88, -25.37) * mm});
            skLineSegment(sketch, "E1327", {"start": v(-11.88, -25.37) * mm, "end": v(-11.96, -25.44) * mm});
            skLineSegment(sketch, "E1328", {"start": v(-11.96, -25.44) * mm, "end": v(-12.09, -25.58) * mm});
            skLineSegment(sketch, "E1329", {"start": v(-12.09, -25.58) * mm, "end": v(-12.26, -25.9) * mm});
            skLineSegment(sketch, "E1330", {"start": v(-12.26, -25.9) * mm, "end": v(-12.45, -26.21) * mm});
            skLineSegment(sketch, "E1331", {"start": v(-12.45, -26.21) * mm, "end": v(-12.68, -26.5) * mm});
            skLineSegment(sketch, "E1332", {"start": v(-12.68, -26.5) * mm, "end": v(-12.92, -26.8) * mm});
            skLineSegment(sketch, "E1333", {"start": v(-12.92, -26.8) * mm, "end": v(-13.18, -27.08) * mm});
            skLineSegment(sketch, "E1334", {"start": v(-13.18, -27.08) * mm, "end": v(-14.01, -26.65) * mm});
            skLineSegment(sketch, "E1335", {"start": v(-14.01, -26.65) * mm, "end": v(-13.94, -26.28) * mm});
            skLineSegment(sketch, "E1336", {"start": v(-13.94, -26.28) * mm, "end": v(-13.85, -25.91) * mm});
            skLineSegment(sketch, "E1337", {"start": v(-13.85, -25.91) * mm, "end": v(-13.74, -25.56) * mm});
            skLineSegment(sketch, "E1338", {"start": v(-13.74, -25.56) * mm, "end": v(-13.6, -25.22) * mm});
            skLineSegment(sketch, "E1339", {"start": v(-13.6, -25.22) * mm, "end": v(-13.44, -24.89) * mm});
            skLineSegment(sketch, "E1340", {"start": v(-13.44, -24.89) * mm, "end": v(-13.4, -24.7) * mm});
            skLineSegment(sketch, "E1341", {"start": v(-13.4, -24.7) * mm, "end": v(-13.4, -24.6) * mm});
            skLineSegment(sketch, "E1342", {"start": v(-13.4, -24.6) * mm, "end": v(-13.88, -24.22) * mm});
            skLineSegment(sketch, "E1343", {"start": v(-13.88, -24.22) * mm, "end": v(-14.46, -23.98) * mm});
            skLineSegment(sketch, "E1344", {"start": v(-14.46, -23.98) * mm, "end": v(-14.55, -24.03) * mm});
            skLineSegment(sketch, "E1345", {"start": v(-14.55, -24.03) * mm, "end": v(-14.69, -24.16) * mm});
            skLineSegment(sketch, "E1346", {"start": v(-14.69, -24.16) * mm, "end": v(-14.9, -24.47) * mm});
            skLineSegment(sketch, "E1347", {"start": v(-14.9, -24.47) * mm, "end": v(-15.12, -24.75) * mm});
            skLineSegment(sketch, "E1348", {"start": v(-15.12, -24.75) * mm, "end": v(-15.37, -25.03) * mm});
            skLineSegment(sketch, "E1349", {"start": v(-15.37, -25.03) * mm, "end": v(-15.65, -25.29) * mm});
            skLineSegment(sketch, "E1350", {"start": v(-15.65, -25.29) * mm, "end": v(-15.93, -25.54) * mm});
            skLineSegment(sketch, "E1351", {"start": v(-15.93, -25.54) * mm, "end": v(-16.71, -25.03) * mm});
            skLineSegment(sketch, "E1352", {"start": v(-16.71, -25.03) * mm, "end": v(-16.6, -24.67) * mm});
            skLineSegment(sketch, "E1353", {"start": v(-16.6, -24.67) * mm, "end": v(-16.47, -24.31) * mm});
            skLineSegment(sketch, "E1354", {"start": v(-16.47, -24.31) * mm, "end": v(-16.33, -23.97) * mm});
            skLineSegment(sketch, "E1355", {"start": v(-16.33, -23.97) * mm, "end": v(-16.15, -23.65) * mm});
            skLineSegment(sketch, "E1356", {"start": v(-16.15, -23.65) * mm, "end": v(-15.96, -23.34) * mm});
            skLineSegment(sketch, "E1357", {"start": v(-15.96, -23.34) * mm, "end": v(-15.9, -23.16) * mm});
            skLineSegment(sketch, "E1358", {"start": v(-15.9, -23.16) * mm, "end": v(-15.88, -23.06) * mm});
            skLineSegment(sketch, "E1359", {"start": v(-15.88, -23.06) * mm, "end": v(-16.33, -22.62) * mm});
            skLineSegment(sketch, "E1360", {"start": v(-16.33, -22.62) * mm, "end": v(-16.88, -22.33) * mm});
            skLineSegment(sketch, "E1361", {"start": v(-16.88, -22.33) * mm, "end": v(-16.98, -22.37) * mm});
            skLineSegment(sketch, "E1362", {"start": v(-16.98, -22.37) * mm, "end": v(-17.13, -22.48) * mm});
            skLineSegment(sketch, "E1363", {"start": v(-17.13, -22.48) * mm, "end": v(-17.36, -22.76) * mm});
            skLineSegment(sketch, "E1364", {"start": v(-17.36, -22.76) * mm, "end": v(-17.62, -23.03) * mm});
            skLineSegment(sketch, "E1365", {"start": v(-17.62, -23.03) * mm, "end": v(-17.9, -23.27) * mm});
            skLineSegment(sketch, "E1366", {"start": v(-17.9, -23.27) * mm, "end": v(-18.2, -23.5) * mm});
            skLineSegment(sketch, "E1367", {"start": v(-18.2, -23.5) * mm, "end": v(-18.5, -23.72) * mm});
            skLineSegment(sketch, "E1368", {"start": v(-18.5, -23.72) * mm, "end": v(-19.23, -23.13) * mm});
            skLineSegment(sketch, "E1369", {"start": v(-19.23, -23.13) * mm, "end": v(-19.08, -22.78) * mm});
            skLineSegment(sketch, "E1370", {"start": v(-19.08, -22.78) * mm, "end": v(-18.92, -22.45) * mm});
            skLineSegment(sketch, "E1371", {"start": v(-18.92, -22.45) * mm, "end": v(-18.74, -22.12) * mm});
            skLineSegment(sketch, "E1372", {"start": v(-18.74, -22.12) * mm, "end": v(-18.53, -21.82) * mm});
            skLineSegment(sketch, "E1373", {"start": v(-18.53, -21.82) * mm, "end": v(-18.3, -21.53) * mm});
            skLineSegment(sketch, "E1374", {"start": v(-18.3, -21.53) * mm, "end": v(-18.22, -21.36) * mm});
            skLineSegment(sketch, "E1375", {"start": v(-18.22, -21.36) * mm, "end": v(-18.2, -21.26) * mm});
            skLineSegment(sketch, "E1376", {"start": v(-18.2, -21.26) * mm, "end": v(-18.6, -20.78) * mm});
            skLineSegment(sketch, "E1377", {"start": v(-18.6, -20.78) * mm, "end": v(-19.12, -20.43) * mm});
            skLineSegment(sketch, "E1378", {"start": v(-19.12, -20.43) * mm, "end": v(-19.22, -20.46) * mm});
            skLineSegment(sketch, "E1379", {"start": v(-19.22, -20.46) * mm, "end": v(-19.38, -20.56) * mm});
            skLineSegment(sketch, "E1380", {"start": v(-19.38, -20.56) * mm, "end": v(-19.64, -20.81) * mm});
            skLineSegment(sketch, "E1381", {"start": v(-19.64, -20.81) * mm, "end": v(-19.92, -21.05) * mm});
            skLineSegment(sketch, "E1382", {"start": v(-19.92, -21.05) * mm, "end": v(-20.23, -21.26) * mm});
            skLineSegment(sketch, "E1383", {"start": v(-20.23, -21.26) * mm, "end": v(-20.55, -21.46) * mm});
            skLineSegment(sketch, "E1384", {"start": v(-20.55, -21.46) * mm, "end": v(-20.88, -21.65) * mm});
            skLineSegment(sketch, "E1385", {"start": v(-20.88, -21.65) * mm, "end": v(-21.54, -20.99) * mm});
            skLineSegment(sketch, "E1386", {"start": v(-21.54, -20.99) * mm, "end": v(-21.35, -20.65) * mm});
            skLineSegment(sketch, "E1387", {"start": v(-21.35, -20.65) * mm, "end": v(-21.15, -20.33) * mm});
            skLineSegment(sketch, "E1388", {"start": v(-21.15, -20.33) * mm, "end": v(-20.94, -20.03) * mm});
            skLineSegment(sketch, "E1389", {"start": v(-20.94, -20.03) * mm, "end": v(-20.7, -19.75) * mm});
            skLineSegment(sketch, "E1390", {"start": v(-20.7, -19.75) * mm, "end": v(-20.45, -19.49) * mm});
            skLineSegment(sketch, "E1391", {"start": v(-20.45, -19.49) * mm, "end": v(-20.35, -19.32) * mm});
            skLineSegment(sketch, "E1392", {"start": v(-20.35, -19.32) * mm, "end": v(-20.32, -19.23) * mm});
            skLineSegment(sketch, "E1393", {"start": v(-20.32, -19.23) * mm, "end": v(-20.67, -18.7) * mm});
            skLineSegment(sketch, "E1394", {"start": v(-20.67, -18.7) * mm, "end": v(-21.14, -18.3) * mm});
            skLineSegment(sketch, "E1395", {"start": v(-21.14, -18.3) * mm, "end": v(-21.24, -18.33) * mm});
            skLineSegment(sketch, "E1396", {"start": v(-21.24, -18.33) * mm, "end": v(-21.42, -18.4) * mm});
            skLineSegment(sketch, "E1397", {"start": v(-21.42, -18.4) * mm, "end": v(-21.7, -18.63) * mm});
            skLineSegment(sketch, "E1398", {"start": v(-21.7, -18.63) * mm, "end": v(-22, -18.84) * mm});
            skLineSegment(sketch, "E1399", {"start": v(-22, -18.84) * mm, "end": v(-22.33, -19.02) * mm});
            skLineSegment(sketch, "E1400", {"start": v(-22.33, -19.02) * mm, "end": v(-22.67, -19.18) * mm});
            skLineSegment(sketch, "E1401", {"start": v(-22.67, -19.18) * mm, "end": v(-23.02, -19.33) * mm});
            skLineSegment(sketch, "E1402", {"start": v(-23.02, -19.33) * mm, "end": v(-23.6, -18.6) * mm});
            skLineSegment(sketch, "E1403", {"start": v(-23.6, -18.6) * mm, "end": v(-23.39, -18.3) * mm});
            skLineSegment(sketch, "E1404", {"start": v(-23.39, -18.3) * mm, "end": v(-23.16, -18) * mm});
            skLineSegment(sketch, "E1405", {"start": v(-23.16, -18) * mm, "end": v(-22.91, -17.72) * mm});
            skLineSegment(sketch, "E1406", {"start": v(-22.91, -17.72) * mm, "end": v(-22.65, -17.47) * mm});
            skLineSegment(sketch, "E1407", {"start": v(-22.65, -17.47) * mm, "end": v(-22.37, -17.23) * mm});
            skLineSegment(sketch, "E1408", {"start": v(-22.37, -17.23) * mm, "end": v(-22.25, -17.08) * mm});
            skLineSegment(sketch, "E1409", {"start": v(-22.25, -17.08) * mm, "end": v(-22.2, -16.99) * mm});
            skLineSegment(sketch, "E1410", {"start": v(-22.2, -16.99) * mm, "end": v(-22.5, -16.44) * mm});
            skLineSegment(sketch, "E1411", {"start": v(-22.5, -16.44) * mm, "end": v(-22.94, -15.98) * mm});
            skLineSegment(sketch, "E1412", {"start": v(-22.94, -15.98) * mm, "end": v(-23.04, -16) * mm});
            skLineSegment(sketch, "E1413", {"start": v(-23.04, -16) * mm, "end": v(-23.22, -16.06) * mm});
            skLineSegment(sketch, "E1414", {"start": v(-23.22, -16.06) * mm, "end": v(-23.53, -16.25) * mm});
            skLineSegment(sketch, "E1415", {"start": v(-23.53, -16.25) * mm, "end": v(-23.85, -16.42) * mm});
            skLineSegment(sketch, "E1416", {"start": v(-23.85, -16.42) * mm, "end": v(-24.2, -16.57) * mm});
            skLineSegment(sketch, "E1417", {"start": v(-24.2, -16.57) * mm, "end": v(-24.55, -16.7) * mm});
            skLineSegment(sketch, "E1418", {"start": v(-24.55, -16.7) * mm, "end": v(-24.91, -16.8) * mm});
            skLineSegment(sketch, "E1419", {"start": v(-24.91, -16.8) * mm, "end": v(-25.42, -16.03) * mm});
            skLineSegment(sketch, "E1420", {"start": v(-25.42, -16.03) * mm, "end": v(-25.17, -15.74) * mm});
            skLineSegment(sketch, "E1421", {"start": v(-25.17, -15.74) * mm, "end": v(-24.9, -15.47) * mm});
            skLineSegment(sketch, "E1422", {"start": v(-24.9, -15.47) * mm, "end": v(-24.63, -15.22) * mm});
            skLineSegment(sketch, "E1423", {"start": v(-24.63, -15.22) * mm, "end": v(-24.34, -15) * mm});
            skLineSegment(sketch, "E1424", {"start": v(-24.34, -15) * mm, "end": v(-24.04, -14.79) * mm});
            skLineSegment(sketch, "E1425", {"start": v(-24.04, -14.79) * mm, "end": v(-23.91, -14.65) * mm});
            skLineSegment(sketch, "E1426", {"start": v(-23.91, -14.65) * mm, "end": v(-23.86, -14.56) * mm});
            skLineSegment(sketch, "E1427", {"start": v(-23.86, -14.56) * mm, "end": v(-24.1, -13.98) * mm});
            skLineSegment(sketch, "E1428", {"start": v(-24.1, -13.98) * mm, "end": v(-24.47, -13.49) * mm});
            skLineSegment(sketch, "E1429", {"start": v(-24.47, -13.49) * mm, "end": v(-24.58, -13.49) * mm});
            skLineSegment(sketch, "E1430", {"start": v(-24.58, -13.49) * mm, "end": v(-24.76, -13.53) * mm});
            skLineSegment(sketch, "E1431", {"start": v(-24.76, -13.53) * mm, "end": v(-25.1, -13.7) * mm});
            skLineSegment(sketch, "E1432", {"start": v(-25.1, -13.7) * mm, "end": v(-25.43, -13.83) * mm});
            skLineSegment(sketch, "E1433", {"start": v(-25.43, -13.83) * mm, "end": v(-25.79, -13.94) * mm});
            skLineSegment(sketch, "E1434", {"start": v(-25.79, -13.94) * mm, "end": v(-26.15, -14.03) * mm});
            skLineSegment(sketch, "E1435", {"start": v(-26.15, -14.03) * mm, "end": v(-26.53, -14.1) * mm});
            skLineSegment(sketch, "E1436", {"start": v(-26.53, -14.1) * mm, "end": v(-26.95, -13.27) * mm});
            skLineSegment(sketch, "E1437", {"start": v(-26.95, -13.27) * mm, "end": v(-26.67, -13.01) * mm});
            skLineSegment(sketch, "E1438", {"start": v(-26.67, -13.01) * mm, "end": v(-26.38, -12.77) * mm});
            skLineSegment(sketch, "E1439", {"start": v(-26.38, -12.77) * mm, "end": v(-26.08, -12.55) * mm});
            skLineSegment(sketch, "E1440", {"start": v(-26.08, -12.55) * mm, "end": v(-25.77, -12.35) * mm});
            skLineSegment(sketch, "E1441", {"start": v(-25.77, -12.35) * mm, "end": v(-25.45, -12.18) * mm});
            skLineSegment(sketch, "E1442", {"start": v(-25.45, -12.18) * mm, "end": v(-25.3, -12.06) * mm});
            skLineSegment(sketch, "E1443", {"start": v(-25.3, -12.06) * mm, "end": v(-25.24, -11.98) * mm});
            skLineSegment(sketch, "E1444", {"start": v(-25.24, -11.98) * mm, "end": v(-25.42, -11.38) * mm});
            skLineSegment(sketch, "E1445", {"start": v(-25.42, -11.38) * mm, "end": v(-25.74, -10.84) * mm});
            skLineSegment(sketch, "E1446", {"start": v(-25.74, -10.84) * mm, "end": v(-25.85, -10.83) * mm});
            skLineSegment(sketch, "E1447", {"start": v(-25.85, -10.83) * mm, "end": v(-26.03, -10.86) * mm});
            skLineSegment(sketch, "E1448", {"start": v(-26.03, -10.86) * mm, "end": v(-26.38, -10.98) * mm});
            skLineSegment(sketch, "E1449", {"start": v(-26.38, -10.98) * mm, "end": v(-26.73, -11.08) * mm});
            skLineSegment(sketch, "E1450", {"start": v(-26.73, -11.08) * mm, "end": v(-27.1, -11.15) * mm});
            skLineSegment(sketch, "E1451", {"start": v(-27.1, -11.15) * mm, "end": v(-27.47, -11.2) * mm});
            skLineSegment(sketch, "E1452", {"start": v(-27.47, -11.2) * mm, "end": v(-27.85, -11.24) * mm});
            skLineSegment(sketch, "E1453", {"start": v(-27.85, -11.24) * mm, "end": v(-28.18, -10.37) * mm});
            skLineSegment(sketch, "E1454", {"start": v(-28.18, -10.37) * mm, "end": v(-27.88, -10.14) * mm});
            skLineSegment(sketch, "E1455", {"start": v(-27.88, -10.14) * mm, "end": v(-27.56, -9.93) * mm});
            skLineSegment(sketch, "E1456", {"start": v(-27.56, -9.93) * mm, "end": v(-27.25, -9.74) * mm});
            skLineSegment(sketch, "E1457", {"start": v(-27.25, -9.74) * mm, "end": v(-26.91, -9.58) * mm});
            skLineSegment(sketch, "E1458", {"start": v(-26.91, -9.58) * mm, "end": v(-26.58, -9.44) * mm});
            skLineSegment(sketch, "E1459", {"start": v(-26.58, -9.44) * mm, "end": v(-26.42, -9.33) * mm});
            skLineSegment(sketch, "E1460", {"start": v(-26.42, -9.33) * mm, "end": v(-26.35, -9.26) * mm});
            skLineSegment(sketch, "E1461", {"start": v(-26.35, -9.26) * mm, "end": v(-26.46, -8.64) * mm});
            skLineSegment(sketch, "E1462", {"start": v(-26.46, -8.64) * mm, "end": v(-26.73, -8.08) * mm});
            skLineSegment(sketch, "E1463", {"start": v(-26.73, -8.08) * mm, "end": v(-26.83, -8.06) * mm});
            skLineSegment(sketch, "E1464", {"start": v(-26.83, -8.06) * mm, "end": v(-27.02, -8.07) * mm});
            skLineSegment(sketch, "E1465", {"start": v(-27.02, -8.07) * mm, "end": v(-27.38, -8.15) * mm});
            skLineSegment(sketch, "E1466", {"start": v(-27.38, -8.15) * mm, "end": v(-27.74, -8.22) * mm});
            skLineSegment(sketch, "E1467", {"start": v(-27.74, -8.22) * mm, "end": v(-28.1, -8.25) * mm});
            skLineSegment(sketch, "E1468", {"start": v(-28.1, -8.25) * mm, "end": v(-28.48, -8.26) * mm});
            skLineSegment(sketch, "E1469", {"start": v(-28.48, -8.26) * mm, "end": v(-28.87, -8.25) * mm});
            skLineSegment(sketch, "E1470", {"start": v(-28.87, -8.25) * mm, "end": v(-29.1, -7.35) * mm});
            skLineSegment(sketch, "E1471", {"start": v(-29.1, -7.35) * mm, "end": v(-28.78, -7.16) * mm});
            skLineSegment(sketch, "E1472", {"start": v(-28.78, -7.16) * mm, "end": v(-28.45, -6.98) * mm});
            skLineSegment(sketch, "E1473", {"start": v(-28.45, -6.98) * mm, "end": v(-28.1, -6.83) * mm});
            skLineSegment(sketch, "E1474", {"start": v(-28.1, -6.83) * mm, "end": v(-27.76, -6.7) * mm});
            skLineSegment(sketch, "E1475", {"start": v(-27.76, -6.7) * mm, "end": v(-27.41, -6.6) * mm});
            skLineSegment(sketch, "E1476", {"start": v(-27.41, -6.6) * mm, "end": v(-27.25, -6.51) * mm});
            skLineSegment(sketch, "E1477", {"start": v(-27.25, -6.51) * mm, "end": v(-27.17, -6.44) * mm});
            skLineSegment(sketch, "E1478", {"start": v(-27.17, -6.44) * mm, "end": v(-27.21, -5.82) * mm});
            skLineSegment(sketch, "E1479", {"start": v(-27.21, -5.82) * mm, "end": v(-27.42, -5.23) * mm});
            skLineSegment(sketch, "E1480", {"start": v(-27.42, -5.23) * mm, "end": v(-27.52, -5.2) * mm});
            skLineSegment(sketch, "E1481", {"start": v(-27.52, -5.2) * mm, "end": v(-27.71, -5.19) * mm});
            skLineSegment(sketch, "E1482", {"start": v(-27.71, -5.19) * mm, "end": v(-28.07, -5.23) * mm});
            skLineSegment(sketch, "E1483", {"start": v(-28.07, -5.23) * mm, "end": v(-28.44, -5.26) * mm});
            skLineSegment(sketch, "E1484", {"start": v(-28.44, -5.26) * mm, "end": v(-28.81, -5.25) * mm});
            skLineSegment(sketch, "E1485", {"start": v(-28.81, -5.25) * mm, "end": v(-29.19, -5.23) * mm});
            skLineSegment(sketch, "E1486", {"start": v(-29.19, -5.23) * mm, "end": v(-29.56, -5.18) * mm});
            skLineSegment(sketch, "E1487", {"start": v(-29.56, -5.18) * mm, "end": v(-29.7, -4.26) * mm});
            skLineSegment(sketch, "E1488", {"start": v(-29.7, -4.26) * mm, "end": v(-29.36, -4.1) * mm});
            skLineSegment(sketch, "E1489", {"start": v(-29.36, -4.1) * mm, "end": v(-29.01, -3.96) * mm});
            skLineSegment(sketch, "E1490", {"start": v(-29.01, -3.96) * mm, "end": v(-28.66, -3.84) * mm});
            skLineSegment(sketch, "E1491", {"start": v(-28.66, -3.84) * mm, "end": v(-28.3, -3.75) * mm});
            skLineSegment(sketch, "E1492", {"start": v(-28.3, -3.75) * mm, "end": v(-27.95, -3.69) * mm});
            skLineSegment(sketch, "E1493", {"start": v(-27.95, -3.69) * mm, "end": v(-27.77, -3.62) * mm});
            skLineSegment(sketch, "E1494", {"start": v(-27.77, -3.62) * mm, "end": v(-27.69, -3.56) * mm});
            skLineSegment(sketch, "E1495", {"start": v(-27.69, -3.56) * mm, "end": v(-27.67, -2.93) * mm});
            skLineSegment(sketch, "E1496", {"start": v(-27.67, -2.93) * mm, "end": v(-27.81, -2.32) * mm});
            skLineSegment(sketch, "E1497", {"start": v(-27.81, -2.32) * mm, "end": v(-27.9, -2.28) * mm});
            skLineSegment(sketch, "E1498", {"start": v(-27.9, -2.28) * mm, "end": v(-28.1, -2.25) * mm});
            skLineSegment(sketch, "E1499", {"start": v(-28.1, -2.25) * mm, "end": v(-28.46, -2.26) * mm});
            skLineSegment(sketch, "E1500", {"start": v(-28.46, -2.26) * mm, "end": v(-28.83, -2.25) * mm});
            skLineSegment(sketch, "E1501", {"start": v(-28.83, -2.25) * mm, "end": v(-29.2, -2.2) * mm});
            skLineSegment(sketch, "E1502", {"start": v(-29.2, -2.2) * mm, "end": v(-29.57, -2.14) * mm});
            skLineSegment(sketch, "E1503", {"start": v(-29.57, -2.14) * mm, "end": v(-29.94, -2.05) * mm});
            skLineSegment(sketch, "E1504", {"start": v(-29.94, -2.05) * mm, "end": v(-29.99, -1.12) * mm});
            skLineSegment(sketch, "E1505", {"start": v(-29.99, -1.12) * mm, "end": v(-29.62, -1) * mm});
            skLineSegment(sketch, "E1506", {"start": v(-29.62, -1) * mm, "end": v(-29.26, -0.9) * mm});
            skLineSegment(sketch, "E1507", {"start": v(-29.26, -0.9) * mm, "end": v(-28.9, -0.81) * mm});
            skLineSegment(sketch, "E1508", {"start": v(-28.9, -0.81) * mm, "end": v(-28.54, -0.76) * mm});
            skLineSegment(sketch, "E1509", {"start": v(-28.54, -0.76) * mm, "end": v(-28.17, -0.73) * mm});
            skLineSegment(sketch, "E1510", {"start": v(-28.17, -0.73) * mm, "end": v(-28, -0.68) * mm});
            skLineSegment(sketch, "E1511", {"start": v(-28, -0.68) * mm, "end": v(-27.9, -0.63) * mm});
            skLineSegment(sketch, "E1512", {"start": v(-27.9, -0.63) * mm, "end": v(-27.82, -0.01) * mm});
            skLineSegment(sketch, "E1513", {"start": v(-27.82, -0.01) * mm, "end": v(-27.9, 0.6) * mm});
            skLineSegment(sketch, "E1514", {"start": v(-27.9, 0.6) * mm, "end": v(-27.99, 0.66) * mm});
            skLineSegment(sketch, "E1515", {"start": v(-27.99, 0.66) * mm, "end": v(-28.17, 0.71) * mm});
            skLineSegment(sketch, "E1516", {"start": v(-28.17, 0.71) * mm, "end": v(-28.53, 0.74) * mm});
            skLineSegment(sketch, "E1517", {"start": v(-28.53, 0.74) * mm, "end": v(-28.9, 0.79) * mm});
            skLineSegment(sketch, "E1518", {"start": v(-28.9, 0.79) * mm, "end": v(-29.26, 0.87) * mm});
            skLineSegment(sketch, "E1519", {"start": v(-29.26, 0.87) * mm, "end": v(-29.62, 0.98) * mm});
            skLineSegment(sketch, "E1520", {"start": v(-29.62, 0.98) * mm, "end": v(-29.98, 1.1) * mm});
            skLineSegment(sketch, "E1521", {"start": v(-29.98, 1.1) * mm, "end": v(-29.93, 2.03) * mm});
            skLineSegment(sketch, "E1522", {"start": v(-29.93, 2.03) * mm, "end": v(-29.56, 2.12) * mm});
            skLineSegment(sketch, "E1523", {"start": v(-29.56, 2.12) * mm, "end": v(-29.19, 2.18) * mm});
            skLineSegment(sketch, "E1524", {"start": v(-29.19, 2.18) * mm, "end": v(-28.82, 2.23) * mm});
            skLineSegment(sketch, "E1525", {"start": v(-28.82, 2.23) * mm, "end": v(-28.45, 2.24) * mm});
            skLineSegment(sketch, "E1526", {"start": v(-28.45, 2.24) * mm, "end": v(-28.09, 2.23) * mm});
            skLineSegment(sketch, "E1527", {"start": v(-28.09, 2.23) * mm, "end": v(-27.9, 2.26) * mm});
            skLineSegment(sketch, "E1528", {"start": v(-27.9, 2.26) * mm, "end": v(-27.8, 2.3) * mm});
            skLineSegment(sketch, "E1529", {"start": v(-27.8, 2.3) * mm, "end": v(-27.66, 2.9) * mm});
            skLineSegment(sketch, "E1530", {"start": v(-27.66, 2.9) * mm, "end": v(-27.68, 3.53) * mm});
            skLineSegment(sketch, "E1531", {"start": v(-27.68, 3.53) * mm, "end": v(-27.76, 3.6) * mm});
            skLineSegment(sketch, "E1532", {"start": v(-27.76, 3.6) * mm, "end": v(-27.94, 3.66) * mm});
            skLineSegment(sketch, "E1533", {"start": v(-27.94, 3.66) * mm, "end": v(-28.3, 3.73) * mm});
            skLineSegment(sketch, "E1534", {"start": v(-28.3, 3.73) * mm, "end": v(-28.65, 3.82) * mm});
            skLineSegment(sketch, "E1535", {"start": v(-28.65, 3.82) * mm, "end": v(-29, 3.94) * mm});
            skLineSegment(sketch, "E1536", {"start": v(-29, 3.94) * mm, "end": v(-29.35, 4.08) * mm});
            skLineSegment(sketch, "E1537", {"start": v(-29.35, 4.08) * mm, "end": v(-29.7, 4.24) * mm});
            skLineSegment(sketch, "E1538", {"start": v(-29.7, 4.24) * mm, "end": v(-29.55, 5.16) * mm});
            skLineSegment(sketch, "E1539", {"start": v(-29.55, 5.16) * mm, "end": v(-29.17, 5.2) * mm});
            skLineSegment(sketch, "E1540", {"start": v(-29.17, 5.2) * mm, "end": v(-28.8, 5.23) * mm});
            skLineSegment(sketch, "E1541", {"start": v(-28.8, 5.23) * mm, "end": v(-28.42, 5.24) * mm});
            skLineSegment(sketch, "E1542", {"start": v(-28.42, 5.24) * mm, "end": v(-28.06, 5.21) * mm});
            skLineSegment(sketch, "E1543", {"start": v(-28.06, 5.21) * mm, "end": v(-27.7, 5.16) * mm});
            skLineSegment(sketch, "E1544", {"start": v(-27.7, 5.16) * mm, "end": v(-27.5, 5.18) * mm});
            skLineSegment(sketch, "E1545", {"start": v(-27.5, 5.18) * mm, "end": v(-27.4, 5.2) * mm});
            skLineSegment(sketch, "E1546", {"start": v(-27.4, 5.2) * mm, "end": v(-27.2, 5.8) * mm});
            skLineSegment(sketch, "E1547", {"start": v(-27.2, 5.8) * mm, "end": v(-27.15, 6.42) * mm});
            skLineSegment(sketch, "E1548", {"start": v(-27.15, 6.42) * mm, "end": v(-27.23, 6.48) * mm});
            skLineSegment(sketch, "E1549", {"start": v(-27.23, 6.48) * mm, "end": v(-27.4, 6.57) * mm});
            skLineSegment(sketch, "E1550", {"start": v(-27.4, 6.57) * mm, "end": v(-27.74, 6.68) * mm});
            skLineSegment(sketch, "E1551", {"start": v(-27.74, 6.68) * mm, "end": v(-28.09, 6.8) * mm});
            skLineSegment(sketch, "E1552", {"start": v(-28.09, 6.8) * mm, "end": v(-28.43, 6.96) * mm});
            skLineSegment(sketch, "E1553", {"start": v(-28.43, 6.96) * mm, "end": v(-28.76, 7.14) * mm});
            skLineSegment(sketch, "E1554", {"start": v(-28.76, 7.14) * mm, "end": v(-29.09, 7.33) * mm});
            skLineSegment(sketch, "E1555", {"start": v(-29.09, 7.33) * mm, "end": v(-28.84, 8.23) * mm});
            skLineSegment(sketch, "E1556", {"start": v(-28.84, 8.23) * mm, "end": v(-28.46, 8.24) * mm});
            skLineSegment(sketch, "E1557", {"start": v(-28.46, 8.24) * mm, "end": v(-28.09, 8.23) * mm});
            skLineSegment(sketch, "E1558", {"start": v(-28.09, 8.23) * mm, "end": v(-27.71, 8.2) * mm});
            skLineSegment(sketch, "E1559", {"start": v(-27.71, 8.2) * mm, "end": v(-27.35, 8.13) * mm});
            skLineSegment(sketch, "E1560", {"start": v(-27.35, 8.13) * mm, "end": v(-27, 8.04) * mm});
            skLineSegment(sketch, "E1561", {"start": v(-27, 8.04) * mm, "end": v(-26.8, 8.03) * mm});
            skLineSegment(sketch, "E1562", {"start": v(-26.8, 8.03) * mm, "end": v(-26.7, 8.05) * mm});
            skLineSegment(sketch, "E1563", {"start": v(-26.7, 8.05) * mm, "end": v(-26.44, 8.62) * mm});
            skLineSegment(sketch, "E1564", {"start": v(-26.44, 8.62) * mm, "end": v(-26.32, 9.23) * mm});
            skLineSegment(sketch, "E1565", {"start": v(-26.32, 9.23) * mm, "end": v(-26.4, 9.3) * mm});
            skLineSegment(sketch, "E1566", {"start": v(-26.4, 9.3) * mm, "end": v(-26.55, 9.41) * mm});
            skLineSegment(sketch, "E1567", {"start": v(-26.55, 9.41) * mm, "end": v(-26.89, 9.55) * mm});
            skLineSegment(sketch, "E1568", {"start": v(-26.89, 9.55) * mm, "end": v(-27.22, 9.71) * mm});
            skLineSegment(sketch, "E1569", {"start": v(-27.22, 9.71) * mm, "end": v(-27.54, 9.9) * mm});
            skLineSegment(sketch, "E1570", {"start": v(-27.54, 9.9) * mm, "end": v(-27.85, 10.12) * mm});
            skLineSegment(sketch, "E1571", {"start": v(-27.85, 10.12) * mm, "end": v(-28.15, 10.35) * mm});
            skLineSegment(sketch, "E1572", {"start": v(-28.15, 10.35) * mm, "end": v(-27.82, 11.21) * mm});
            skLineSegment(sketch, "E1573", {"start": v(-27.82, 11.21) * mm, "end": v(-27.44, 11.18) * mm});
            skLineSegment(sketch, "E1574", {"start": v(-27.44, 11.18) * mm, "end": v(-27.07, 11.13) * mm});
            skLineSegment(sketch, "E1575", {"start": v(-27.07, 11.13) * mm, "end": v(-26.7, 11.06) * mm});
            skLineSegment(sketch, "E1576", {"start": v(-26.7, 11.06) * mm, "end": v(-26.35, 10.95) * mm});
            skLineSegment(sketch, "E1577", {"start": v(-26.35, 10.95) * mm, "end": v(-26, 10.83) * mm});
            skLineSegment(sketch, "E1578", {"start": v(-26, 10.83) * mm, "end": v(-25.82, 10.8) * mm});
            skLineSegment(sketch, "E1579", {"start": v(-25.82, 10.8) * mm, "end": v(-25.71, 10.81) * mm});
            skLineSegment(sketch, "E1580", {"start": v(-25.71, 10.81) * mm, "end": v(-25.38, 11.34) * mm});
            skLineSegment(sketch, "E1581", {"start": v(-25.38, 11.34) * mm, "end": v(-25.2, 11.94) * mm});
            skLineSegment(sketch, "E1582", {"start": v(-25.2, 11.94) * mm, "end": v(-25.27, 12.03) * mm});
            skLineSegment(sketch, "E1583", {"start": v(-25.27, 12.03) * mm, "end": v(-25.41, 12.15) * mm});
            skLineSegment(sketch, "E1584", {"start": v(-25.41, 12.15) * mm, "end": v(-25.74, 12.32) * mm});
            skLineSegment(sketch, "E1585", {"start": v(-25.74, 12.32) * mm, "end": v(-26.05, 12.52) * mm});
            skLineSegment(sketch, "E1586", {"start": v(-26.05, 12.52) * mm, "end": v(-26.34, 12.74) * mm});
            skLineSegment(sketch, "E1587", {"start": v(-26.34, 12.74) * mm, "end": v(-26.63, 12.98) * mm});
            skLineSegment(sketch, "E1588", {"start": v(-26.63, 12.98) * mm, "end": v(-26.91, 13.24) * mm});
            skLineSegment(sketch, "E1589", {"start": v(-26.91, 13.24) * mm, "end": v(-26.49, 14.07) * mm});
            skLineSegment(sketch, "E1590", {"start": v(-26.49, 14.07) * mm, "end": v(-26.11, 14) * mm});
            skLineSegment(sketch, "E1591", {"start": v(-26.11, 14) * mm, "end": v(-25.75, 13.9) * mm});
            skLineSegment(sketch, "E1592", {"start": v(-25.75, 13.9) * mm, "end": v(-25.4, 13.8) * mm});
            skLineSegment(sketch, "E1593", {"start": v(-25.4, 13.8) * mm, "end": v(-25.05, 13.66) * mm});
            skLineSegment(sketch, "E1594", {"start": v(-25.05, 13.66) * mm, "end": v(-24.72, 13.5) * mm});
            skLineSegment(sketch, "E1595", {"start": v(-24.72, 13.5) * mm, "end": v(-24.54, 13.46) * mm});
            skLineSegment(sketch, "E1596", {"start": v(-24.54, 13.46) * mm, "end": v(-24.44, 13.45) * mm});
            skLineSegment(sketch, "E1597", {"start": v(-24.44, 13.45) * mm, "end": v(-24.05, 13.95) * mm});
            skLineSegment(sketch, "E1598", {"start": v(-24.05, 13.95) * mm, "end": v(-23.82, 14.52) * mm});
            skLineSegment(sketch, "E1599", {"start": v(-23.82, 14.52) * mm, "end": v(-23.87, 14.61) * mm});
            skLineSegment(sketch, "E1600", {"start": v(-23.87, 14.61) * mm, "end": v(-24, 14.75) * mm});
            skLineSegment(sketch, "E1601", {"start": v(-24, 14.75) * mm, "end": v(-24.3, 14.96) * mm});
            skLineSegment(sketch, "E1602", {"start": v(-24.3, 14.96) * mm, "end": v(-24.6, 15.18) * mm});
            skLineSegment(sketch, "E1603", {"start": v(-24.6, 15.18) * mm, "end": v(-24.86, 15.44) * mm});
            skLineSegment(sketch, "E1604", {"start": v(-24.86, 15.44) * mm, "end": v(-25.12, 15.7) * mm});
            skLineSegment(sketch, "E1605", {"start": v(-25.12, 15.7) * mm, "end": v(-25.37, 16) * mm});
            skLineSegment(sketch, "E1606", {"start": v(-25.37, 16) * mm, "end": v(-24.87, 16.78) * mm});
            skLineSegment(sketch, "E1607", {"start": v(-24.87, 16.78) * mm, "end": v(-24.5, 16.66) * mm});
            skLineSegment(sketch, "E1608", {"start": v(-24.5, 16.66) * mm, "end": v(-24.15, 16.53) * mm});
            skLineSegment(sketch, "E1609", {"start": v(-24.15, 16.53) * mm, "end": v(-23.8, 16.39) * mm});
            skLineSegment(sketch, "E1610", {"start": v(-23.8, 16.39) * mm, "end": v(-23.48, 16.21) * mm});
            skLineSegment(sketch, "E1611", {"start": v(-23.48, 16.21) * mm, "end": v(-23.17, 16.02) * mm});
            skLineSegment(sketch, "E1612", {"start": v(-23.17, 16.02) * mm, "end": v(-23, 15.96) * mm});
            skLineSegment(sketch, "E1613", {"start": v(-23, 15.96) * mm, "end": v(-22.9, 15.95) * mm});
            skLineSegment(sketch, "E1614", {"start": v(-22.9, 15.95) * mm, "end": v(-22.46, 16.4) * mm});
            skLineSegment(sketch, "E1615", {"start": v(-22.46, 16.4) * mm, "end": v(-22.16, 16.95) * mm});
            skLineSegment(sketch, "E1616", {"start": v(-22.16, 16.95) * mm, "end": v(-22.2, 17.04) * mm});
            skLineSegment(sketch, "E1617", {"start": v(-22.2, 17.04) * mm, "end": v(-22.32, 17.19) * mm});
            skLineSegment(sketch, "E1618", {"start": v(-22.32, 17.19) * mm, "end": v(-22.6, 17.43) * mm});
            skLineSegment(sketch, "E1619", {"start": v(-22.6, 17.43) * mm, "end": v(-22.86, 17.68) * mm});
            skLineSegment(sketch, "E1620", {"start": v(-22.86, 17.68) * mm, "end": v(-23.1, 17.96) * mm});
            skLineSegment(sketch, "E1621", {"start": v(-23.1, 17.96) * mm, "end": v(-23.34, 18.26) * mm});
            skLineSegment(sketch, "E1622", {"start": v(-23.34, 18.26) * mm, "end": v(-23.56, 18.57) * mm});
            skLineSegment(sketch, "E1623", {"start": v(-23.56, 18.57) * mm, "end": v(-22.97, 19.3) * mm});
            skLineSegment(sketch, "E1624", {"start": v(-22.97, 19.3) * mm, "end": v(-22.62, 19.14) * mm});
            skLineSegment(sketch, "E1625", {"start": v(-22.62, 19.14) * mm, "end": v(-22.28, 18.98) * mm});
            skLineSegment(sketch, "E1626", {"start": v(-22.28, 18.98) * mm, "end": v(-21.96, 18.8) * mm});
            skLineSegment(sketch, "E1627", {"start": v(-21.96, 18.8) * mm, "end": v(-21.65, 18.6) * mm});
            skLineSegment(sketch, "E1628", {"start": v(-21.65, 18.6) * mm, "end": v(-21.36, 18.37) * mm});
            skLineSegment(sketch, "E1629", {"start": v(-21.36, 18.37) * mm, "end": v(-21.2, 18.29) * mm});
            skLineSegment(sketch, "E1630", {"start": v(-21.2, 18.29) * mm, "end": v(-21.1, 18.26) * mm});
            skLineSegment(sketch, "E1631", {"start": v(-21.1, 18.26) * mm, "end": v(-20.62, 18.67) * mm});
            skLineSegment(sketch, "E1632", {"start": v(-20.62, 18.67) * mm, "end": v(-20.26, 19.18) * mm});
            skLineSegment(sketch, "E1633", {"start": v(-20.26, 19.18) * mm, "end": v(-20.3, 19.28) * mm});
            skLineSegment(sketch, "E1634", {"start": v(-20.3, 19.28) * mm, "end": v(-20.4, 19.44) * mm});
            skLineSegment(sketch, "E1635", {"start": v(-20.4, 19.44) * mm, "end": v(-20.65, 19.7) * mm});
            skLineSegment(sketch, "E1636", {"start": v(-20.65, 19.7) * mm, "end": v(-20.88, 19.99) * mm});
            skLineSegment(sketch, "E1637", {"start": v(-20.88, 19.99) * mm, "end": v(-21.1, 20.29) * mm});
            skLineSegment(sketch, "E1638", {"start": v(-21.1, 20.29) * mm, "end": v(-21.3, 20.61) * mm});
            skLineSegment(sketch, "E1639", {"start": v(-21.3, 20.61) * mm, "end": v(-21.48, 20.94) * mm});
            skLineSegment(sketch, "E1640", {"start": v(-21.48, 20.94) * mm, "end": v(-20.82, 21.6) * mm});
            skLineSegment(sketch, "E1641", {"start": v(-20.82, 21.6) * mm, "end": v(-20.49, 21.42) * mm});
            skLineSegment(sketch, "E1642", {"start": v(-20.49, 21.42) * mm, "end": v(-20.17, 21.22) * mm});
            skLineSegment(sketch, "E1643", {"start": v(-20.17, 21.22) * mm, "end": v(-19.87, 21) * mm});
            skLineSegment(sketch, "E1644", {"start": v(-19.87, 21) * mm, "end": v(-19.58, 20.76) * mm});
            skLineSegment(sketch, "E1645", {"start": v(-19.58, 20.76) * mm, "end": v(-19.32, 20.51) * mm});
            skLineSegment(sketch, "E1646", {"start": v(-19.32, 20.51) * mm, "end": v(-19.16, 20.41) * mm});
            skLineSegment(sketch, "E1647", {"start": v(-19.16, 20.41) * mm, "end": v(-19.06, 20.38) * mm});
            skLineSegment(sketch, "E1648", {"start": v(-19.06, 20.38) * mm, "end": v(-18.55, 20.73) * mm});
            skLineSegment(sketch, "E1649", {"start": v(-18.55, 20.73) * mm, "end": v(-18.14, 21.2) * mm});
            skLineSegment(sketch, "E1650", {"start": v(-18.14, 21.2) * mm, "end": v(-18.16, 21.3) * mm});
            skLineSegment(sketch, "E1651", {"start": v(-18.16, 21.3) * mm, "end": v(-18.25, 21.48) * mm});
            skLineSegment(sketch, "E1652", {"start": v(-18.25, 21.48) * mm, "end": v(-18.47, 21.77) * mm});
            skLineSegment(sketch, "E1653", {"start": v(-18.47, 21.77) * mm, "end": v(-18.67, 22.07) * mm});
            skLineSegment(sketch, "E1654", {"start": v(-18.67, 22.07) * mm, "end": v(-18.85, 22.4) * mm});
            skLineSegment(sketch, "E1655", {"start": v(-18.85, 22.4) * mm, "end": v(-19.02, 22.73) * mm});
            skLineSegment(sketch, "E1656", {"start": v(-19.02, 22.73) * mm, "end": v(-19.17, 23.09) * mm});
            skLineSegment(sketch, "E1657", {"start": v(-19.17, 23.09) * mm, "end": v(-18.44, 23.67) * mm});
            skLineSegment(sketch, "E1658", {"start": v(-18.44, 23.67) * mm, "end": v(-18.13, 23.45) * mm});
            skLineSegment(sketch, "E1659", {"start": v(-18.13, 23.45) * mm, "end": v(-17.83, 23.22) * mm});
            skLineSegment(sketch, "E1660", {"start": v(-17.83, 23.22) * mm, "end": v(-17.56, 22.97) * mm});
            skLineSegment(sketch, "E1661", {"start": v(-17.56, 22.97) * mm, "end": v(-17.3, 22.7) * mm});
            skLineSegment(sketch, "E1662", {"start": v(-17.3, 22.7) * mm, "end": v(-17.07, 22.43) * mm});
            skLineSegment(sketch, "E1663", {"start": v(-17.07, 22.43) * mm, "end": v(-16.92, 22.31) * mm});
            skLineSegment(sketch, "E1664", {"start": v(-16.92, 22.31) * mm, "end": v(-16.82, 22.27) * mm});
            skLineSegment(sketch, "E1665", {"start": v(-16.82, 22.27) * mm, "end": v(-16.27, 22.57) * mm});
            skLineSegment(sketch, "E1666", {"start": v(-16.27, 22.57) * mm, "end": v(-15.82, 23) * mm});
            skLineSegment(sketch, "E1667", {"start": v(-15.82, 23) * mm, "end": v(-15.83, 23.1) * mm});
            skLineSegment(sketch, "E1668", {"start": v(-15.83, 23.1) * mm, "end": v(-15.9, 23.28) * mm});
            skLineSegment(sketch, "E1669", {"start": v(-15.9, 23.28) * mm, "end": v(-16.09, 23.59) * mm});
            skLineSegment(sketch, "E1670", {"start": v(-16.09, 23.59) * mm, "end": v(-16.26, 23.91) * mm});
            skLineSegment(sketch, "E1671", {"start": v(-16.26, 23.91) * mm, "end": v(-16.4, 24.26) * mm});
            skLineSegment(sketch, "E1672", {"start": v(-16.4, 24.26) * mm, "end": v(-16.53, 24.6) * mm});
            skLineSegment(sketch, "E1673", {"start": v(-16.53, 24.6) * mm, "end": v(-16.64, 24.97) * mm});
            skLineSegment(sketch, "E1674", {"start": v(-16.64, 24.97) * mm, "end": v(-15.86, 25.48) * mm});
            skLineSegment(sketch, "E1675", {"start": v(-15.86, 25.48) * mm, "end": v(-15.58, 25.23) * mm});
            skLineSegment(sketch, "E1676", {"start": v(-15.58, 25.23) * mm, "end": v(-15.3, 24.97) * mm});
            skLineSegment(sketch, "E1677", {"start": v(-15.3, 24.97) * mm, "end": v(-15.05, 24.7) * mm});
            skLineSegment(sketch, "E1678", {"start": v(-15.05, 24.7) * mm, "end": v(-14.83, 24.4) * mm});
            skLineSegment(sketch, "E1679", {"start": v(-14.83, 24.4) * mm, "end": v(-14.62, 24.1) * mm});
            skLineSegment(sketch, "E1680", {"start": v(-14.62, 24.1) * mm, "end": v(-14.48, 23.97) * mm});
            skLineSegment(sketch, "E1681", {"start": v(-14.48, 23.97) * mm, "end": v(-14.4, 23.92) * mm});
            skLineSegment(sketch, "E1682", {"start": v(-14.4, 23.92) * mm, "end": v(-13.82, 24.15) * mm});
            skLineSegment(sketch, "E1683", {"start": v(-13.82, 24.15) * mm, "end": v(-13.32, 24.54) * mm});
            skLineSegment(sketch, "E1684", {"start": v(-13.32, 24.54) * mm, "end": v(-13.32, 24.64) * mm});
            skLineSegment(sketch, "E1685", {"start": v(-13.32, 24.64) * mm, "end": v(-13.37, 24.82) * mm});
            skLineSegment(sketch, "E1686", {"start": v(-13.37, 24.82) * mm, "end": v(-13.53, 25.15) * mm});
            skLineSegment(sketch, "E1687", {"start": v(-13.53, 25.15) * mm, "end": v(-13.66, 25.5) * mm});
            skLineSegment(sketch, "E1688", {"start": v(-13.66, 25.5) * mm, "end": v(-13.77, 25.85) * mm});
            skLineSegment(sketch, "E1689", {"start": v(-13.77, 25.85) * mm, "end": v(-13.86, 26.21) * mm});
            skLineSegment(sketch, "E1690", {"start": v(-13.86, 26.21) * mm, "end": v(-13.94, 26.59) * mm});
            skLineSegment(sketch, "E1691", {"start": v(-13.94, 26.59) * mm, "end": v(-13.1, 27.01) * mm});
            skLineSegment(sketch, "E1692", {"start": v(-13.1, 27.01) * mm, "end": v(-12.85, 26.73) * mm});
            skLineSegment(sketch, "E1693", {"start": v(-12.85, 26.73) * mm, "end": v(-12.6, 26.44) * mm});
            skLineSegment(sketch, "E1694", {"start": v(-12.6, 26.44) * mm, "end": v(-12.38, 26.14) * mm});
            skLineSegment(sketch, "E1695", {"start": v(-12.38, 26.14) * mm, "end": v(-12.19, 25.83) * mm});
            skLineSegment(sketch, "E1696", {"start": v(-12.19, 25.83) * mm, "end": v(-12.02, 25.51) * mm});
            skLineSegment(sketch, "E1697", {"start": v(-12.02, 25.51) * mm, "end": v(-11.9, 25.37) * mm});
            skLineSegment(sketch, "E1698", {"start": v(-11.9, 25.37) * mm, "end": v(-11.81, 25.3) * mm});
            skLineSegment(sketch, "E1699", {"start": v(-11.81, 25.3) * mm, "end": v(-11.21, 25.48) * mm});
            skLineSegment(sketch, "E1700", {"start": v(-11.21, 25.48) * mm, "end": v(-10.68, 25.8) * mm});
            skLineSegment(sketch, "E1701", {"start": v(-10.68, 25.8) * mm, "end": v(-10.67, 25.9) * mm});
            skLineSegment(sketch, "E1702", {"start": v(-10.67, 25.9) * mm, "end": v(-10.7, 26.1) * mm});
            skLineSegment(sketch, "E1703", {"start": v(-10.7, 26.1) * mm, "end": v(-10.82, 26.44) * mm});
            skLineSegment(sketch, "E1704", {"start": v(-10.82, 26.44) * mm, "end": v(-10.92, 26.8) * mm});
            skLineSegment(sketch, "E1705", {"start": v(-10.92, 26.8) * mm, "end": v(-11, 27.16) * mm});
            skLineSegment(sketch, "E1706", {"start": v(-11, 27.16) * mm, "end": v(-11.04, 27.53) * mm});
            skLineSegment(sketch, "E1707", {"start": v(-11.04, 27.53) * mm, "end": v(-11.07, 27.91) * mm});
            skLineSegment(sketch, "E1708", {"start": v(-11.07, 27.91) * mm, "end": v(-10.2, 28.24) * mm});
            skLineSegment(sketch, "E1709", {"start": v(-10.2, 28.24) * mm, "end": v(-9.98, 27.94) * mm});
            skLineSegment(sketch, "E1710", {"start": v(-9.98, 27.94) * mm, "end": v(-9.77, 27.63) * mm});
            skLineSegment(sketch, "E1711", {"start": v(-9.77, 27.63) * mm, "end": v(-9.58, 27.3) * mm});
            skLineSegment(sketch, "E1712", {"start": v(-9.58, 27.3) * mm, "end": v(-9.42, 26.98) * mm});
            skLineSegment(sketch, "E1713", {"start": v(-9.42, 26.98) * mm, "end": v(-9.28, 26.64) * mm});
            skLineSegment(sketch, "E1714", {"start": v(-9.28, 26.64) * mm, "end": v(-9.17, 26.48) * mm});
            skLineSegment(sketch, "E1715", {"start": v(-9.17, 26.48) * mm, "end": v(-9.1, 26.41) * mm});
            skLineSegment(sketch, "E1716", {"start": v(-9.1, 26.41) * mm, "end": v(-8.48, 26.52) * mm});
            skLineSegment(sketch, "E1717", {"start": v(-8.48, 26.52) * mm, "end": v(-7.92, 26.8) * mm});
            skLineSegment(sketch, "E1718", {"start": v(-7.92, 26.8) * mm, "end": v(-7.9, 26.9) * mm});
            skLineSegment(sketch, "E1719", {"start": v(-7.9, 26.9) * mm, "end": v(-7.9, 27.08) * mm});
            skLineSegment(sketch, "E1720", {"start": v(-7.9, 27.08) * mm, "end": v(-7.99, 27.44) * mm});
            skLineSegment(sketch, "E1721", {"start": v(-7.99, 27.44) * mm, "end": v(-8.05, 27.8) * mm});
            skLineSegment(sketch, "E1722", {"start": v(-8.05, 27.8) * mm, "end": v(-8.09, 28.17) * mm});
            skLineSegment(sketch, "E1723", {"start": v(-8.09, 28.17) * mm, "end": v(-8.1, 28.55) * mm});
            skLineSegment(sketch, "E1724", {"start": v(-8.1, 28.55) * mm, "end": v(-8.1, 28.93) * mm});
            skLineSegment(sketch, "E1725", {"start": v(-8.1, 28.93) * mm, "end": v(-7.2, 29.17) * mm});
            skLineSegment(sketch, "E1726", {"start": v(-7.2, 29.17) * mm, "end": v(-7, 28.84) * mm});
            skLineSegment(sketch, "E1727", {"start": v(-7, 28.84) * mm, "end": v(-6.82, 28.5) * mm});
            skLineSegment(sketch, "E1728", {"start": v(-6.82, 28.5) * mm, "end": v(-6.66, 28.17) * mm});
            skLineSegment(sketch, "E1729", {"start": v(-6.66, 28.17) * mm, "end": v(-6.54, 27.82) * mm});
            skLineSegment(sketch, "E1730", {"start": v(-6.54, 27.82) * mm, "end": v(-6.44, 27.47) * mm});
            skLineSegment(sketch, "E1731", {"start": v(-6.44, 27.47) * mm, "end": v(-6.35, 27.3) * mm});
            skLineSegment(sketch, "E1732", {"start": v(-6.35, 27.3) * mm, "end": v(-6.28, 27.23) * mm});
            skLineSegment(sketch, "E1733", {"start": v(-6.28, 27.23) * mm, "end": v(-5.66, 27.27) * mm});
            skLineSegment(sketch, "E1734", {"start": v(-5.66, 27.27) * mm, "end": v(-5.07, 27.49) * mm});
            skLineSegment(sketch, "E1735", {"start": v(-5.07, 27.49) * mm, "end": v(-5.04, 27.58) * mm});
            skLineSegment(sketch, "E1736", {"start": v(-5.04, 27.58) * mm, "end": v(-5.02, 27.77) * mm});
            skLineSegment(sketch, "E1737", {"start": v(-5.02, 27.77) * mm, "end": v(-5.07, 28.13) * mm});
            skLineSegment(sketch, "E1738", {"start": v(-5.07, 28.13) * mm, "end": v(-5.1, 28.5) * mm});
            skLineSegment(sketch, "E1739", {"start": v(-5.1, 28.5) * mm, "end": v(-5.1, 28.87) * mm});
            skLineSegment(sketch, "E1740", {"start": v(-5.1, 28.87) * mm, "end": v(-5.06, 29.25) * mm});
            skLineSegment(sketch, "E1741", {"start": v(-5.06, 29.25) * mm, "end": v(-5.02, 29.63) * mm});
            skLineSegment(sketch, "E1742", {"start": v(-5.02, 29.63) * mm, "end": v(-4.1, 29.77) * mm});
            skLineSegment(sketch, "E1743", {"start": v(-4.1, 29.77) * mm, "end": v(-3.94, 29.42) * mm});
            skLineSegment(sketch, "E1744", {"start": v(-3.94, 29.42) * mm, "end": v(-3.8, 29.08) * mm});
            skLineSegment(sketch, "E1745", {"start": v(-3.8, 29.08) * mm, "end": v(-3.68, 28.72) * mm});
            skLineSegment(sketch, "E1746", {"start": v(-3.68, 28.72) * mm, "end": v(-3.59, 28.37) * mm});
            skLineSegment(sketch, "E1747", {"start": v(-3.59, 28.37) * mm, "end": v(-3.52, 28) * mm});
            skLineSegment(sketch, "E1748", {"start": v(-3.52, 28) * mm, "end": v(-3.45, 27.83) * mm});
            skLineSegment(sketch, "E1749", {"start": v(-3.45, 27.83) * mm, "end": v(-3.4, 27.75) * mm});
            skLineSegment(sketch, "E1750", {"start": v(-3.4, 27.75) * mm, "end": v(-2.77, 27.73) * mm});
            skLineSegment(sketch, "E1751", {"start": v(-2.77, 27.73) * mm, "end": v(-2.16, 27.88) * mm});
            skLineSegment(sketch, "E1752", {"start": v(-2.16, 27.88) * mm, "end": v(-2.12, 27.97) * mm});
            skLineSegment(sketch, "E1753", {"start": v(-2.12, 27.97) * mm, "end": v(-2.09, 28.16) * mm});
            skLineSegment(sketch, "E1754", {"start": v(-2.09, 28.16) * mm, "end": v(-2.1, 28.52) * mm});
            skLineSegment(sketch, "E1755", {"start": v(-2.1, 28.52) * mm, "end": v(-2.08, 28.89) * mm});
            skLineSegment(sketch, "E1756", {"start": v(-2.08, 28.89) * mm, "end": v(-2.04, 29.26) * mm});
            skLineSegment(sketch, "E1757", {"start": v(-2.04, 29.26) * mm, "end": v(-1.97, 29.63) * mm});
            skLineSegment(sketch, "E1758", {"start": v(-1.97, 29.63) * mm, "end": v(-1.89, 30) * mm});
            skLineSegment(sketch, "E1759", {"start": v(-1.89, 30) * mm, "end": v(-0.96, 30.05) * mm});
            skLineSegment(sketch, "E1760", {"start": v(-0.96, 30.05) * mm, "end": v(-0.83, 29.69) * mm});
            skLineSegment(sketch, "E1761", {"start": v(-0.83, 29.69) * mm, "end": v(-0.73, 29.32) * mm});
            skLineSegment(sketch, "E1762", {"start": v(-0.73, 29.32) * mm, "end": v(-0.65, 28.96) * mm});
            skLineSegment(sketch, "E1763", {"start": v(-0.65, 28.96) * mm, "end": v(-0.6, 28.6) * mm});
            skLineSegment(sketch, "E1764", {"start": v(-0.6, 28.6) * mm, "end": v(-0.57, 28.23) * mm});
            skLineSegment(sketch, "E1765", {"start": v(-0.57, 28.23) * mm, "end": v(-0.52, 28.05) * mm});
            skLineSegment(sketch, "E1766", {"start": v(-0.52, 28.05) * mm, "end": v(-0.47, 27.96) * mm});
            skLineSegment(sketch, "E1767", {"start": v(-0.47, 27.96) * mm, "end": v(0.15, 27.88) * mm});
            skLineSegment(sketch, "E1768", {"start": v(0.15, 27.88) * mm, "end": v(0.77, 27.96) * mm});
            skLineSegment(sketch, "E1769", {"start": v(0.77, 27.96) * mm, "end": v(0.82, 28.05) * mm});
            skLineSegment(sketch, "E1770", {"start": v(0.82, 28.05) * mm, "end": v(0.88, 28.23) * mm});
            skLineSegment(sketch, "E1771", {"start": v(0.88, 28.23) * mm, "end": v(0.9, 28.6) * mm});
            skLineSegment(sketch, "E1772", {"start": v(0.9, 28.6) * mm, "end": v(0.95, 28.96) * mm});
            skLineSegment(sketch, "E1773", {"start": v(0.95, 28.96) * mm, "end": v(1.04, 29.32) * mm});
            skLineSegment(sketch, "E1774", {"start": v(1.04, 29.32) * mm, "end": v(1.14, 29.68) * mm});
            skLineSegment(sketch, "E1775", {"start": v(1.14, 29.68) * mm, "end": v(1.27, 30.04) * mm});
            skLineSegment(sketch, "E1776", {"start": v(1.27, 30.04) * mm, "end": v(2.2, 30) * mm});
            skLineSegment(sketch, "E1777", {"start": v(2.2, 30) * mm, "end": v(2.28, 29.62) * mm});
            skLineSegment(sketch, "E1778", {"start": v(2.28, 29.62) * mm, "end": v(2.35, 29.25) * mm});
            skLineSegment(sketch, "E1779", {"start": v(2.35, 29.25) * mm, "end": v(2.39, 28.88) * mm});
            skLineSegment(sketch, "E1780", {"start": v(2.39, 28.88) * mm, "end": v(2.4, 28.52) * mm});
            skLineSegment(sketch, "E1781", {"start": v(2.4, 28.52) * mm, "end": v(2.4, 28.15) * mm});
            skLineSegment(sketch, "E1782", {"start": v(2.4, 28.15) * mm, "end": v(2.42, 27.96) * mm});
            skLineSegment(sketch, "E1783", {"start": v(2.42, 27.96) * mm, "end": v(2.46, 27.87) * mm});
            skLineSegment(sketch, "E1784", {"start": v(2.46, 27.87) * mm, "end": v(3.07, 27.72) * mm});
            skLineSegment(sketch, "E1785", {"start": v(3.07, 27.72) * mm, "end": v(3.7, 27.74) * mm});
            skLineSegment(sketch, "E1786", {"start": v(3.7, 27.74) * mm, "end": v(3.75, 27.82) * mm});
            skLineSegment(sketch, "E1787", {"start": v(3.75, 27.82) * mm, "end": v(3.83, 28) * mm});
            skLineSegment(sketch, "E1788", {"start": v(3.83, 28) * mm, "end": v(3.9, 28.36) * mm});
            skLineSegment(sketch, "E1789", {"start": v(3.9, 28.36) * mm, "end": v(3.98, 28.71) * mm});
            skLineSegment(sketch, "E1790", {"start": v(3.98, 28.71) * mm, "end": v(4.1, 29.06) * mm});
            skLineSegment(sketch, "E1791", {"start": v(4.1, 29.06) * mm, "end": v(4.24, 29.41) * mm});
            skLineSegment(sketch, "E1792", {"start": v(4.24, 29.41) * mm, "end": v(4.4, 29.76) * mm});
            skLineSegment(sketch, "E1793", {"start": v(4.4, 29.76) * mm, "end": v(5.33, 29.61) * mm});
            skLineSegment(sketch, "E1794", {"start": v(5.33, 29.61) * mm, "end": v(5.37, 29.23) * mm});
            skLineSegment(sketch, "E1795", {"start": v(5.37, 29.23) * mm, "end": v(5.4, 28.86) * mm});
            skLineSegment(sketch, "E1796", {"start": v(5.4, 28.86) * mm, "end": v(5.4, 28.49) * mm});
            skLineSegment(sketch, "E1797", {"start": v(5.4, 28.49) * mm, "end": v(5.37, 28.12) * mm});
            skLineSegment(sketch, "E1798", {"start": v(5.37, 28.12) * mm, "end": v(5.33, 27.76) * mm});
            skLineSegment(sketch, "E1799", {"start": v(5.33, 27.76) * mm, "end": v(5.34, 27.57) * mm});
            skLineSegment(sketch, "E1800", {"start": v(5.34, 27.57) * mm, "end": v(5.37, 27.47) * mm});
            skLineSegment(sketch, "E1801", {"start": v(5.37, 27.47) * mm, "end": v(5.96, 27.26) * mm});
            skLineSegment(sketch, "E1802", {"start": v(5.96, 27.26) * mm, "end": v(6.58, 27.21) * mm});
            skLineSegment(sketch, "E1803", {"start": v(6.58, 27.21) * mm, "end": v(6.65, 27.29) * mm});
            skLineSegment(sketch, "E1804", {"start": v(6.65, 27.29) * mm, "end": v(6.74, 27.46) * mm});
            skLineSegment(sketch, "E1805", {"start": v(6.74, 27.46) * mm, "end": v(6.84, 27.8) * mm});
            skLineSegment(sketch, "E1806", {"start": v(6.84, 27.8) * mm, "end": v(6.97, 28.15) * mm});
            skLineSegment(sketch, "E1807", {"start": v(6.97, 28.15) * mm, "end": v(7.12, 28.49) * mm});
            skLineSegment(sketch, "E1808", {"start": v(7.12, 28.49) * mm, "end": v(7.3, 28.82) * mm});
            skLineSegment(sketch, "E1809", {"start": v(7.3, 28.82) * mm, "end": v(7.5, 29.15) * mm});
            skLineSegment(sketch, "E1810", {"start": v(7.5, 29.15) * mm, "end": v(8.4, 28.9) * mm});
            skLineSegment(sketch, "E1811", {"start": v(8.4, 28.9) * mm, "end": v(8.4, 28.52) * mm});
            skLineSegment(sketch, "E1812", {"start": v(8.4, 28.52) * mm, "end": v(8.39, 28.15) * mm});
            skLineSegment(sketch, "E1813", {"start": v(8.39, 28.15) * mm, "end": v(8.36, 27.78) * mm});
            skLineSegment(sketch, "E1814", {"start": v(8.36, 27.78) * mm, "end": v(8.3, 27.42) * mm});
            skLineSegment(sketch, "E1815", {"start": v(8.3, 27.42) * mm, "end": v(8.2, 27.06) * mm});
            skLineSegment(sketch, "E1816", {"start": v(8.2, 27.06) * mm, "end": v(8.2, 26.87) * mm});
            skLineSegment(sketch, "E1817", {"start": v(8.2, 26.87) * mm, "end": v(8.22, 26.77) * mm});
            skLineSegment(sketch, "E1818", {"start": v(8.22, 26.77) * mm, "end": v(8.78, 26.5) * mm});
            skLineSegment(sketch, "E1819", {"start": v(8.78, 26.5) * mm, "end": v(9.4, 26.39) * mm});
            skLineSegment(sketch, "E1820", {"start": v(9.4, 26.39) * mm, "end": v(9.47, 26.46) * mm});
            skLineSegment(sketch, "E1821", {"start": v(9.47, 26.46) * mm, "end": v(9.58, 26.61) * mm});
            skLineSegment(sketch, "E1822", {"start": v(9.58, 26.61) * mm, "end": v(9.72, 26.95) * mm});
            skLineSegment(sketch, "E1823", {"start": v(9.72, 26.95) * mm, "end": v(9.88, 27.28) * mm});
            skLineSegment(sketch, "E1824", {"start": v(9.88, 27.28) * mm, "end": v(10.07, 27.6) * mm});
            skLineSegment(sketch, "E1825", {"start": v(10.07, 27.6) * mm, "end": v(10.28, 27.91) * mm});
            skLineSegment(sketch, "E1826", {"start": v(10.28, 27.91) * mm, "end": v(10.5, 28.22) * mm});
            skLineSegment(sketch, "E1827", {"start": v(10.5, 28.22) * mm, "end": v(11.38, 27.88) * mm});
            skLineSegment(sketch, "E1828", {"start": v(11.38, 27.88) * mm, "end": v(11.34, 27.5) * mm});
            skLineSegment(sketch, "E1829", {"start": v(11.34, 27.5) * mm, "end": v(11.3, 27.13) * mm});
            skLineSegment(sketch, "E1830", {"start": v(11.3, 27.13) * mm, "end": v(11.22, 26.76) * mm});
            skLineSegment(sketch, "E1831", {"start": v(11.22, 26.76) * mm, "end": v(11.12, 26.41) * mm});
            skLineSegment(sketch, "E1832", {"start": v(11.12, 26.41) * mm, "end": v(11, 26.07) * mm});
            skLineSegment(sketch, "E1833", {"start": v(11, 26.07) * mm, "end": v(10.97, 25.88) * mm});
            skLineSegment(sketch, "E1834", {"start": v(10.97, 25.88) * mm, "end": v(10.98, 25.78) * mm});
            skLineSegment(sketch, "E1835", {"start": v(10.98, 25.78) * mm, "end": v(11.5, 25.45) * mm});
            skLineSegment(sketch, "E1836", {"start": v(11.5, 25.45) * mm, "end": v(12.1, 25.27) * mm});
            skLineSegment(sketch, "E1837", {"start": v(12.1, 25.27) * mm, "end": v(12.19, 25.33) * mm});
            skLineSegment(sketch, "E1838", {"start": v(12.19, 25.33) * mm, "end": v(12.31, 25.48) * mm});
            skLineSegment(sketch, "E1839", {"start": v(12.31, 25.48) * mm, "end": v(12.49, 25.8) * mm});
            skLineSegment(sketch, "E1840", {"start": v(12.49, 25.8) * mm, "end": v(12.68, 26.1) * mm});
            skLineSegment(sketch, "E1841", {"start": v(12.68, 26.1) * mm, "end": v(12.9, 26.4) * mm});
            skLineSegment(sketch, "E1842", {"start": v(12.9, 26.4) * mm, "end": v(13.15, 26.7) * mm});
            skLineSegment(sketch, "E1843", {"start": v(13.15, 26.7) * mm, "end": v(13.4, 26.97) * mm});
            skLineSegment(sketch, "E1844", {"start": v(13.4, 26.97) * mm, "end": v(14.24, 26.55) * mm});
            skLineSegment(sketch, "E1845", {"start": v(14.24, 26.55) * mm, "end": v(14.16, 26.18) * mm});
            skLineSegment(sketch, "E1846", {"start": v(14.16, 26.18) * mm, "end": v(14.07, 25.8) * mm});
            skLineSegment(sketch, "E1847", {"start": v(14.07, 25.8) * mm, "end": v(13.96, 25.45) * mm});
            skLineSegment(sketch, "E1848", {"start": v(13.96, 25.45) * mm, "end": v(13.82, 25.11) * mm});
            skLineSegment(sketch, "E1849", {"start": v(13.82, 25.11) * mm, "end": v(13.66, 24.79) * mm});
            skLineSegment(sketch, "E1850", {"start": v(13.66, 24.79) * mm, "end": v(13.62, 24.6) * mm});
            skLineSegment(sketch, "E1851", {"start": v(13.62, 24.6) * mm, "end": v(13.62, 24.5) * mm});
            skLineSegment(sketch, "E1852", {"start": v(13.62, 24.5) * mm, "end": v(14.11, 24.12) * mm});
            skLineSegment(sketch, "E1853", {"start": v(14.11, 24.12) * mm, "end": v(14.69, 23.88) * mm});
            skLineSegment(sketch, "E1854", {"start": v(14.69, 23.88) * mm, "end": v(14.78, 23.93) * mm});
            skLineSegment(sketch, "E1855", {"start": v(14.78, 23.93) * mm, "end": v(14.91, 24.06) * mm});
            skLineSegment(sketch, "E1856", {"start": v(14.91, 24.06) * mm, "end": v(15.12, 24.36) * mm});
            skLineSegment(sketch, "E1857", {"start": v(15.12, 24.36) * mm, "end": v(15.35, 24.65) * mm});
            skLineSegment(sketch, "E1858", {"start": v(15.35, 24.65) * mm, "end": v(15.6, 24.92) * mm});
            skLineSegment(sketch, "E1859", {"start": v(15.6, 24.92) * mm, "end": v(15.87, 25.19) * mm});
            skLineSegment(sketch, "E1860", {"start": v(15.87, 25.19) * mm, "end": v(16.16, 25.44) * mm});
            skLineSegment(sketch, "E1861", {"start": v(16.16, 25.44) * mm, "end": v(16.94, 24.93) * mm});
            skLineSegment(sketch, "E1862", {"start": v(16.94, 24.93) * mm, "end": v(16.83, 24.56) * mm});
            skLineSegment(sketch, "E1863", {"start": v(16.83, 24.56) * mm, "end": v(16.7, 24.2) * mm});
            skLineSegment(sketch, "E1864", {"start": v(16.7, 24.2) * mm, "end": v(16.55, 23.87) * mm});
            skLineSegment(sketch, "E1865", {"start": v(16.55, 23.87) * mm, "end": v(16.38, 23.54) * mm});
            skLineSegment(sketch, "E1866", {"start": v(16.38, 23.54) * mm, "end": v(16.19, 23.23) * mm});
            skLineSegment(sketch, "E1867", {"start": v(16.19, 23.23) * mm, "end": v(16.12, 23.06) * mm});
            skLineSegment(sketch, "E1868", {"start": v(16.12, 23.06) * mm, "end": v(16.1, 22.95) * mm});
            skLineSegment(sketch, "E1869", {"start": v(16.1, 22.95) * mm, "end": v(16.56, 22.52) * mm});
            skLineSegment(sketch, "E1870", {"start": v(16.56, 22.52) * mm, "end": v(17.11, 22.22) * mm});
            skLineSegment(sketch, "E1871", {"start": v(17.11, 22.22) * mm, "end": v(17.2, 22.27) * mm});
            skLineSegment(sketch, "E1872", {"start": v(17.2, 22.27) * mm, "end": v(17.35, 22.38) * mm});
            skLineSegment(sketch, "E1873", {"start": v(17.35, 22.38) * mm, "end": v(17.6, 22.66) * mm});
            skLineSegment(sketch, "E1874", {"start": v(17.6, 22.66) * mm, "end": v(17.85, 22.92) * mm});
            skLineSegment(sketch, "E1875", {"start": v(17.85, 22.92) * mm, "end": v(18.13, 23.17) * mm});
            skLineSegment(sketch, "E1876", {"start": v(18.13, 23.17) * mm, "end": v(18.42, 23.4) * mm});
            skLineSegment(sketch, "E1877", {"start": v(18.42, 23.4) * mm, "end": v(18.74, 23.62) * mm});
            skLineSegment(sketch, "E1878", {"start": v(18.74, 23.62) * mm, "end": v(19.46, 23.03) * mm});
            skLineSegment(sketch, "E1879", {"start": v(19.46, 23.03) * mm, "end": v(19.3, 22.68) * mm});
            skLineSegment(sketch, "E1880", {"start": v(19.3, 22.68) * mm, "end": v(19.14, 22.34) * mm});
            skLineSegment(sketch, "E1881", {"start": v(19.14, 22.34) * mm, "end": v(18.96, 22.02) * mm});
            skLineSegment(sketch, "E1882", {"start": v(18.96, 22.02) * mm, "end": v(18.76, 21.71) * mm});
            skLineSegment(sketch, "E1883", {"start": v(18.76, 21.71) * mm, "end": v(18.53, 21.43) * mm});
            skLineSegment(sketch, "E1884", {"start": v(18.53, 21.43) * mm, "end": v(18.45, 21.26) * mm});
            skLineSegment(sketch, "E1885", {"start": v(18.45, 21.26) * mm, "end": v(18.43, 21.15) * mm});
            skLineSegment(sketch, "E1886", {"start": v(18.43, 21.15) * mm, "end": v(18.83, 20.68) * mm});
            skLineSegment(sketch, "E1887", {"start": v(18.83, 20.68) * mm, "end": v(19.35, 20.33) * mm});
            skLineSegment(sketch, "E1888", {"start": v(19.35, 20.33) * mm, "end": v(19.44, 20.36) * mm});
            skLineSegment(sketch, "E1889", {"start": v(19.44, 20.36) * mm, "end": v(19.6, 20.46) * mm});
            skLineSegment(sketch, "E1890", {"start": v(19.6, 20.46) * mm, "end": v(19.87, 20.7) * mm});
            skLineSegment(sketch, "E1891", {"start": v(19.87, 20.7) * mm, "end": v(20.15, 20.95) * mm});
            skLineSegment(sketch, "E1892", {"start": v(20.15, 20.95) * mm, "end": v(20.45, 21.16) * mm});
            skLineSegment(sketch, "E1893", {"start": v(20.45, 21.16) * mm, "end": v(20.77, 21.36) * mm});
            skLineSegment(sketch, "E1894", {"start": v(20.77, 21.36) * mm, "end": v(21.1, 21.54) * mm});
            skLineSegment(sketch, "E1895", {"start": v(21.1, 21.54) * mm, "end": v(21.77, 20.88) * mm});
            skLineSegment(sketch, "E1896", {"start": v(21.77, 20.88) * mm, "end": v(21.58, 20.55) * mm});
            skLineSegment(sketch, "E1897", {"start": v(21.58, 20.55) * mm, "end": v(21.38, 20.23) * mm});
            skLineSegment(sketch, "E1898", {"start": v(21.38, 20.23) * mm, "end": v(21.17, 19.93) * mm});
            skLineSegment(sketch, "E1899", {"start": v(21.17, 19.93) * mm, "end": v(20.93, 19.65) * mm});
            skLineSegment(sketch, "E1900", {"start": v(20.93, 19.65) * mm, "end": v(20.68, 19.38) * mm});
            skLineSegment(sketch, "E1901", {"start": v(20.68, 19.38) * mm, "end": v(20.58, 19.22) * mm});
            skLineSegment(sketch, "E1902", {"start": v(20.58, 19.22) * mm, "end": v(20.54, 19.12) * mm});
            skLineSegment(sketch, "E1903", {"start": v(20.54, 19.12) * mm, "end": v(20.9, 18.6) * mm});
            skLineSegment(sketch, "E1904", {"start": v(20.9, 18.6) * mm, "end": v(21.37, 18.2) * mm});
            skLineSegment(sketch, "E1905", {"start": v(21.37, 18.2) * mm, "end": v(21.47, 18.23) * mm});
            skLineSegment(sketch, "E1906", {"start": v(21.47, 18.23) * mm, "end": v(21.64, 18.3) * mm});
            skLineSegment(sketch, "E1907", {"start": v(21.64, 18.3) * mm, "end": v(21.93, 18.53) * mm});
            skLineSegment(sketch, "E1908", {"start": v(21.93, 18.53) * mm, "end": v(22.23, 18.74) * mm});
            skLineSegment(sketch, "E1909", {"start": v(22.23, 18.74) * mm, "end": v(22.56, 18.92) * mm});
            skLineSegment(sketch, "E1910", {"start": v(22.56, 18.92) * mm, "end": v(22.9, 19.08) * mm});
            skLineSegment(sketch, "E1911", {"start": v(22.9, 19.08) * mm, "end": v(23.25, 19.23) * mm});
            skLineSegment(sketch, "E1912", {"start": v(23.25, 19.23) * mm, "end": v(23.84, 18.5) * mm});
            skLineSegment(sketch, "E1913", {"start": v(23.84, 18.5) * mm, "end": v(23.62, 18.2) * mm});
            skLineSegment(sketch, "E1914", {"start": v(23.62, 18.2) * mm, "end": v(23.38, 17.9) * mm});
            skLineSegment(sketch, "E1915", {"start": v(23.38, 17.9) * mm, "end": v(23.14, 17.62) * mm});
            skLineSegment(sketch, "E1916", {"start": v(23.14, 17.62) * mm, "end": v(22.87, 17.36) * mm});
            skLineSegment(sketch, "E1917", {"start": v(22.87, 17.36) * mm, "end": v(22.6, 17.13) * mm});
            skLineSegment(sketch, "E1918", {"start": v(22.6, 17.13) * mm, "end": v(22.48, 16.98) * mm});
            skLineSegment(sketch, "E1919", {"start": v(22.48, 16.98) * mm, "end": v(22.44, 16.88) * mm});
            skLineSegment(sketch, "E1920", {"start": v(22.44, 16.88) * mm, "end": v(22.73, 16.33) * mm});
            skLineSegment(sketch, "E1921", {"start": v(22.73, 16.33) * mm, "end": v(23.16, 15.88) * mm});
            skLineSegment(sketch, "E1922", {"start": v(23.16, 15.88) * mm, "end": v(23.26, 15.9) * mm});
            skLineSegment(sketch, "E1923", {"start": v(23.26, 15.9) * mm, "end": v(23.44, 15.96) * mm});
            skLineSegment(sketch, "E1924", {"start": v(23.44, 15.96) * mm, "end": v(23.75, 16.15) * mm});
            skLineSegment(sketch, "E1925", {"start": v(23.75, 16.15) * mm, "end": v(24.08, 16.32) * mm});
            skLineSegment(sketch, "E1926", {"start": v(24.08, 16.32) * mm, "end": v(24.42, 16.47) * mm});
            skLineSegment(sketch, "E1927", {"start": v(24.42, 16.47) * mm, "end": v(24.77, 16.6) * mm});
            skLineSegment(sketch, "E1928", {"start": v(24.77, 16.6) * mm, "end": v(25.14, 16.7) * mm});
            skLineSegment(sketch, "E1929", {"start": v(25.14, 16.7) * mm, "end": v(25.64, 15.92) * mm});
            skLineSegment(sketch, "E1930", {"start": v(25.64, 15.92) * mm, "end": v(25.4, 15.64) * mm});
            skLineSegment(sketch, "E1931", {"start": v(25.4, 15.64) * mm, "end": v(25.13, 15.37) * mm});
            skLineSegment(sketch, "E1932", {"start": v(25.13, 15.37) * mm, "end": v(24.86, 15.11) * mm});
            skLineSegment(sketch, "E1933", {"start": v(24.86, 15.11) * mm, "end": v(24.57, 14.89) * mm});
            skLineSegment(sketch, "E1934", {"start": v(24.57, 14.89) * mm, "end": v(24.27, 14.68) * mm});
            skLineSegment(sketch, "E1935", {"start": v(24.27, 14.68) * mm, "end": v(24.14, 14.55) * mm});
            skLineSegment(sketch, "E1936", {"start": v(24.14, 14.55) * mm, "end": v(24.08, 14.46) * mm});
            skLineSegment(sketch, "E1937", {"start": v(24.08, 14.46) * mm, "end": v(24.32, 13.88) * mm});
            skLineSegment(sketch, "E1938", {"start": v(24.32, 13.88) * mm, "end": v(24.7, 13.38) * mm});
            skLineSegment(sketch, "E1939", {"start": v(24.7, 13.38) * mm, "end": v(24.8, 13.39) * mm});
            skLineSegment(sketch, "E1940", {"start": v(24.8, 13.39) * mm, "end": v(24.99, 13.43) * mm});
            skLineSegment(sketch, "E1941", {"start": v(24.99, 13.43) * mm, "end": v(25.32, 13.59) * mm});
            skLineSegment(sketch, "E1942", {"start": v(25.32, 13.59) * mm, "end": v(25.66, 13.73) * mm});
            skLineSegment(sketch, "E1943", {"start": v(25.66, 13.73) * mm, "end": v(26.01, 13.84) * mm});
            skLineSegment(sketch, "E1944", {"start": v(26.01, 13.84) * mm, "end": v(26.38, 13.92) * mm});
            skLineSegment(sketch, "E1945", {"start": v(26.38, 13.92) * mm, "end": v(26.75, 14) * mm});
            skLineSegment(sketch, "E1946", {"start": v(26.75, 14) * mm, "end": v(27.17, 13.17) * mm});
            skLineSegment(sketch, "E1947", {"start": v(27.17, 13.17) * mm, "end": v(26.9, 12.9) * mm});
            skLineSegment(sketch, "E1948", {"start": v(26.9, 12.9) * mm, "end": v(26.6, 12.67) * mm});
            skLineSegment(sketch, "E1949", {"start": v(26.6, 12.67) * mm, "end": v(26.3, 12.44) * mm});
            skLineSegment(sketch, "E1950", {"start": v(26.3, 12.44) * mm, "end": v(26, 12.25) * mm});
            skLineSegment(sketch, "E1951", {"start": v(26, 12.25) * mm, "end": v(25.67, 12.08) * mm});
            skLineSegment(sketch, "E1952", {"start": v(25.67, 12.08) * mm, "end": v(25.53, 11.95) * mm});
            skLineSegment(sketch, "E1953", {"start": v(25.53, 11.95) * mm, "end": v(25.47, 11.87) * mm});
            skLineSegment(sketch, "E1954", {"start": v(25.47, 11.87) * mm, "end": v(25.64, 11.27) * mm});
            skLineSegment(sketch, "E1955", {"start": v(25.64, 11.27) * mm, "end": v(25.97, 10.74) * mm});
            skLineSegment(sketch, "E1956", {"start": v(25.97, 10.74) * mm, "end": v(26.07, 10.73) * mm});
            skLineSegment(sketch, "E1957", {"start": v(26.07, 10.73) * mm, "end": v(26.26, 10.76) * mm});
            skLineSegment(sketch, "E1958", {"start": v(26.26, 10.76) * mm, "end": v(26.6, 10.88) * mm});
            skLineSegment(sketch, "E1959", {"start": v(26.6, 10.88) * mm, "end": v(26.96, 10.98) * mm});
            skLineSegment(sketch, "E1960", {"start": v(26.96, 10.98) * mm, "end": v(27.32, 11.05) * mm});
            skLineSegment(sketch, "E1961", {"start": v(27.32, 11.05) * mm, "end": v(27.7, 11.1) * mm});
            skLineSegment(sketch, "E1962", {"start": v(27.7, 11.1) * mm, "end": v(28.08, 11.14) * mm});
            skLineSegment(sketch, "E1963", {"start": v(28.08, 11.14) * mm, "end": v(28.4, 10.27) * mm});
            skLineSegment(sketch, "E1964", {"start": v(28.4, 10.27) * mm, "end": v(28.1, 10.04) * mm});
            skLineSegment(sketch, "E1965", {"start": v(28.1, 10.04) * mm, "end": v(27.8, 9.83) * mm});
            skLineSegment(sketch, "E1966", {"start": v(27.8, 9.83) * mm, "end": v(27.47, 9.64) * mm});
            skLineSegment(sketch, "E1967", {"start": v(27.47, 9.64) * mm, "end": v(27.14, 9.48) * mm});
            skLineSegment(sketch, "E1968", {"start": v(27.14, 9.48) * mm, "end": v(26.8, 9.34) * mm});
            skLineSegment(sketch, "E1969", {"start": v(26.8, 9.34) * mm, "end": v(26.65, 9.23) * mm});
            skLineSegment(sketch, "E1970", {"start": v(26.65, 9.23) * mm, "end": v(26.58, 9.16) * mm});
            skLineSegment(sketch, "E1971", {"start": v(26.58, 9.16) * mm, "end": v(26.69, 8.54) * mm});
            skLineSegment(sketch, "E1972", {"start": v(26.69, 8.54) * mm, "end": v(26.96, 7.98) * mm});
            skLineSegment(sketch, "E1973", {"start": v(26.96, 7.98) * mm, "end": v(27.06, 7.96) * mm});
            skLineSegment(sketch, "E1974", {"start": v(27.06, 7.96) * mm, "end": v(27.25, 7.96) * mm});
            skLineSegment(sketch, "E1975", {"start": v(27.25, 7.96) * mm, "end": v(27.6, 8.05) * mm});
            skLineSegment(sketch, "E1976", {"start": v(27.6, 8.05) * mm, "end": v(27.96, 8.11) * mm});
            skLineSegment(sketch, "E1977", {"start": v(27.96, 8.11) * mm, "end": v(28.33, 8.15) * mm});
            skLineSegment(sketch, "E1978", {"start": v(28.33, 8.15) * mm, "end": v(28.71, 8.16) * mm});
            skLineSegment(sketch, "E1979", {"start": v(28.71, 8.16) * mm, "end": v(29.1, 8.15) * mm});
            skLineSegment(sketch, "E1980", {"start": v(29.1, 8.15) * mm, "end": v(29.33, 7.25) * mm});
            skLineSegment(sketch, "E1981", {"start": v(29.33, 7.25) * mm, "end": v(29, 7.06) * mm});
            skLineSegment(sketch, "E1982", {"start": v(29, 7.06) * mm, "end": v(28.67, 6.88) * mm});
            skLineSegment(sketch, "E1983", {"start": v(28.67, 6.88) * mm, "end": v(28.33, 6.72) * mm});
            skLineSegment(sketch, "E1984", {"start": v(28.33, 6.72) * mm, "end": v(27.99, 6.6) * mm});
            skLineSegment(sketch, "E1985", {"start": v(27.99, 6.6) * mm, "end": v(27.64, 6.5) * mm});
            skLineSegment(sketch, "E1986", {"start": v(27.64, 6.5) * mm, "end": v(27.47, 6.4) * mm});
            skLineSegment(sketch, "E1987", {"start": v(27.47, 6.4) * mm, "end": v(27.4, 6.34) * mm});
            skLineSegment(sketch, "E1988", {"start": v(27.4, 6.34) * mm, "end": v(27.44, 5.72) * mm});
            skLineSegment(sketch, "E1989", {"start": v(27.44, 5.72) * mm, "end": v(27.65, 5.13) * mm});
            skLineSegment(sketch, "E1990", {"start": v(27.65, 5.13) * mm, "end": v(27.75, 5.1) * mm});
            skLineSegment(sketch, "E1991", {"start": v(27.75, 5.1) * mm, "end": v(27.94, 5.08) * mm});
            skLineSegment(sketch, "E1992", {"start": v(27.94, 5.08) * mm, "end": v(28.3, 5.13) * mm});
            skLineSegment(sketch, "E1993", {"start": v(28.3, 5.13) * mm, "end": v(28.66, 5.16) * mm});
            skLineSegment(sketch, "E1994", {"start": v(28.66, 5.16) * mm, "end": v(29.04, 5.15) * mm});
            skLineSegment(sketch, "E1995", {"start": v(29.04, 5.15) * mm, "end": v(29.41, 5.12) * mm});
            skLineSegment(sketch, "E1996", {"start": v(29.41, 5.12) * mm, "end": v(29.8, 5.08) * mm});
            skLineSegment(sketch, "E1997", {"start": v(29.8, 5.08) * mm, "end": v(29.94, 4.16) * mm});
            skLineSegment(sketch, "E1998", {"start": v(29.94, 4.16) * mm, "end": v(29.59, 4) * mm});
            skLineSegment(sketch, "E1999", {"start": v(29.59, 4) * mm, "end": v(29.24, 3.86) * mm});
            skLineSegment(sketch, "E2000", {"start": v(29.24, 3.86) * mm, "end": v(28.89, 3.74) * mm});
            skLineSegment(sketch, "E2001", {"start": v(28.89, 3.74) * mm, "end": v(28.53, 3.65) * mm});
            skLineSegment(sketch, "E2002", {"start": v(28.53, 3.65) * mm, "end": v(28.17, 3.58) * mm});
            skLineSegment(sketch, "E2003", {"start": v(28.17, 3.58) * mm, "end": v(28, 3.51) * mm});
            skLineSegment(sketch, "E2004", {"start": v(28, 3.51) * mm, "end": v(27.91, 3.45) * mm});
            skLineSegment(sketch, "E2005", {"start": v(27.91, 3.45) * mm, "end": v(27.9, 2.83) * mm});
            skLineSegment(sketch, "E2006", {"start": v(27.9, 2.83) * mm, "end": v(28.04, 2.22) * mm});
            skLineSegment(sketch, "E2007", {"start": v(28.04, 2.22) * mm, "end": v(28.13, 2.18) * mm});
            skLineSegment(sketch, "E2008", {"start": v(28.13, 2.18) * mm, "end": v(28.32, 2.15) * mm});
            skLineSegment(sketch, "E2009", {"start": v(28.32, 2.15) * mm, "end": v(28.69, 2.16) * mm});
            skLineSegment(sketch, "E2010", {"start": v(28.69, 2.16) * mm, "end": v(29.05, 2.14) * mm});
            skLineSegment(sketch, "E2011", {"start": v(29.05, 2.14) * mm, "end": v(29.42, 2.1) * mm});
            skLineSegment(sketch, "E2012", {"start": v(29.42, 2.1) * mm, "end": v(29.8, 2.03) * mm});
            skLineSegment(sketch, "E2013", {"start": v(29.8, 2.03) * mm, "end": v(30.16, 1.95) * mm});
            skLineSegment(sketch, "E2014", {"start": v(30.16, 1.95) * mm, "end": v(30.21, 1.02) * mm});
            skLineSegment(sketch, "E2015", {"start": v(30.21, 1.02) * mm, "end": v(29.85, 0.9) * mm});
            skLineSegment(sketch, "E2016", {"start": v(29.85, 0.9) * mm, "end": v(29.49, 0.8) * mm});
            skLineSegment(sketch, "E2017", {"start": v(29.49, 0.8) * mm, "end": v(29.13, 0.7) * mm});
            skLineSegment(sketch, "E2018", {"start": v(29.13, 0.7) * mm, "end": v(28.76, 0.66) * mm});
            skLineSegment(sketch, "E2019", {"start": v(28.76, 0.66) * mm, "end": v(28.4, 0.63) * mm});
            skLineSegment(sketch, "E2020", {"start": v(28.4, 0.63) * mm, "end": v(28.22, 0.58) * mm});
            skLineSegment(sketch, "E2021", {"start": v(28.22, 0.58) * mm, "end": v(28.13, 0.53) * mm});
            skLineSegment(sketch, "E2022", {"start": v(28.13, 0.53) * mm, "end": v(28.04, -0.1) * mm});
            skLineSegment(sketch, "E2023", {"start": v(28.04, -0.1) * mm, "end": v(28.12, -0.7) * mm});
            skLineSegment(sketch, "E2024", {"start": v(28.12, -0.7) * mm, "end": v(28.21, -0.76) * mm});
            skLineSegment(sketch, "E2025", {"start": v(28.21, -0.76) * mm, "end": v(28.4, -0.81) * mm});
            skLineSegment(sketch, "E2026", {"start": v(28.4, -0.81) * mm, "end": v(28.76, -0.84) * mm});
            skLineSegment(sketch, "E2027", {"start": v(28.76, -0.84) * mm, "end": v(29.12, -0.9) * mm});
            skLineSegment(sketch, "E2028", {"start": v(29.12, -0.9) * mm, "end": v(29.49, -0.98) * mm});
            skLineSegment(sketch, "E2029", {"start": v(29.49, -0.98) * mm, "end": v(29.85, -1.08) * mm});
            skLineSegment(sketch, "E2030", {"start": v(29.85, -1.08) * mm, "end": v(30.2, -1.2) * mm});
            skLineSegment(sketch, "E2031", {"start": v(30.2, -1.2) * mm, "end": v(30.16, -2.13) * mm});
            skLineSegment(sketch, "E2032", {"start": v(30.16, -2.13) * mm, "end": v(29.79, -2.22) * mm});
            skLineSegment(sketch, "E2033", {"start": v(29.79, -2.22) * mm, "end": v(29.42, -2.28) * mm});
            skLineSegment(sketch, "E2034", {"start": v(29.42, -2.28) * mm, "end": v(29.05, -2.33) * mm});
            skLineSegment(sketch, "E2035", {"start": v(29.05, -2.33) * mm, "end": v(28.68, -2.34) * mm});
            skLineSegment(sketch, "E2036", {"start": v(28.68, -2.34) * mm, "end": v(28.31, -2.33) * mm});
            skLineSegment(sketch, "E2037", {"start": v(28.31, -2.33) * mm, "end": v(28.13, -2.36) * mm});
            skLineSegment(sketch, "E2038", {"start": v(28.13, -2.36) * mm, "end": v(28.03, -2.4) * mm});
            skLineSegment(sketch, "E2039", {"start": v(28.03, -2.4) * mm, "end": v(27.88, -3) * mm});
            skSolve(sketch);
        }
        {
            var Q0;
            Q0 = qSketchRegion(id + "F0", true);
            var Q1;
            Q1 = qSketchRegion(id + "F2", true);
            loft(context, id + "F3", {"sheetProfilesArray" : [{ "sheetProfileEntities" : qUnion([Q0]) }, { "sheetProfileEntities" : qUnion([Q1]) }]});
        }
        {
            var Q0;
            Q0=makeQuery(id+"F3.opLoft","CAP_FACE",FACE,{"disambiguationData":[OSD([makeQuery(id+"F2.imprint","IMPRINT",FACE,{"disambiguationData":[TD([[makeQuery(id+"F2.imprint","IMPRINT",EDGE,{"derivedFrom":sQuery(id+"F2.wireOp",EDGE,"E1020")}),-1.0]])]})])],"isStart":true});
            var sketch = newSketch(context, id + "F4", { "sketchPlane" : qUnion([Q0])});
            skCircle(sketch, "E2040", {"center": v(0, 0) * mm, "radius": 4 * mm});
            skSolve(sketch);
        }
        {
            var Q0;
            Q0 = qSketchRegion(id + "F4", true);
            extrude(context, id + "F5", {"entities" : qUnion([Q0]), "operationType" : NewBodyOperationType.REMOVE, "oppositeDirection" : true, "depth" : 25 * mm, "offsetDistance" : 25 * mm});
        }
        {
            var Q0;
            Q0=makeQuery(id+"F3.opLoft","CAP_FACE",FACE,{"disambiguationData":[OSD([makeQuery(id+"F2.imprint","IMPRINT",FACE,{"disambiguationData":[TD([[makeQuery(id+"F2.imprint","IMPRINT",EDGE,{"derivedFrom":sQuery(id+"F2.wireOp",EDGE,"E1020")}),-1.0]])]})])],"isStart":true});
            var sketch = newSketch(context, id + "F6", { "sketchPlane" : qUnion([Q0])});
            skArc(sketch, "E2041", {"start": v(-20.5, 9.3) * mm, "mid": v(-22.5, 0) * mm, "end": v(-20.5, -9.3) * mm});
            skArc(sketch, "E2042", {"start": v(-8.48, 3) * mm, "mid": v(-9, 0) * mm, "end": v(-8.48, -3) * mm});
            skLineSegment(sketch, "E2043", {"start": v(0, 10.82) * mm, "end": v(0, 20.4) * mm});
            skLineSegment(sketch, "E2044.1.0", {"start": v(-9.37, 5.4) * mm, "end": v(-17.67, 10.2) * mm});
            skLineSegment(sketch, "E2044.2.0", {"start": v(-9.37, -5.4) * mm, "end": v(-17.67, -10.2) * mm});
            skLineSegment(sketch, "E2044.3.0", {"start": v(0, -10.82) * mm, "end": v(0, -20.4) * mm});
            skLineSegment(sketch, "E2044.4.0", {"start": v(9.37, -5.4) * mm, "end": v(17.67, -10.2) * mm});
            skLineSegment(sketch, "E2044.5.0", {"start": v(9.37, 5.4) * mm, "end": v(17.67, 10.2) * mm});
            skArc(sketch, "E2045.trimOffspring", {"start": v(1.64, -8.85) * mm, "mid": v(4.5, -7.8) * mm, "end": v(6.85, -5.84) * mm});
            skArc(sketch, "E2046.trimOffspring", {"start": v(2.2, -22.4) * mm, "mid": v(11.25, -19.49) * mm, "end": v(18.3, -13.1) * mm});
            skArc(sketch, "E2047.trimOffspring", {"start": v(6.85, 5.84) * mm, "mid": v(4.5, 7.8) * mm, "end": v(1.64, 8.85) * mm});
            skArc(sketch, "E2048.trimOffspring", {"start": v(18.3, 13.1) * mm, "mid": v(11.25, 19.49) * mm, "end": v(2.2, 22.4) * mm});
            skPoint(sketch, "E2049.visualSharp", {"position": v(-19.49, 11.25) * mm});
            skArc(sketch, "E2049.filletArc", {"start": v(-17.67, 10.2) * mm, "mid": v(-19.28, 10.37) * mm, "end": v(-20.5, 9.3) * mm});
            skPoint(sketch, "E2050.visualSharp", {"position": v(-7.8, 4.5) * mm});
            skArc(sketch, "E2050.filletArc", {"start": v(-8.48, 3) * mm, "mid": v(-8.5, 4.37) * mm, "end": v(-9.37, 5.4) * mm});
            skPoint(sketch, "E2051.visualSharp", {"position": v(-7.8, -4.5) * mm});
            skArc(sketch, "E2051.filletArc", {"start": v(-9.37, -5.4) * mm, "mid": v(-8.5, -4.37) * mm, "end": v(-8.48, -3) * mm});
            skPoint(sketch, "E2052.visualSharp", {"position": v(-19.49, -11.25) * mm});
            skArc(sketch, "E2052.filletArc", {"start": v(-20.5, -9.3) * mm, "mid": v(-19.28, -10.37) * mm, "end": v(-17.67, -10.2) * mm});
            skPoint(sketch, "E2053.visualSharp", {"position": v(0, -9) * mm});
            skArc(sketch, "E2053.filletArc", {"start": v(1.64, -8.85) * mm, "mid": v(0.46, -9.54) * mm, "end": v(0, -10.82) * mm});
            skPoint(sketch, "E2054.visualSharp", {"position": v(0, -22.5) * mm});
            skArc(sketch, "E2054.filletArc", {"start": v(0, -20.4) * mm, "mid": v(0.66, -21.88) * mm, "end": v(2.2, -22.4) * mm});
            skPoint(sketch, "E2055.visualSharp", {"position": v(19.49, -11.25) * mm});
            skArc(sketch, "E2055.filletArc", {"start": v(18.3, -13.1) * mm, "mid": v(18.62, -11.51) * mm, "end": v(17.67, -10.2) * mm});
            skPoint(sketch, "E2056.visualSharp", {"position": v(7.8, -4.5) * mm});
            skArc(sketch, "E2056.filletArc", {"start": v(9.37, -5.4) * mm, "mid": v(8.03, -5.17) * mm, "end": v(6.85, -5.84) * mm});
            skPoint(sketch, "E2057.visualSharp", {"position": v(7.8, 4.5) * mm});
            skArc(sketch, "E2057.filletArc", {"start": v(6.85, 5.84) * mm, "mid": v(8.03, 5.17) * mm, "end": v(9.37, 5.4) * mm});
            skPoint(sketch, "E2058.visualSharp", {"position": v(19.49, 11.25) * mm});
            skArc(sketch, "E2058.filletArc", {"start": v(17.67, 10.2) * mm, "mid": v(18.62, 11.51) * mm, "end": v(18.3, 13.1) * mm});
            skPoint(sketch, "E2059.visualSharp", {"position": v(0, 22.5) * mm});
            skArc(sketch, "E2059.filletArc", {"start": v(2.2, 22.4) * mm, "mid": v(0.66, 21.88) * mm, "end": v(0, 20.4) * mm});
            skPoint(sketch, "E2060.visualSharp", {"position": v(0, 9) * mm});
            skArc(sketch, "E2060.filletArc", {"start": v(0, 10.82) * mm, "mid": v(0.46, 9.54) * mm, "end": v(1.64, 8.85) * mm});
            skSolve(sketch);
        }
        {
            var Q0;
            Q0 = qSketchRegion(id + "F6", true);
            extrude(context, id + "F7", {"entities" : qUnion([Q0]), "operationType" : NewBodyOperationType.REMOVE, "oppositeDirection" : true, "depth" : 25 * mm, "offsetDistance" : 25 * mm});
        }
    });
